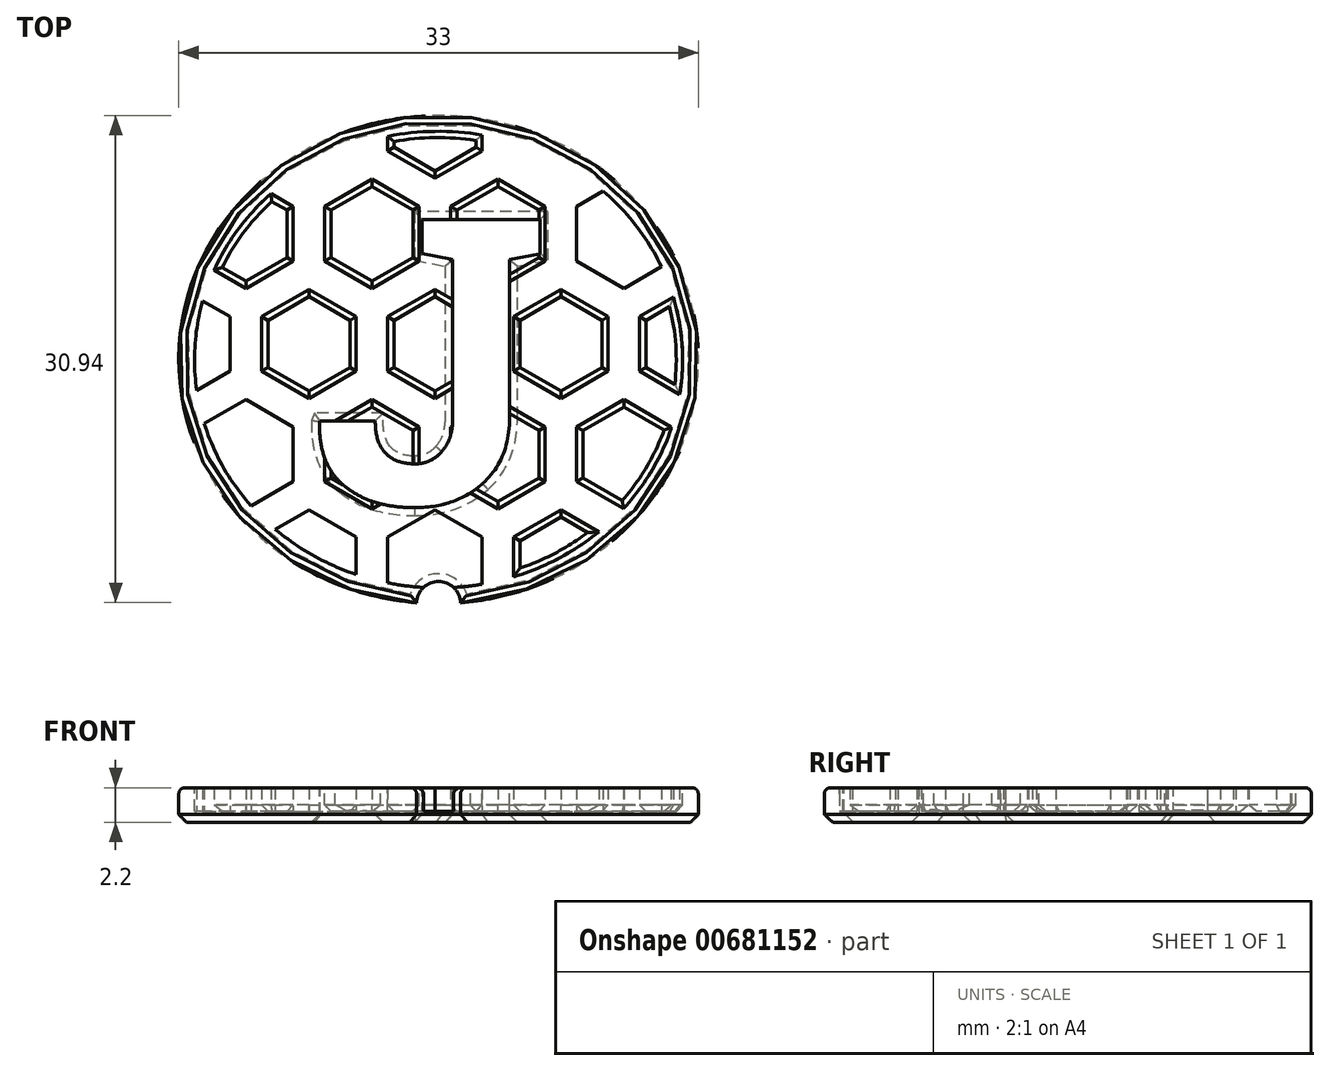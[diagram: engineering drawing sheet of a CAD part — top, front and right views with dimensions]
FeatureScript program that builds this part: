
annotation { "Feature Type Name" : "Feature", "Feature Type Description" : "" }
export const myFeature = defineFeature(function(context is Context, id is Id, definition is map)
    precondition{}
    {
        {
            var Q0;
            Q0=qCreatedBy(makeId("Top.planeOp"),FACE);
            var sketch = newSketch(context, id + "F0", { "sketchPlane" : qUnion([Q0])});
            skEllipse(sketch, "E0", {"center": v(0, 0) * mm, "majorRadius": 16.5 * mm, "minorRadius": 15.5 * mm, "majorAxis": v(1, 0)});
            skArc(sketch, "E1", {"start": v(1.4, -15.44) * mm, "mid": v(0, -14.1) * mm, "end": v(-1.4, -15.44) * mm});
            skSolve(sketch);
        }
        {
            var Q0;
            {var subQ0=sQuery(id+"F0.wireOp",EDGE,"E1");Q0=makeQuery(id+"F0.imprint","IMPRINT",FACE,{"disambiguationData":[TD([[makeQuery(id+"F0.imprint","IMPRINT",EDGE,{"derivedFrom":subQ0}),-1.0]])]});}
            extrude(context, id + "F1", {"entities" : qUnion([Q0]), "depth" : 0.7 * mm, "offsetDistance" : 25 * mm});
        }
        {
            var Q0;
            Q0=makeQuery(id+"F1.opExtrude","CAP_FACE",FACE,{"disambiguationData":[OSD([sQuery(id+"F0.wireOp",EDGE,"E0"),sQuery(id+"F0.wireOp",EDGE,"E1")])],"isStart":false});
            var sketch = newSketch(context, id + "F2", { "sketchPlane" : qUnion([Q0])});
            skCircle(sketch, "E2.cCircle", {"center": v(-20.23, -20) * mm, "radius": 3 * mm, "construction": true});
            skLineSegment(sketch, "E2.0", {"start": v(-17.23, -18.28) * mm, "end": v(-17.23, -21.74) * mm});
            skLineSegment(sketch, "E2.1", {"start": v(-17.23, -21.74) * mm, "end": v(-20.23, -23.47) * mm});
            skLineSegment(sketch, "E2.2", {"start": v(-20.23, -23.47) * mm, "end": v(-23.23, -21.74) * mm});
            skLineSegment(sketch, "E2.3", {"start": v(-23.23, -21.74) * mm, "end": v(-23.23, -18.28) * mm});
            skLineSegment(sketch, "E2.4", {"start": v(-23.23, -18.28) * mm, "end": v(-20.23, -16.54) * mm});
            skLineSegment(sketch, "E2.5", {"start": v(-20.23, -16.54) * mm, "end": v(-17.23, -18.28) * mm});
            skPoint(sketch, "E2.0.midPoint", {"position": v(-17.23, -20) * mm});
            skLineSegment(sketch, "E3.0.1.0", {"start": v(-20.23, -2.54) * mm, "end": v(-17.23, -4.28) * mm});
            skLineSegment(sketch, "E3.0.1.1", {"start": v(-17.23, -4.28) * mm, "end": v(-17.23, -7.74) * mm});
            skLineSegment(sketch, "E3.0.1.2", {"start": v(-17.23, -7.74) * mm, "end": v(-20.23, -9.47) * mm});
            skLineSegment(sketch, "E3.0.1.3", {"start": v(-20.23, -9.47) * mm, "end": v(-23.23, -7.74) * mm});
            skLineSegment(sketch, "E3.0.1.4", {"start": v(-23.23, -7.74) * mm, "end": v(-23.23, -4.28) * mm});
            skLineSegment(sketch, "E3.0.1.5", {"start": v(-23.23, -4.28) * mm, "end": v(-20.23, -2.54) * mm});
            skLineSegment(sketch, "E3.0.2.0", {"start": v(-20.23, 11.46) * mm, "end": v(-17.23, 9.72) * mm});
            skLineSegment(sketch, "E3.0.2.1", {"start": v(-17.23, 9.72) * mm, "end": v(-17.23, 6.26) * mm});
            skLineSegment(sketch, "E3.0.2.2", {"start": v(-17.23, 6.26) * mm, "end": v(-20.23, 4.53) * mm});
            skLineSegment(sketch, "E3.0.2.3", {"start": v(-20.23, 4.53) * mm, "end": v(-23.23, 6.26) * mm});
            skLineSegment(sketch, "E3.0.2.4", {"start": v(-23.23, 6.26) * mm, "end": v(-23.23, 9.72) * mm});
            skLineSegment(sketch, "E3.0.2.5", {"start": v(-23.23, 9.72) * mm, "end": v(-20.23, 11.46) * mm});
            skLineSegment(sketch, "E3.0.3.0", {"start": v(-20.23, 25.46) * mm, "end": v(-17.23, 23.72) * mm});
            skLineSegment(sketch, "E3.0.3.1", {"start": v(-17.23, 23.72) * mm, "end": v(-17.23, 20.26) * mm});
            skLineSegment(sketch, "E3.0.3.2", {"start": v(-17.23, 20.26) * mm, "end": v(-20.23, 18.53) * mm});
            skLineSegment(sketch, "E3.0.3.3", {"start": v(-20.23, 18.53) * mm, "end": v(-23.23, 20.26) * mm});
            skLineSegment(sketch, "E3.0.3.4", {"start": v(-23.23, 20.26) * mm, "end": v(-23.23, 23.72) * mm});
            skLineSegment(sketch, "E3.0.3.5", {"start": v(-23.23, 23.72) * mm, "end": v(-20.23, 25.46) * mm});
            skLineSegment(sketch, "E3.0.4.0", {"start": v(-20.23, 39.46) * mm, "end": v(-17.23, 37.72) * mm});
            skLineSegment(sketch, "E3.0.4.1", {"start": v(-17.23, 37.72) * mm, "end": v(-17.23, 34.26) * mm});
            skLineSegment(sketch, "E3.0.4.2", {"start": v(-17.23, 34.26) * mm, "end": v(-20.23, 32.53) * mm});
            skLineSegment(sketch, "E3.0.4.3", {"start": v(-20.23, 32.53) * mm, "end": v(-23.23, 34.26) * mm});
            skLineSegment(sketch, "E3.0.4.4", {"start": v(-23.23, 34.26) * mm, "end": v(-23.23, 37.72) * mm});
            skLineSegment(sketch, "E3.0.4.5", {"start": v(-23.23, 37.72) * mm, "end": v(-20.23, 39.46) * mm});
            skLineSegment(sketch, "E3.1.0.0", {"start": v(-12.23, -16.54) * mm, "end": v(-9.23, -18.28) * mm});
            skLineSegment(sketch, "E3.1.0.1", {"start": v(-9.23, -18.28) * mm, "end": v(-9.23, -21.74) * mm});
            skLineSegment(sketch, "E3.1.0.2", {"start": v(-9.23, -21.74) * mm, "end": v(-12.23, -23.47) * mm});
            skLineSegment(sketch, "E3.1.0.3", {"start": v(-12.23, -23.47) * mm, "end": v(-15.23, -21.74) * mm});
            skLineSegment(sketch, "E3.1.0.4", {"start": v(-15.23, -21.74) * mm, "end": v(-15.23, -18.28) * mm});
            skLineSegment(sketch, "E3.1.0.5", {"start": v(-15.23, -18.28) * mm, "end": v(-12.23, -16.54) * mm});
            skLineSegment(sketch, "E3.1.1.0", {"start": v(-12.23, -2.54) * mm, "end": v(-9.23, -4.28) * mm});
            skLineSegment(sketch, "E3.1.1.1", {"start": v(-9.23, -4.28) * mm, "end": v(-9.23, -7.74) * mm});
            skLineSegment(sketch, "E3.1.1.2", {"start": v(-9.23, -7.74) * mm, "end": v(-12.23, -9.47) * mm});
            skLineSegment(sketch, "E3.1.1.3", {"start": v(-12.23, -9.47) * mm, "end": v(-15.23, -7.74) * mm});
            skLineSegment(sketch, "E3.1.1.4", {"start": v(-15.23, -7.74) * mm, "end": v(-15.23, -4.28) * mm});
            skLineSegment(sketch, "E3.1.1.5", {"start": v(-15.23, -4.28) * mm, "end": v(-12.23, -2.54) * mm});
            skLineSegment(sketch, "E3.1.2.0", {"start": v(-12.23, 11.46) * mm, "end": v(-9.23, 9.72) * mm});
            skLineSegment(sketch, "E3.1.2.1", {"start": v(-9.23, 9.72) * mm, "end": v(-9.23, 6.26) * mm});
            skLineSegment(sketch, "E3.1.2.2", {"start": v(-9.23, 6.26) * mm, "end": v(-12.23, 4.53) * mm});
            skLineSegment(sketch, "E3.1.2.3", {"start": v(-12.23, 4.53) * mm, "end": v(-15.23, 6.26) * mm});
            skLineSegment(sketch, "E3.1.2.4", {"start": v(-15.23, 6.26) * mm, "end": v(-15.23, 9.72) * mm});
            skLineSegment(sketch, "E3.1.2.5", {"start": v(-15.23, 9.72) * mm, "end": v(-12.23, 11.46) * mm});
            skLineSegment(sketch, "E3.1.3.0", {"start": v(-12.23, 25.46) * mm, "end": v(-9.23, 23.72) * mm});
            skLineSegment(sketch, "E3.1.3.1", {"start": v(-9.23, 23.72) * mm, "end": v(-9.23, 20.26) * mm});
            skLineSegment(sketch, "E3.1.3.2", {"start": v(-9.23, 20.26) * mm, "end": v(-12.23, 18.53) * mm});
            skLineSegment(sketch, "E3.1.3.3", {"start": v(-12.23, 18.53) * mm, "end": v(-15.23, 20.26) * mm});
            skLineSegment(sketch, "E3.1.3.4", {"start": v(-15.23, 20.26) * mm, "end": v(-15.23, 23.72) * mm});
            skLineSegment(sketch, "E3.1.3.5", {"start": v(-15.23, 23.72) * mm, "end": v(-12.23, 25.46) * mm});
            skLineSegment(sketch, "E3.1.4.0", {"start": v(-12.23, 39.46) * mm, "end": v(-9.23, 37.72) * mm});
            skLineSegment(sketch, "E3.1.4.1", {"start": v(-9.23, 37.72) * mm, "end": v(-9.23, 34.26) * mm});
            skLineSegment(sketch, "E3.1.4.2", {"start": v(-9.23, 34.26) * mm, "end": v(-12.23, 32.53) * mm});
            skLineSegment(sketch, "E3.1.4.3", {"start": v(-12.23, 32.53) * mm, "end": v(-15.23, 34.26) * mm});
            skLineSegment(sketch, "E3.1.4.4", {"start": v(-15.23, 34.26) * mm, "end": v(-15.23, 37.72) * mm});
            skLineSegment(sketch, "E3.1.4.5", {"start": v(-15.23, 37.72) * mm, "end": v(-12.23, 39.46) * mm});
            skLineSegment(sketch, "E3.2.0.0", {"start": v(-4.23, -16.54) * mm, "end": v(-1.23, -18.28) * mm});
            skLineSegment(sketch, "E3.2.0.1", {"start": v(-1.23, -18.28) * mm, "end": v(-1.23, -21.74) * mm});
            skLineSegment(sketch, "E3.2.0.2", {"start": v(-1.23, -21.74) * mm, "end": v(-4.23, -23.47) * mm});
            skLineSegment(sketch, "E3.2.0.3", {"start": v(-4.23, -23.47) * mm, "end": v(-7.23, -21.74) * mm});
            skLineSegment(sketch, "E3.2.0.4", {"start": v(-7.23, -21.74) * mm, "end": v(-7.23, -18.28) * mm});
            skLineSegment(sketch, "E3.2.0.5", {"start": v(-7.23, -18.28) * mm, "end": v(-4.23, -16.54) * mm});
            skLineSegment(sketch, "E3.2.1.0", {"start": v(-4.23, -2.54) * mm, "end": v(-1.23, -4.28) * mm});
            skLineSegment(sketch, "E3.2.1.1", {"start": v(-1.23, -4.28) * mm, "end": v(-1.23, -7.74) * mm});
            skLineSegment(sketch, "E3.2.1.2", {"start": v(-1.23, -7.74) * mm, "end": v(-4.23, -9.47) * mm});
            skLineSegment(sketch, "E3.2.1.3", {"start": v(-4.23, -9.47) * mm, "end": v(-7.23, -7.74) * mm});
            skLineSegment(sketch, "E3.2.1.4", {"start": v(-7.23, -7.74) * mm, "end": v(-7.23, -4.28) * mm});
            skLineSegment(sketch, "E3.2.1.5", {"start": v(-7.23, -4.28) * mm, "end": v(-4.23, -2.54) * mm});
            skLineSegment(sketch, "E3.2.2.0", {"start": v(-4.23, 11.46) * mm, "end": v(-1.23, 9.72) * mm});
            skLineSegment(sketch, "E3.2.2.1", {"start": v(-1.23, 9.72) * mm, "end": v(-1.23, 6.26) * mm});
            skLineSegment(sketch, "E3.2.2.2", {"start": v(-1.23, 6.26) * mm, "end": v(-4.23, 4.53) * mm});
            skLineSegment(sketch, "E3.2.2.3", {"start": v(-4.23, 4.53) * mm, "end": v(-7.23, 6.26) * mm});
            skLineSegment(sketch, "E3.2.2.4", {"start": v(-7.23, 6.26) * mm, "end": v(-7.23, 9.72) * mm});
            skLineSegment(sketch, "E3.2.2.5", {"start": v(-7.23, 9.72) * mm, "end": v(-4.23, 11.46) * mm});
            skLineSegment(sketch, "E3.2.3.0", {"start": v(-4.23, 25.46) * mm, "end": v(-1.23, 23.72) * mm});
            skLineSegment(sketch, "E3.2.3.1", {"start": v(-1.23, 23.72) * mm, "end": v(-1.23, 20.26) * mm});
            skLineSegment(sketch, "E3.2.3.2", {"start": v(-1.23, 20.26) * mm, "end": v(-4.23, 18.53) * mm});
            skLineSegment(sketch, "E3.2.3.3", {"start": v(-4.23, 18.53) * mm, "end": v(-7.23, 20.26) * mm});
            skLineSegment(sketch, "E3.2.3.4", {"start": v(-7.23, 20.26) * mm, "end": v(-7.23, 23.72) * mm});
            skLineSegment(sketch, "E3.2.3.5", {"start": v(-7.23, 23.72) * mm, "end": v(-4.23, 25.46) * mm});
            skLineSegment(sketch, "E3.2.4.0", {"start": v(-4.23, 39.46) * mm, "end": v(-1.23, 37.72) * mm});
            skLineSegment(sketch, "E3.2.4.1", {"start": v(-1.23, 37.72) * mm, "end": v(-1.23, 34.26) * mm});
            skLineSegment(sketch, "E3.2.4.2", {"start": v(-1.23, 34.26) * mm, "end": v(-4.23, 32.53) * mm});
            skLineSegment(sketch, "E3.2.4.3", {"start": v(-4.23, 32.53) * mm, "end": v(-7.23, 34.26) * mm});
            skLineSegment(sketch, "E3.2.4.4", {"start": v(-7.23, 34.26) * mm, "end": v(-7.23, 37.72) * mm});
            skLineSegment(sketch, "E3.2.4.5", {"start": v(-7.23, 37.72) * mm, "end": v(-4.23, 39.46) * mm});
            skLineSegment(sketch, "E3.3.0.0", {"start": v(3.77, -16.54) * mm, "end": v(6.77, -18.28) * mm});
            skLineSegment(sketch, "E3.3.0.1", {"start": v(6.77, -18.28) * mm, "end": v(6.77, -21.74) * mm});
            skLineSegment(sketch, "E3.3.0.2", {"start": v(6.77, -21.74) * mm, "end": v(3.77, -23.47) * mm});
            skLineSegment(sketch, "E3.3.0.3", {"start": v(3.77, -23.47) * mm, "end": v(0.77, -21.74) * mm});
            skLineSegment(sketch, "E3.3.0.4", {"start": v(0.77, -21.74) * mm, "end": v(0.77, -18.28) * mm});
            skLineSegment(sketch, "E3.3.0.5", {"start": v(0.77, -18.28) * mm, "end": v(3.77, -16.54) * mm});
            skLineSegment(sketch, "E3.3.1.0", {"start": v(3.77, -2.54) * mm, "end": v(6.77, -4.28) * mm});
            skLineSegment(sketch, "E3.3.1.1", {"start": v(6.77, -4.28) * mm, "end": v(6.77, -7.74) * mm});
            skLineSegment(sketch, "E3.3.1.2", {"start": v(6.77, -7.74) * mm, "end": v(3.77, -9.47) * mm});
            skLineSegment(sketch, "E3.3.1.3", {"start": v(3.77, -9.47) * mm, "end": v(0.77, -7.74) * mm});
            skLineSegment(sketch, "E3.3.1.4", {"start": v(0.77, -7.74) * mm, "end": v(0.77, -4.28) * mm});
            skLineSegment(sketch, "E3.3.1.5", {"start": v(0.77, -4.28) * mm, "end": v(3.77, -2.54) * mm});
            skLineSegment(sketch, "E3.3.2.0", {"start": v(3.77, 11.46) * mm, "end": v(6.77, 9.72) * mm});
            skLineSegment(sketch, "E3.3.2.1", {"start": v(6.77, 9.72) * mm, "end": v(6.77, 6.26) * mm});
            skLineSegment(sketch, "E3.3.2.2", {"start": v(6.77, 6.26) * mm, "end": v(3.77, 4.53) * mm});
            skLineSegment(sketch, "E3.3.2.3", {"start": v(3.77, 4.53) * mm, "end": v(0.77, 6.26) * mm});
            skLineSegment(sketch, "E3.3.2.4", {"start": v(0.77, 6.26) * mm, "end": v(0.77, 9.72) * mm});
            skLineSegment(sketch, "E3.3.2.5", {"start": v(0.77, 9.72) * mm, "end": v(3.77, 11.46) * mm});
            skLineSegment(sketch, "E3.3.3.0", {"start": v(3.77, 25.46) * mm, "end": v(6.77, 23.72) * mm});
            skLineSegment(sketch, "E3.3.3.1", {"start": v(6.77, 23.72) * mm, "end": v(6.77, 20.26) * mm});
            skLineSegment(sketch, "E3.3.3.2", {"start": v(6.77, 20.26) * mm, "end": v(3.77, 18.53) * mm});
            skLineSegment(sketch, "E3.3.3.3", {"start": v(3.77, 18.53) * mm, "end": v(0.77, 20.26) * mm});
            skLineSegment(sketch, "E3.3.3.4", {"start": v(0.77, 20.26) * mm, "end": v(0.77, 23.72) * mm});
            skLineSegment(sketch, "E3.3.3.5", {"start": v(0.77, 23.72) * mm, "end": v(3.77, 25.46) * mm});
            skLineSegment(sketch, "E3.3.4.0", {"start": v(3.77, 39.46) * mm, "end": v(6.77, 37.72) * mm});
            skLineSegment(sketch, "E3.3.4.1", {"start": v(6.77, 37.72) * mm, "end": v(6.77, 34.26) * mm});
            skLineSegment(sketch, "E3.3.4.2", {"start": v(6.77, 34.26) * mm, "end": v(3.77, 32.53) * mm});
            skLineSegment(sketch, "E3.3.4.3", {"start": v(3.77, 32.53) * mm, "end": v(0.77, 34.26) * mm});
            skLineSegment(sketch, "E3.3.4.4", {"start": v(0.77, 34.26) * mm, "end": v(0.77, 37.72) * mm});
            skLineSegment(sketch, "E3.3.4.5", {"start": v(0.77, 37.72) * mm, "end": v(3.77, 39.46) * mm});
            skLineSegment(sketch, "E3.4.0.0", {"start": v(11.77, -16.54) * mm, "end": v(14.77, -18.28) * mm});
            skLineSegment(sketch, "E3.4.0.1", {"start": v(14.77, -18.28) * mm, "end": v(14.77, -21.74) * mm});
            skLineSegment(sketch, "E3.4.0.2", {"start": v(14.77, -21.74) * mm, "end": v(11.77, -23.47) * mm});
            skLineSegment(sketch, "E3.4.0.3", {"start": v(11.77, -23.47) * mm, "end": v(8.77, -21.74) * mm});
            skLineSegment(sketch, "E3.4.0.4", {"start": v(8.77, -21.74) * mm, "end": v(8.77, -18.28) * mm});
            skLineSegment(sketch, "E3.4.0.5", {"start": v(8.77, -18.28) * mm, "end": v(11.77, -16.54) * mm});
            skLineSegment(sketch, "E3.4.1.0", {"start": v(11.77, -2.54) * mm, "end": v(14.77, -4.28) * mm});
            skLineSegment(sketch, "E3.4.1.1", {"start": v(14.77, -4.28) * mm, "end": v(14.77, -7.74) * mm});
            skLineSegment(sketch, "E3.4.1.2", {"start": v(14.77, -7.74) * mm, "end": v(11.77, -9.47) * mm});
            skLineSegment(sketch, "E3.4.1.3", {"start": v(11.77, -9.47) * mm, "end": v(8.77, -7.74) * mm});
            skLineSegment(sketch, "E3.4.1.4", {"start": v(8.77, -7.74) * mm, "end": v(8.77, -4.28) * mm});
            skLineSegment(sketch, "E3.4.1.5", {"start": v(8.77, -4.28) * mm, "end": v(11.77, -2.54) * mm});
            skLineSegment(sketch, "E3.4.2.0", {"start": v(11.77, 11.46) * mm, "end": v(14.77, 9.72) * mm});
            skLineSegment(sketch, "E3.4.2.1", {"start": v(14.77, 9.72) * mm, "end": v(14.77, 6.26) * mm});
            skLineSegment(sketch, "E3.4.2.2", {"start": v(14.77, 6.26) * mm, "end": v(11.77, 4.53) * mm});
            skLineSegment(sketch, "E3.4.2.3", {"start": v(11.77, 4.53) * mm, "end": v(8.77, 6.26) * mm});
            skLineSegment(sketch, "E3.4.2.4", {"start": v(8.77, 6.26) * mm, "end": v(8.77, 9.72) * mm});
            skLineSegment(sketch, "E3.4.2.5", {"start": v(8.77, 9.72) * mm, "end": v(11.77, 11.46) * mm});
            skLineSegment(sketch, "E3.4.3.0", {"start": v(11.77, 25.46) * mm, "end": v(14.77, 23.72) * mm});
            skLineSegment(sketch, "E3.4.3.1", {"start": v(14.77, 23.72) * mm, "end": v(14.77, 20.26) * mm});
            skLineSegment(sketch, "E3.4.3.2", {"start": v(14.77, 20.26) * mm, "end": v(11.77, 18.53) * mm});
            skLineSegment(sketch, "E3.4.3.3", {"start": v(11.77, 18.53) * mm, "end": v(8.77, 20.26) * mm});
            skLineSegment(sketch, "E3.4.3.4", {"start": v(8.77, 20.26) * mm, "end": v(8.77, 23.72) * mm});
            skLineSegment(sketch, "E3.4.3.5", {"start": v(8.77, 23.72) * mm, "end": v(11.77, 25.46) * mm});
            skLineSegment(sketch, "E3.4.4.0", {"start": v(11.77, 39.46) * mm, "end": v(14.77, 37.72) * mm});
            skLineSegment(sketch, "E3.4.4.1", {"start": v(14.77, 37.72) * mm, "end": v(14.77, 34.26) * mm});
            skLineSegment(sketch, "E3.4.4.2", {"start": v(14.77, 34.26) * mm, "end": v(11.77, 32.53) * mm});
            skLineSegment(sketch, "E3.4.4.3", {"start": v(11.77, 32.53) * mm, "end": v(8.77, 34.26) * mm});
            skLineSegment(sketch, "E3.4.4.4", {"start": v(8.77, 34.26) * mm, "end": v(8.77, 37.72) * mm});
            skLineSegment(sketch, "E3.4.4.5", {"start": v(8.77, 37.72) * mm, "end": v(11.77, 39.46) * mm});
            skLineSegment(sketch, "E3.5.0.0", {"start": v(19.77, -16.54) * mm, "end": v(22.77, -18.28) * mm});
            skLineSegment(sketch, "E3.5.0.1", {"start": v(22.77, -18.28) * mm, "end": v(22.77, -21.74) * mm});
            skLineSegment(sketch, "E3.5.0.2", {"start": v(22.77, -21.74) * mm, "end": v(19.77, -23.47) * mm});
            skLineSegment(sketch, "E3.5.0.3", {"start": v(19.77, -23.47) * mm, "end": v(16.77, -21.74) * mm});
            skLineSegment(sketch, "E3.5.0.4", {"start": v(16.77, -21.74) * mm, "end": v(16.77, -18.28) * mm});
            skLineSegment(sketch, "E3.5.0.5", {"start": v(16.77, -18.28) * mm, "end": v(19.77, -16.54) * mm});
            skLineSegment(sketch, "E3.5.1.0", {"start": v(19.77, -2.54) * mm, "end": v(22.77, -4.28) * mm});
            skLineSegment(sketch, "E3.5.1.1", {"start": v(22.77, -4.28) * mm, "end": v(22.77, -7.74) * mm});
            skLineSegment(sketch, "E3.5.1.2", {"start": v(22.77, -7.74) * mm, "end": v(19.77, -9.47) * mm});
            skLineSegment(sketch, "E3.5.1.3", {"start": v(19.77, -9.47) * mm, "end": v(16.77, -7.74) * mm});
            skLineSegment(sketch, "E3.5.1.4", {"start": v(16.77, -7.74) * mm, "end": v(16.77, -4.28) * mm});
            skLineSegment(sketch, "E3.5.1.5", {"start": v(16.77, -4.28) * mm, "end": v(19.77, -2.54) * mm});
            skLineSegment(sketch, "E3.5.2.0", {"start": v(19.77, 11.46) * mm, "end": v(22.77, 9.72) * mm});
            skLineSegment(sketch, "E3.5.2.1", {"start": v(22.77, 9.72) * mm, "end": v(22.77, 6.26) * mm});
            skLineSegment(sketch, "E3.5.2.2", {"start": v(22.77, 6.26) * mm, "end": v(19.77, 4.53) * mm});
            skLineSegment(sketch, "E3.5.2.3", {"start": v(19.77, 4.53) * mm, "end": v(16.77, 6.26) * mm});
            skLineSegment(sketch, "E3.5.2.4", {"start": v(16.77, 6.26) * mm, "end": v(16.77, 9.72) * mm});
            skLineSegment(sketch, "E3.5.2.5", {"start": v(16.77, 9.72) * mm, "end": v(19.77, 11.46) * mm});
            skLineSegment(sketch, "E3.5.3.0", {"start": v(19.77, 25.46) * mm, "end": v(22.77, 23.72) * mm});
            skLineSegment(sketch, "E3.5.3.1", {"start": v(22.77, 23.72) * mm, "end": v(22.77, 20.26) * mm});
            skLineSegment(sketch, "E3.5.3.2", {"start": v(22.77, 20.26) * mm, "end": v(19.77, 18.53) * mm});
            skLineSegment(sketch, "E3.5.3.3", {"start": v(19.77, 18.53) * mm, "end": v(16.77, 20.26) * mm});
            skLineSegment(sketch, "E3.5.3.4", {"start": v(16.77, 20.26) * mm, "end": v(16.77, 23.72) * mm});
            skLineSegment(sketch, "E3.5.3.5", {"start": v(16.77, 23.72) * mm, "end": v(19.77, 25.46) * mm});
            skLineSegment(sketch, "E3.5.4.0", {"start": v(19.77, 39.46) * mm, "end": v(22.77, 37.72) * mm});
            skLineSegment(sketch, "E3.5.4.1", {"start": v(22.77, 37.72) * mm, "end": v(22.77, 34.26) * mm});
            skLineSegment(sketch, "E3.5.4.2", {"start": v(22.77, 34.26) * mm, "end": v(19.77, 32.53) * mm});
            skLineSegment(sketch, "E3.5.4.3", {"start": v(19.77, 32.53) * mm, "end": v(16.77, 34.26) * mm});
            skLineSegment(sketch, "E3.5.4.4", {"start": v(16.77, 34.26) * mm, "end": v(16.77, 37.72) * mm});
            skLineSegment(sketch, "E3.5.4.5", {"start": v(16.77, 37.72) * mm, "end": v(19.77, 39.46) * mm});
            skLineSegment(sketch, "E3.6.0.0", {"start": v(27.77, -16.54) * mm, "end": v(30.77, -18.28) * mm});
            skLineSegment(sketch, "E3.6.0.1", {"start": v(30.77, -18.28) * mm, "end": v(30.77, -21.74) * mm});
            skLineSegment(sketch, "E3.6.0.2", {"start": v(30.77, -21.74) * mm, "end": v(27.77, -23.47) * mm});
            skLineSegment(sketch, "E3.6.0.3", {"start": v(27.77, -23.47) * mm, "end": v(24.77, -21.74) * mm});
            skLineSegment(sketch, "E3.6.0.4", {"start": v(24.77, -21.74) * mm, "end": v(24.77, -18.28) * mm});
            skLineSegment(sketch, "E3.6.0.5", {"start": v(24.77, -18.28) * mm, "end": v(27.77, -16.54) * mm});
            skLineSegment(sketch, "E3.6.1.0", {"start": v(27.77, -2.54) * mm, "end": v(30.77, -4.28) * mm});
            skLineSegment(sketch, "E3.6.1.1", {"start": v(30.77, -4.28) * mm, "end": v(30.77, -7.74) * mm});
            skLineSegment(sketch, "E3.6.1.2", {"start": v(30.77, -7.74) * mm, "end": v(27.77, -9.47) * mm});
            skLineSegment(sketch, "E3.6.1.3", {"start": v(27.77, -9.47) * mm, "end": v(24.77, -7.74) * mm});
            skLineSegment(sketch, "E3.6.1.4", {"start": v(24.77, -7.74) * mm, "end": v(24.77, -4.28) * mm});
            skLineSegment(sketch, "E3.6.1.5", {"start": v(24.77, -4.28) * mm, "end": v(27.77, -2.54) * mm});
            skLineSegment(sketch, "E3.6.2.0", {"start": v(27.77, 11.46) * mm, "end": v(30.77, 9.72) * mm});
            skLineSegment(sketch, "E3.6.2.1", {"start": v(30.77, 9.72) * mm, "end": v(30.77, 6.26) * mm});
            skLineSegment(sketch, "E3.6.2.2", {"start": v(30.77, 6.26) * mm, "end": v(27.77, 4.53) * mm});
            skLineSegment(sketch, "E3.6.2.3", {"start": v(27.77, 4.53) * mm, "end": v(24.77, 6.26) * mm});
            skLineSegment(sketch, "E3.6.2.4", {"start": v(24.77, 6.26) * mm, "end": v(24.77, 9.72) * mm});
            skLineSegment(sketch, "E3.6.2.5", {"start": v(24.77, 9.72) * mm, "end": v(27.77, 11.46) * mm});
            skLineSegment(sketch, "E3.6.3.0", {"start": v(27.77, 25.46) * mm, "end": v(30.77, 23.72) * mm});
            skLineSegment(sketch, "E3.6.3.1", {"start": v(30.77, 23.72) * mm, "end": v(30.77, 20.26) * mm});
            skLineSegment(sketch, "E3.6.3.2", {"start": v(30.77, 20.26) * mm, "end": v(27.77, 18.53) * mm});
            skLineSegment(sketch, "E3.6.3.3", {"start": v(27.77, 18.53) * mm, "end": v(24.77, 20.26) * mm});
            skLineSegment(sketch, "E3.6.3.4", {"start": v(24.77, 20.26) * mm, "end": v(24.77, 23.72) * mm});
            skLineSegment(sketch, "E3.6.3.5", {"start": v(24.77, 23.72) * mm, "end": v(27.77, 25.46) * mm});
            skLineSegment(sketch, "E3.6.4.0", {"start": v(27.77, 39.46) * mm, "end": v(30.77, 37.72) * mm});
            skLineSegment(sketch, "E3.6.4.1", {"start": v(30.77, 37.72) * mm, "end": v(30.77, 34.26) * mm});
            skLineSegment(sketch, "E3.6.4.2", {"start": v(30.77, 34.26) * mm, "end": v(27.77, 32.53) * mm});
            skLineSegment(sketch, "E3.6.4.3", {"start": v(27.77, 32.53) * mm, "end": v(24.77, 34.26) * mm});
            skLineSegment(sketch, "E3.6.4.4", {"start": v(24.77, 34.26) * mm, "end": v(24.77, 37.72) * mm});
            skLineSegment(sketch, "E3.6.4.5", {"start": v(24.77, 37.72) * mm, "end": v(27.77, 39.46) * mm});
            skLineSegment(sketch, "E3.7.0.0", {"start": v(35.77, -16.54) * mm, "end": v(38.77, -18.28) * mm});
            skLineSegment(sketch, "E3.7.0.1", {"start": v(38.77, -18.28) * mm, "end": v(38.77, -21.74) * mm});
            skLineSegment(sketch, "E3.7.0.2", {"start": v(38.77, -21.74) * mm, "end": v(35.77, -23.47) * mm});
            skLineSegment(sketch, "E3.7.0.3", {"start": v(35.77, -23.47) * mm, "end": v(32.77, -21.74) * mm});
            skLineSegment(sketch, "E3.7.0.4", {"start": v(32.77, -21.74) * mm, "end": v(32.77, -18.28) * mm});
            skLineSegment(sketch, "E3.7.0.5", {"start": v(32.77, -18.28) * mm, "end": v(35.77, -16.54) * mm});
            skLineSegment(sketch, "E3.7.1.0", {"start": v(35.77, -2.54) * mm, "end": v(38.77, -4.28) * mm});
            skLineSegment(sketch, "E3.7.1.1", {"start": v(38.77, -4.28) * mm, "end": v(38.77, -7.74) * mm});
            skLineSegment(sketch, "E3.7.1.2", {"start": v(38.77, -7.74) * mm, "end": v(35.77, -9.47) * mm});
            skLineSegment(sketch, "E3.7.1.3", {"start": v(35.77, -9.47) * mm, "end": v(32.77, -7.74) * mm});
            skLineSegment(sketch, "E3.7.1.4", {"start": v(32.77, -7.74) * mm, "end": v(32.77, -4.28) * mm});
            skLineSegment(sketch, "E3.7.1.5", {"start": v(32.77, -4.28) * mm, "end": v(35.77, -2.54) * mm});
            skLineSegment(sketch, "E3.7.2.0", {"start": v(35.77, 11.46) * mm, "end": v(38.77, 9.72) * mm});
            skLineSegment(sketch, "E3.7.2.1", {"start": v(38.77, 9.72) * mm, "end": v(38.77, 6.26) * mm});
            skLineSegment(sketch, "E3.7.2.2", {"start": v(38.77, 6.26) * mm, "end": v(35.77, 4.53) * mm});
            skLineSegment(sketch, "E3.7.2.3", {"start": v(35.77, 4.53) * mm, "end": v(32.77, 6.26) * mm});
            skLineSegment(sketch, "E3.7.2.4", {"start": v(32.77, 6.26) * mm, "end": v(32.77, 9.72) * mm});
            skLineSegment(sketch, "E3.7.2.5", {"start": v(32.77, 9.72) * mm, "end": v(35.77, 11.46) * mm});
            skLineSegment(sketch, "E3.7.3.0", {"start": v(35.77, 25.46) * mm, "end": v(38.77, 23.72) * mm});
            skLineSegment(sketch, "E3.7.3.1", {"start": v(38.77, 23.72) * mm, "end": v(38.77, 20.26) * mm});
            skLineSegment(sketch, "E3.7.3.2", {"start": v(38.77, 20.26) * mm, "end": v(35.77, 18.53) * mm});
            skLineSegment(sketch, "E3.7.3.3", {"start": v(35.77, 18.53) * mm, "end": v(32.77, 20.26) * mm});
            skLineSegment(sketch, "E3.7.3.4", {"start": v(32.77, 20.26) * mm, "end": v(32.77, 23.72) * mm});
            skLineSegment(sketch, "E3.7.3.5", {"start": v(32.77, 23.72) * mm, "end": v(35.77, 25.46) * mm});
            skLineSegment(sketch, "E3.7.4.0", {"start": v(35.77, 39.46) * mm, "end": v(38.77, 37.72) * mm});
            skLineSegment(sketch, "E3.7.4.1", {"start": v(38.77, 37.72) * mm, "end": v(38.77, 34.26) * mm});
            skLineSegment(sketch, "E3.7.4.2", {"start": v(38.77, 34.26) * mm, "end": v(35.77, 32.53) * mm});
            skLineSegment(sketch, "E3.7.4.3", {"start": v(35.77, 32.53) * mm, "end": v(32.77, 34.26) * mm});
            skLineSegment(sketch, "E3.7.4.4", {"start": v(32.77, 34.26) * mm, "end": v(32.77, 37.72) * mm});
            skLineSegment(sketch, "E3.7.4.5", {"start": v(32.77, 37.72) * mm, "end": v(35.77, 39.46) * mm});
            skLineSegment(sketch, "E3.8.0.0", {"start": v(43.77, -16.54) * mm, "end": v(46.77, -18.28) * mm});
            skLineSegment(sketch, "E3.8.0.1", {"start": v(46.77, -18.28) * mm, "end": v(46.77, -21.74) * mm});
            skLineSegment(sketch, "E3.8.0.2", {"start": v(46.77, -21.74) * mm, "end": v(43.77, -23.47) * mm});
            skLineSegment(sketch, "E3.8.0.3", {"start": v(43.77, -23.47) * mm, "end": v(40.77, -21.74) * mm});
            skLineSegment(sketch, "E3.8.0.4", {"start": v(40.77, -21.74) * mm, "end": v(40.77, -18.28) * mm});
            skLineSegment(sketch, "E3.8.0.5", {"start": v(40.77, -18.28) * mm, "end": v(43.77, -16.54) * mm});
            skLineSegment(sketch, "E3.8.1.0", {"start": v(43.77, -2.54) * mm, "end": v(46.77, -4.28) * mm});
            skLineSegment(sketch, "E3.8.1.1", {"start": v(46.77, -4.28) * mm, "end": v(46.77, -7.74) * mm});
            skLineSegment(sketch, "E3.8.1.2", {"start": v(46.77, -7.74) * mm, "end": v(43.77, -9.47) * mm});
            skLineSegment(sketch, "E3.8.1.3", {"start": v(43.77, -9.47) * mm, "end": v(40.77, -7.74) * mm});
            skLineSegment(sketch, "E3.8.1.4", {"start": v(40.77, -7.74) * mm, "end": v(40.77, -4.28) * mm});
            skLineSegment(sketch, "E3.8.1.5", {"start": v(40.77, -4.28) * mm, "end": v(43.77, -2.54) * mm});
            skLineSegment(sketch, "E3.8.2.0", {"start": v(43.77, 11.46) * mm, "end": v(46.77, 9.72) * mm});
            skLineSegment(sketch, "E3.8.2.1", {"start": v(46.77, 9.72) * mm, "end": v(46.77, 6.26) * mm});
            skLineSegment(sketch, "E3.8.2.2", {"start": v(46.77, 6.26) * mm, "end": v(43.77, 4.53) * mm});
            skLineSegment(sketch, "E3.8.2.3", {"start": v(43.77, 4.53) * mm, "end": v(40.77, 6.26) * mm});
            skLineSegment(sketch, "E3.8.2.4", {"start": v(40.77, 6.26) * mm, "end": v(40.77, 9.72) * mm});
            skLineSegment(sketch, "E3.8.2.5", {"start": v(40.77, 9.72) * mm, "end": v(43.77, 11.46) * mm});
            skLineSegment(sketch, "E3.8.3.0", {"start": v(43.77, 25.46) * mm, "end": v(46.77, 23.72) * mm});
            skLineSegment(sketch, "E3.8.3.1", {"start": v(46.77, 23.72) * mm, "end": v(46.77, 20.26) * mm});
            skLineSegment(sketch, "E3.8.3.2", {"start": v(46.77, 20.26) * mm, "end": v(43.77, 18.53) * mm});
            skLineSegment(sketch, "E3.8.3.3", {"start": v(43.77, 18.53) * mm, "end": v(40.77, 20.26) * mm});
            skLineSegment(sketch, "E3.8.3.4", {"start": v(40.77, 20.26) * mm, "end": v(40.77, 23.72) * mm});
            skLineSegment(sketch, "E3.8.3.5", {"start": v(40.77, 23.72) * mm, "end": v(43.77, 25.46) * mm});
            skLineSegment(sketch, "E3.8.4.0", {"start": v(43.77, 39.46) * mm, "end": v(46.77, 37.72) * mm});
            skLineSegment(sketch, "E3.8.4.1", {"start": v(46.77, 37.72) * mm, "end": v(46.77, 34.26) * mm});
            skLineSegment(sketch, "E3.8.4.2", {"start": v(46.77, 34.26) * mm, "end": v(43.77, 32.53) * mm});
            skLineSegment(sketch, "E3.8.4.3", {"start": v(43.77, 32.53) * mm, "end": v(40.77, 34.26) * mm});
            skLineSegment(sketch, "E3.8.4.4", {"start": v(40.77, 34.26) * mm, "end": v(40.77, 37.72) * mm});
            skLineSegment(sketch, "E3.8.4.5", {"start": v(40.77, 37.72) * mm, "end": v(43.77, 39.46) * mm});
            skLineSegment(sketch, "E3.9.0.0", {"start": v(51.77, -16.54) * mm, "end": v(54.77, -18.28) * mm});
            skLineSegment(sketch, "E3.9.0.1", {"start": v(54.77, -18.28) * mm, "end": v(54.77, -21.74) * mm});
            skLineSegment(sketch, "E3.9.0.2", {"start": v(54.77, -21.74) * mm, "end": v(51.77, -23.47) * mm});
            skLineSegment(sketch, "E3.9.0.3", {"start": v(51.77, -23.47) * mm, "end": v(48.77, -21.74) * mm});
            skLineSegment(sketch, "E3.9.0.4", {"start": v(48.77, -21.74) * mm, "end": v(48.77, -18.28) * mm});
            skLineSegment(sketch, "E3.9.0.5", {"start": v(48.77, -18.28) * mm, "end": v(51.77, -16.54) * mm});
            skLineSegment(sketch, "E3.9.1.0", {"start": v(51.77, -2.54) * mm, "end": v(54.77, -4.28) * mm});
            skLineSegment(sketch, "E3.9.1.1", {"start": v(54.77, -4.28) * mm, "end": v(54.77, -7.74) * mm});
            skLineSegment(sketch, "E3.9.1.2", {"start": v(54.77, -7.74) * mm, "end": v(51.77, -9.47) * mm});
            skLineSegment(sketch, "E3.9.1.3", {"start": v(51.77, -9.47) * mm, "end": v(48.77, -7.74) * mm});
            skLineSegment(sketch, "E3.9.1.4", {"start": v(48.77, -7.74) * mm, "end": v(48.77, -4.28) * mm});
            skLineSegment(sketch, "E3.9.1.5", {"start": v(48.77, -4.28) * mm, "end": v(51.77, -2.54) * mm});
            skLineSegment(sketch, "E3.9.2.0", {"start": v(51.77, 11.46) * mm, "end": v(54.77, 9.72) * mm});
            skLineSegment(sketch, "E3.9.2.1", {"start": v(54.77, 9.72) * mm, "end": v(54.77, 6.26) * mm});
            skLineSegment(sketch, "E3.9.2.2", {"start": v(54.77, 6.26) * mm, "end": v(51.77, 4.53) * mm});
            skLineSegment(sketch, "E3.9.2.3", {"start": v(51.77, 4.53) * mm, "end": v(48.77, 6.26) * mm});
            skLineSegment(sketch, "E3.9.2.4", {"start": v(48.77, 6.26) * mm, "end": v(48.77, 9.72) * mm});
            skLineSegment(sketch, "E3.9.2.5", {"start": v(48.77, 9.72) * mm, "end": v(51.77, 11.46) * mm});
            skLineSegment(sketch, "E3.9.3.0", {"start": v(51.77, 25.46) * mm, "end": v(54.77, 23.72) * mm});
            skLineSegment(sketch, "E3.9.3.1", {"start": v(54.77, 23.72) * mm, "end": v(54.77, 20.26) * mm});
            skLineSegment(sketch, "E3.9.3.2", {"start": v(54.77, 20.26) * mm, "end": v(51.77, 18.53) * mm});
            skLineSegment(sketch, "E3.9.3.3", {"start": v(51.77, 18.53) * mm, "end": v(48.77, 20.26) * mm});
            skLineSegment(sketch, "E3.9.3.4", {"start": v(48.77, 20.26) * mm, "end": v(48.77, 23.72) * mm});
            skLineSegment(sketch, "E3.9.3.5", {"start": v(48.77, 23.72) * mm, "end": v(51.77, 25.46) * mm});
            skLineSegment(sketch, "E3.9.4.0", {"start": v(51.77, 39.46) * mm, "end": v(54.77, 37.72) * mm});
            skLineSegment(sketch, "E3.9.4.1", {"start": v(54.77, 37.72) * mm, "end": v(54.77, 34.26) * mm});
            skLineSegment(sketch, "E3.9.4.2", {"start": v(54.77, 34.26) * mm, "end": v(51.77, 32.53) * mm});
            skLineSegment(sketch, "E3.9.4.3", {"start": v(51.77, 32.53) * mm, "end": v(48.77, 34.26) * mm});
            skLineSegment(sketch, "E3.9.4.4", {"start": v(48.77, 34.26) * mm, "end": v(48.77, 37.72) * mm});
            skLineSegment(sketch, "E3.9.4.5", {"start": v(48.77, 37.72) * mm, "end": v(51.77, 39.46) * mm});
            skLineSegment(sketch, "E3.direction1", {"start": v(-20.23, -16.54) * mm, "end": v(-12.23, -16.54) * mm, "construction": true});
            skLineSegment(sketch, "E3.direction2", {"start": v(-20.23, -16.54) * mm, "end": v(-20.23, -2.54) * mm, "construction": true});
            skLineSegment(sketch, "E4.0.0.5", {"start": v(-20.23, 53.46) * mm, "end": v(-17.23, 51.72) * mm});
            skLineSegment(sketch, "E4.3.0.5", {"start": v(-17.23, 51.72) * mm, "end": v(-17.23, 48.26) * mm});
            skLineSegment(sketch, "E4.6.0.5", {"start": v(-17.23, 48.26) * mm, "end": v(-20.23, 46.53) * mm});
            skLineSegment(sketch, "E4.9.0.5", {"start": v(-20.23, 46.53) * mm, "end": v(-23.23, 48.26) * mm});
            skLineSegment(sketch, "E4.12.0.5", {"start": v(-23.23, 48.26) * mm, "end": v(-23.23, 51.72) * mm});
            skLineSegment(sketch, "E4.15.0.5", {"start": v(-23.23, 51.72) * mm, "end": v(-20.23, 53.46) * mm});
            skLineSegment(sketch, "E4.0.1.5", {"start": v(-12.23, 53.46) * mm, "end": v(-9.23, 51.72) * mm});
            skLineSegment(sketch, "E4.3.1.5", {"start": v(-9.23, 51.72) * mm, "end": v(-9.23, 48.26) * mm});
            skLineSegment(sketch, "E4.6.1.5", {"start": v(-9.23, 48.26) * mm, "end": v(-12.23, 46.53) * mm});
            skLineSegment(sketch, "E4.9.1.5", {"start": v(-12.23, 46.53) * mm, "end": v(-15.23, 48.26) * mm});
            skLineSegment(sketch, "E4.12.1.5", {"start": v(-15.23, 48.26) * mm, "end": v(-15.23, 51.72) * mm});
            skLineSegment(sketch, "E4.15.1.5", {"start": v(-15.23, 51.72) * mm, "end": v(-12.23, 53.46) * mm});
            skLineSegment(sketch, "E4.0.2.5", {"start": v(-4.23, 53.46) * mm, "end": v(-1.23, 51.72) * mm});
            skLineSegment(sketch, "E4.3.2.5", {"start": v(-1.23, 51.72) * mm, "end": v(-1.23, 48.26) * mm});
            skLineSegment(sketch, "E4.6.2.5", {"start": v(-1.23, 48.26) * mm, "end": v(-4.23, 46.53) * mm});
            skLineSegment(sketch, "E4.9.2.5", {"start": v(-4.23, 46.53) * mm, "end": v(-7.23, 48.26) * mm});
            skLineSegment(sketch, "E4.12.2.5", {"start": v(-7.23, 48.26) * mm, "end": v(-7.23, 51.72) * mm});
            skLineSegment(sketch, "E4.15.2.5", {"start": v(-7.23, 51.72) * mm, "end": v(-4.23, 53.46) * mm});
            skLineSegment(sketch, "E4.0.3.5", {"start": v(3.77, 53.46) * mm, "end": v(6.77, 51.72) * mm});
            skLineSegment(sketch, "E4.3.3.5", {"start": v(6.77, 51.72) * mm, "end": v(6.77, 48.26) * mm});
            skLineSegment(sketch, "E4.6.3.5", {"start": v(6.77, 48.26) * mm, "end": v(3.77, 46.53) * mm});
            skLineSegment(sketch, "E4.9.3.5", {"start": v(3.77, 46.53) * mm, "end": v(0.77, 48.26) * mm});
            skLineSegment(sketch, "E4.12.3.5", {"start": v(0.77, 48.26) * mm, "end": v(0.77, 51.72) * mm});
            skLineSegment(sketch, "E4.15.3.5", {"start": v(0.77, 51.72) * mm, "end": v(3.77, 53.46) * mm});
            skLineSegment(sketch, "E4.0.4.5", {"start": v(11.77, 53.46) * mm, "end": v(14.77, 51.72) * mm});
            skLineSegment(sketch, "E4.3.4.5", {"start": v(14.77, 51.72) * mm, "end": v(14.77, 48.26) * mm});
            skLineSegment(sketch, "E4.6.4.5", {"start": v(14.77, 48.26) * mm, "end": v(11.77, 46.53) * mm});
            skLineSegment(sketch, "E4.9.4.5", {"start": v(11.77, 46.53) * mm, "end": v(8.77, 48.26) * mm});
            skLineSegment(sketch, "E4.12.4.5", {"start": v(8.77, 48.26) * mm, "end": v(8.77, 51.72) * mm});
            skLineSegment(sketch, "E4.15.4.5", {"start": v(8.77, 51.72) * mm, "end": v(11.77, 53.46) * mm});
            skLineSegment(sketch, "E4.0.5.5", {"start": v(19.77, 53.46) * mm, "end": v(22.77, 51.72) * mm});
            skLineSegment(sketch, "E4.3.5.5", {"start": v(22.77, 51.72) * mm, "end": v(22.77, 48.26) * mm});
            skLineSegment(sketch, "E4.6.5.5", {"start": v(22.77, 48.26) * mm, "end": v(19.77, 46.53) * mm});
            skLineSegment(sketch, "E4.9.5.5", {"start": v(19.77, 46.53) * mm, "end": v(16.77, 48.26) * mm});
            skLineSegment(sketch, "E4.12.5.5", {"start": v(16.77, 48.26) * mm, "end": v(16.77, 51.72) * mm});
            skLineSegment(sketch, "E4.15.5.5", {"start": v(16.77, 51.72) * mm, "end": v(19.77, 53.46) * mm});
            skLineSegment(sketch, "E4.0.6.5", {"start": v(27.77, 53.46) * mm, "end": v(30.77, 51.72) * mm});
            skLineSegment(sketch, "E4.3.6.5", {"start": v(30.77, 51.72) * mm, "end": v(30.77, 48.26) * mm});
            skLineSegment(sketch, "E4.6.6.5", {"start": v(30.77, 48.26) * mm, "end": v(27.77, 46.53) * mm});
            skLineSegment(sketch, "E4.9.6.5", {"start": v(27.77, 46.53) * mm, "end": v(24.77, 48.26) * mm});
            skLineSegment(sketch, "E4.12.6.5", {"start": v(24.77, 48.26) * mm, "end": v(24.77, 51.72) * mm});
            skLineSegment(sketch, "E4.15.6.5", {"start": v(24.77, 51.72) * mm, "end": v(27.77, 53.46) * mm});
            skLineSegment(sketch, "E4.0.7.5", {"start": v(35.77, 53.46) * mm, "end": v(38.77, 51.72) * mm});
            skLineSegment(sketch, "E4.3.7.5", {"start": v(38.77, 51.72) * mm, "end": v(38.77, 48.26) * mm});
            skLineSegment(sketch, "E4.6.7.5", {"start": v(38.77, 48.26) * mm, "end": v(35.77, 46.53) * mm});
            skLineSegment(sketch, "E4.9.7.5", {"start": v(35.77, 46.53) * mm, "end": v(32.77, 48.26) * mm});
            skLineSegment(sketch, "E4.12.7.5", {"start": v(32.77, 48.26) * mm, "end": v(32.77, 51.72) * mm});
            skLineSegment(sketch, "E4.15.7.5", {"start": v(32.77, 51.72) * mm, "end": v(35.77, 53.46) * mm});
            skLineSegment(sketch, "E4.0.8.5", {"start": v(43.77, 53.46) * mm, "end": v(46.77, 51.72) * mm});
            skLineSegment(sketch, "E4.3.8.5", {"start": v(46.77, 51.72) * mm, "end": v(46.77, 48.26) * mm});
            skLineSegment(sketch, "E4.6.8.5", {"start": v(46.77, 48.26) * mm, "end": v(43.77, 46.53) * mm});
            skLineSegment(sketch, "E4.9.8.5", {"start": v(43.77, 46.53) * mm, "end": v(40.77, 48.26) * mm});
            skLineSegment(sketch, "E4.12.8.5", {"start": v(40.77, 48.26) * mm, "end": v(40.77, 51.72) * mm});
            skLineSegment(sketch, "E4.15.8.5", {"start": v(40.77, 51.72) * mm, "end": v(43.77, 53.46) * mm});
            skLineSegment(sketch, "E4.0.9.5", {"start": v(51.77, 53.46) * mm, "end": v(54.77, 51.72) * mm});
            skLineSegment(sketch, "E4.3.9.5", {"start": v(54.77, 51.72) * mm, "end": v(54.77, 48.26) * mm});
            skLineSegment(sketch, "E4.6.9.5", {"start": v(54.77, 48.26) * mm, "end": v(51.77, 46.53) * mm});
            skLineSegment(sketch, "E4.9.9.5", {"start": v(51.77, 46.53) * mm, "end": v(48.77, 48.26) * mm});
            skLineSegment(sketch, "E4.12.9.5", {"start": v(48.77, 48.26) * mm, "end": v(48.77, 51.72) * mm});
            skLineSegment(sketch, "E4.15.9.5", {"start": v(48.77, 51.72) * mm, "end": v(51.77, 53.46) * mm});
            skCircle(sketch, "E5.cCircle", {"center": v(-16.23, -13) * mm, "radius": 3 * mm, "construction": true});
            skLineSegment(sketch, "E5.0", {"start": v(-13.23, -11.28) * mm, "end": v(-13.23, -14.74) * mm});
            skLineSegment(sketch, "E5.1", {"start": v(-13.23, -14.74) * mm, "end": v(-16.23, -16.47) * mm});
            skLineSegment(sketch, "E5.2", {"start": v(-16.23, -16.47) * mm, "end": v(-19.23, -14.74) * mm});
            skLineSegment(sketch, "E5.3", {"start": v(-19.23, -14.74) * mm, "end": v(-19.23, -11.28) * mm});
            skLineSegment(sketch, "E5.4", {"start": v(-19.23, -11.28) * mm, "end": v(-16.23, -9.54) * mm});
            skLineSegment(sketch, "E5.5", {"start": v(-16.23, -9.54) * mm, "end": v(-13.23, -11.28) * mm});
            skPoint(sketch, "E5.0.midPoint", {"position": v(-13.23, -13) * mm});
            skLineSegment(sketch, "E6", {"start": v(-18.73, -17.4) * mm, "end": v(-13.73, -8.6) * mm, "construction": true});
            skLineSegment(sketch, "E7", {"start": v(-18.73, -8.6) * mm, "end": v(-13.73, -17.4) * mm, "construction": true});
            skLineSegment(sketch, "E8.0.1.0", {"start": v(-19.23, -0.74) * mm, "end": v(-19.23, 2.72) * mm});
            skLineSegment(sketch, "E8.0.1.1", {"start": v(-19.23, 2.72) * mm, "end": v(-16.23, 4.46) * mm});
            skLineSegment(sketch, "E8.0.1.2", {"start": v(-16.23, 4.46) * mm, "end": v(-13.23, 2.72) * mm});
            skLineSegment(sketch, "E8.0.1.3", {"start": v(-13.23, 2.72) * mm, "end": v(-13.23, -0.74) * mm});
            skLineSegment(sketch, "E8.0.1.4", {"start": v(-13.23, -0.74) * mm, "end": v(-16.23, -2.47) * mm});
            skLineSegment(sketch, "E8.0.1.5", {"start": v(-16.23, -2.47) * mm, "end": v(-19.23, -0.74) * mm});
            skLineSegment(sketch, "E8.0.2.0", {"start": v(-19.23, 13.26) * mm, "end": v(-19.23, 16.72) * mm});
            skLineSegment(sketch, "E8.0.2.1", {"start": v(-19.23, 16.72) * mm, "end": v(-16.23, 18.46) * mm});
            skLineSegment(sketch, "E8.0.2.2", {"start": v(-16.23, 18.46) * mm, "end": v(-13.23, 16.72) * mm});
            skLineSegment(sketch, "E8.0.2.3", {"start": v(-13.23, 16.72) * mm, "end": v(-13.23, 13.26) * mm});
            skLineSegment(sketch, "E8.0.2.4", {"start": v(-13.23, 13.26) * mm, "end": v(-16.23, 11.53) * mm});
            skLineSegment(sketch, "E8.0.2.5", {"start": v(-16.23, 11.53) * mm, "end": v(-19.23, 13.26) * mm});
            skLineSegment(sketch, "E8.0.3.0", {"start": v(-19.23, 27.26) * mm, "end": v(-19.23, 30.72) * mm});
            skLineSegment(sketch, "E8.0.3.1", {"start": v(-19.23, 30.72) * mm, "end": v(-16.23, 32.46) * mm});
            skLineSegment(sketch, "E8.0.3.2", {"start": v(-16.23, 32.46) * mm, "end": v(-13.23, 30.72) * mm});
            skLineSegment(sketch, "E8.0.3.3", {"start": v(-13.23, 30.72) * mm, "end": v(-13.23, 27.26) * mm});
            skLineSegment(sketch, "E8.0.3.4", {"start": v(-13.23, 27.26) * mm, "end": v(-16.23, 25.53) * mm});
            skLineSegment(sketch, "E8.0.3.5", {"start": v(-16.23, 25.53) * mm, "end": v(-19.23, 27.26) * mm});
            skLineSegment(sketch, "E8.0.4.0", {"start": v(-19.23, 41.26) * mm, "end": v(-19.23, 44.72) * mm});
            skLineSegment(sketch, "E8.0.4.1", {"start": v(-19.23, 44.72) * mm, "end": v(-16.23, 46.46) * mm});
            skLineSegment(sketch, "E8.0.4.2", {"start": v(-16.23, 46.46) * mm, "end": v(-13.23, 44.72) * mm});
            skLineSegment(sketch, "E8.0.4.3", {"start": v(-13.23, 44.72) * mm, "end": v(-13.23, 41.26) * mm});
            skLineSegment(sketch, "E8.0.4.4", {"start": v(-13.23, 41.26) * mm, "end": v(-16.23, 39.53) * mm});
            skLineSegment(sketch, "E8.0.4.5", {"start": v(-16.23, 39.53) * mm, "end": v(-19.23, 41.26) * mm});
            skLineSegment(sketch, "E8.0.5.0", {"start": v(-19.23, 55.26) * mm, "end": v(-19.23, 58.72) * mm});
            skLineSegment(sketch, "E8.0.5.1", {"start": v(-19.23, 58.72) * mm, "end": v(-16.23, 60.46) * mm});
            skLineSegment(sketch, "E8.0.5.2", {"start": v(-16.23, 60.46) * mm, "end": v(-13.23, 58.72) * mm});
            skLineSegment(sketch, "E8.0.5.3", {"start": v(-13.23, 58.72) * mm, "end": v(-13.23, 55.26) * mm});
            skLineSegment(sketch, "E8.0.5.4", {"start": v(-13.23, 55.26) * mm, "end": v(-16.23, 53.53) * mm});
            skLineSegment(sketch, "E8.0.5.5", {"start": v(-16.23, 53.53) * mm, "end": v(-19.23, 55.26) * mm});
            skLineSegment(sketch, "E8.1.0.0", {"start": v(-11.23, -14.74) * mm, "end": v(-11.23, -11.28) * mm});
            skLineSegment(sketch, "E8.1.0.1", {"start": v(-11.23, -11.28) * mm, "end": v(-8.23, -9.54) * mm});
            skLineSegment(sketch, "E8.1.0.2", {"start": v(-8.23, -9.54) * mm, "end": v(-5.23, -11.28) * mm});
            skLineSegment(sketch, "E8.1.0.3", {"start": v(-5.23, -11.28) * mm, "end": v(-5.23, -14.74) * mm});
            skLineSegment(sketch, "E8.1.0.4", {"start": v(-5.23, -14.74) * mm, "end": v(-8.23, -16.47) * mm});
            skLineSegment(sketch, "E8.1.0.5", {"start": v(-8.23, -16.47) * mm, "end": v(-11.23, -14.74) * mm});
            skLineSegment(sketch, "E8.1.1.0", {"start": v(-11.23, -0.74) * mm, "end": v(-11.23, 2.72) * mm});
            skLineSegment(sketch, "E8.1.1.1", {"start": v(-11.23, 2.72) * mm, "end": v(-8.23, 4.46) * mm});
            skLineSegment(sketch, "E8.1.1.2", {"start": v(-8.23, 4.46) * mm, "end": v(-5.23, 2.72) * mm});
            skLineSegment(sketch, "E8.1.1.3", {"start": v(-5.23, 2.72) * mm, "end": v(-5.23, -0.74) * mm});
            skLineSegment(sketch, "E8.1.1.4", {"start": v(-5.23, -0.74) * mm, "end": v(-8.23, -2.47) * mm});
            skLineSegment(sketch, "E8.1.1.5", {"start": v(-8.23, -2.47) * mm, "end": v(-11.23, -0.74) * mm});
            skLineSegment(sketch, "E8.1.2.0", {"start": v(-11.23, 13.26) * mm, "end": v(-11.23, 16.72) * mm});
            skLineSegment(sketch, "E8.1.2.1", {"start": v(-11.23, 16.72) * mm, "end": v(-8.23, 18.46) * mm});
            skLineSegment(sketch, "E8.1.2.2", {"start": v(-8.23, 18.46) * mm, "end": v(-5.23, 16.72) * mm});
            skLineSegment(sketch, "E8.1.2.3", {"start": v(-5.23, 16.72) * mm, "end": v(-5.23, 13.26) * mm});
            skLineSegment(sketch, "E8.1.2.4", {"start": v(-5.23, 13.26) * mm, "end": v(-8.23, 11.53) * mm});
            skLineSegment(sketch, "E8.1.2.5", {"start": v(-8.23, 11.53) * mm, "end": v(-11.23, 13.26) * mm});
            skLineSegment(sketch, "E8.1.3.0", {"start": v(-11.23, 27.26) * mm, "end": v(-11.23, 30.72) * mm});
            skLineSegment(sketch, "E8.1.3.1", {"start": v(-11.23, 30.72) * mm, "end": v(-8.23, 32.46) * mm});
            skLineSegment(sketch, "E8.1.3.2", {"start": v(-8.23, 32.46) * mm, "end": v(-5.23, 30.72) * mm});
            skLineSegment(sketch, "E8.1.3.3", {"start": v(-5.23, 30.72) * mm, "end": v(-5.23, 27.26) * mm});
            skLineSegment(sketch, "E8.1.3.4", {"start": v(-5.23, 27.26) * mm, "end": v(-8.23, 25.53) * mm});
            skLineSegment(sketch, "E8.1.3.5", {"start": v(-8.23, 25.53) * mm, "end": v(-11.23, 27.26) * mm});
            skLineSegment(sketch, "E8.1.4.0", {"start": v(-11.23, 41.26) * mm, "end": v(-11.23, 44.72) * mm});
            skLineSegment(sketch, "E8.1.4.1", {"start": v(-11.23, 44.72) * mm, "end": v(-8.23, 46.46) * mm});
            skLineSegment(sketch, "E8.1.4.2", {"start": v(-8.23, 46.46) * mm, "end": v(-5.23, 44.72) * mm});
            skLineSegment(sketch, "E8.1.4.3", {"start": v(-5.23, 44.72) * mm, "end": v(-5.23, 41.26) * mm});
            skLineSegment(sketch, "E8.1.4.4", {"start": v(-5.23, 41.26) * mm, "end": v(-8.23, 39.53) * mm});
            skLineSegment(sketch, "E8.1.4.5", {"start": v(-8.23, 39.53) * mm, "end": v(-11.23, 41.26) * mm});
            skLineSegment(sketch, "E8.1.5.0", {"start": v(-11.23, 55.26) * mm, "end": v(-11.23, 58.72) * mm});
            skLineSegment(sketch, "E8.1.5.1", {"start": v(-11.23, 58.72) * mm, "end": v(-8.23, 60.46) * mm});
            skLineSegment(sketch, "E8.1.5.2", {"start": v(-8.23, 60.46) * mm, "end": v(-5.23, 58.72) * mm});
            skLineSegment(sketch, "E8.1.5.3", {"start": v(-5.23, 58.72) * mm, "end": v(-5.23, 55.26) * mm});
            skLineSegment(sketch, "E8.1.5.4", {"start": v(-5.23, 55.26) * mm, "end": v(-8.23, 53.53) * mm});
            skLineSegment(sketch, "E8.1.5.5", {"start": v(-8.23, 53.53) * mm, "end": v(-11.23, 55.26) * mm});
            skLineSegment(sketch, "E8.2.0.0", {"start": v(-3.23, -14.74) * mm, "end": v(-3.23, -11.28) * mm});
            skLineSegment(sketch, "E8.2.0.1", {"start": v(-3.23, -11.28) * mm, "end": v(-0.23, -9.54) * mm});
            skLineSegment(sketch, "E8.2.0.2", {"start": v(-0.23, -9.54) * mm, "end": v(2.77, -11.28) * mm});
            skLineSegment(sketch, "E8.2.0.3", {"start": v(2.77, -11.28) * mm, "end": v(2.77, -14.74) * mm});
            skLineSegment(sketch, "E8.2.0.4", {"start": v(2.77, -14.74) * mm, "end": v(-0.23, -16.47) * mm});
            skLineSegment(sketch, "E8.2.0.5", {"start": v(-0.23, -16.47) * mm, "end": v(-3.23, -14.74) * mm});
            skLineSegment(sketch, "E8.2.1.0", {"start": v(-3.23, -0.74) * mm, "end": v(-3.23, 2.72) * mm});
            skLineSegment(sketch, "E8.2.1.1", {"start": v(-3.23, 2.72) * mm, "end": v(-0.23, 4.46) * mm});
            skLineSegment(sketch, "E8.2.1.2", {"start": v(-0.23, 4.46) * mm, "end": v(2.77, 2.72) * mm});
            skLineSegment(sketch, "E8.2.1.3", {"start": v(2.77, 2.72) * mm, "end": v(2.77, -0.74) * mm});
            skLineSegment(sketch, "E8.2.1.4", {"start": v(2.77, -0.74) * mm, "end": v(-0.23, -2.47) * mm});
            skLineSegment(sketch, "E8.2.1.5", {"start": v(-0.23, -2.47) * mm, "end": v(-3.23, -0.74) * mm});
            skLineSegment(sketch, "E8.2.2.0", {"start": v(-3.23, 13.26) * mm, "end": v(-3.23, 16.72) * mm});
            skLineSegment(sketch, "E8.2.2.1", {"start": v(-3.23, 16.72) * mm, "end": v(-0.23, 18.46) * mm});
            skLineSegment(sketch, "E8.2.2.2", {"start": v(-0.23, 18.46) * mm, "end": v(2.77, 16.72) * mm});
            skLineSegment(sketch, "E8.2.2.3", {"start": v(2.77, 16.72) * mm, "end": v(2.77, 13.26) * mm});
            skLineSegment(sketch, "E8.2.2.4", {"start": v(2.77, 13.26) * mm, "end": v(-0.23, 11.53) * mm});
            skLineSegment(sketch, "E8.2.2.5", {"start": v(-0.23, 11.53) * mm, "end": v(-3.23, 13.26) * mm});
            skLineSegment(sketch, "E8.2.3.0", {"start": v(-3.23, 27.26) * mm, "end": v(-3.23, 30.72) * mm});
            skLineSegment(sketch, "E8.2.3.1", {"start": v(-3.23, 30.72) * mm, "end": v(-0.23, 32.46) * mm});
            skLineSegment(sketch, "E8.2.3.2", {"start": v(-0.23, 32.46) * mm, "end": v(2.77, 30.72) * mm});
            skLineSegment(sketch, "E8.2.3.3", {"start": v(2.77, 30.72) * mm, "end": v(2.77, 27.26) * mm});
            skLineSegment(sketch, "E8.2.3.4", {"start": v(2.77, 27.26) * mm, "end": v(-0.23, 25.53) * mm});
            skLineSegment(sketch, "E8.2.3.5", {"start": v(-0.23, 25.53) * mm, "end": v(-3.23, 27.26) * mm});
            skLineSegment(sketch, "E8.2.4.0", {"start": v(-3.23, 41.26) * mm, "end": v(-3.23, 44.72) * mm});
            skLineSegment(sketch, "E8.2.4.1", {"start": v(-3.23, 44.72) * mm, "end": v(-0.23, 46.46) * mm});
            skLineSegment(sketch, "E8.2.4.2", {"start": v(-0.23, 46.46) * mm, "end": v(2.77, 44.72) * mm});
            skLineSegment(sketch, "E8.2.4.3", {"start": v(2.77, 44.72) * mm, "end": v(2.77, 41.26) * mm});
            skLineSegment(sketch, "E8.2.4.4", {"start": v(2.77, 41.26) * mm, "end": v(-0.23, 39.53) * mm});
            skLineSegment(sketch, "E8.2.4.5", {"start": v(-0.23, 39.53) * mm, "end": v(-3.23, 41.26) * mm});
            skLineSegment(sketch, "E8.2.5.0", {"start": v(-3.23, 55.26) * mm, "end": v(-3.23, 58.72) * mm});
            skLineSegment(sketch, "E8.2.5.1", {"start": v(-3.23, 58.72) * mm, "end": v(-0.23, 60.46) * mm});
            skLineSegment(sketch, "E8.2.5.2", {"start": v(-0.23, 60.46) * mm, "end": v(2.77, 58.72) * mm});
            skLineSegment(sketch, "E8.2.5.3", {"start": v(2.77, 58.72) * mm, "end": v(2.77, 55.26) * mm});
            skLineSegment(sketch, "E8.2.5.4", {"start": v(2.77, 55.26) * mm, "end": v(-0.23, 53.53) * mm});
            skLineSegment(sketch, "E8.2.5.5", {"start": v(-0.23, 53.53) * mm, "end": v(-3.23, 55.26) * mm});
            skLineSegment(sketch, "E8.3.0.0", {"start": v(4.77, -14.74) * mm, "end": v(4.77, -11.28) * mm});
            skLineSegment(sketch, "E8.3.0.1", {"start": v(4.77, -11.28) * mm, "end": v(7.77, -9.54) * mm});
            skLineSegment(sketch, "E8.3.0.2", {"start": v(7.77, -9.54) * mm, "end": v(10.77, -11.28) * mm});
            skLineSegment(sketch, "E8.3.0.3", {"start": v(10.77, -11.28) * mm, "end": v(10.77, -14.74) * mm});
            skLineSegment(sketch, "E8.3.0.4", {"start": v(10.77, -14.74) * mm, "end": v(7.77, -16.47) * mm});
            skLineSegment(sketch, "E8.3.0.5", {"start": v(7.77, -16.47) * mm, "end": v(4.77, -14.74) * mm});
            skLineSegment(sketch, "E8.3.1.0", {"start": v(4.77, -0.74) * mm, "end": v(4.77, 2.72) * mm});
            skLineSegment(sketch, "E8.3.1.1", {"start": v(4.77, 2.72) * mm, "end": v(7.77, 4.46) * mm});
            skLineSegment(sketch, "E8.3.1.2", {"start": v(7.77, 4.46) * mm, "end": v(10.77, 2.72) * mm});
            skLineSegment(sketch, "E8.3.1.3", {"start": v(10.77, 2.72) * mm, "end": v(10.77, -0.74) * mm});
            skLineSegment(sketch, "E8.3.1.4", {"start": v(10.77, -0.74) * mm, "end": v(7.77, -2.47) * mm});
            skLineSegment(sketch, "E8.3.1.5", {"start": v(7.77, -2.47) * mm, "end": v(4.77, -0.74) * mm});
            skLineSegment(sketch, "E8.3.2.0", {"start": v(4.77, 13.26) * mm, "end": v(4.77, 16.72) * mm});
            skLineSegment(sketch, "E8.3.2.1", {"start": v(4.77, 16.72) * mm, "end": v(7.77, 18.46) * mm});
            skLineSegment(sketch, "E8.3.2.2", {"start": v(7.77, 18.46) * mm, "end": v(10.77, 16.72) * mm});
            skLineSegment(sketch, "E8.3.2.3", {"start": v(10.77, 16.72) * mm, "end": v(10.77, 13.26) * mm});
            skLineSegment(sketch, "E8.3.2.4", {"start": v(10.77, 13.26) * mm, "end": v(7.77, 11.53) * mm});
            skLineSegment(sketch, "E8.3.2.5", {"start": v(7.77, 11.53) * mm, "end": v(4.77, 13.26) * mm});
            skLineSegment(sketch, "E8.3.3.0", {"start": v(4.77, 27.26) * mm, "end": v(4.77, 30.72) * mm});
            skLineSegment(sketch, "E8.3.3.1", {"start": v(4.77, 30.72) * mm, "end": v(7.77, 32.46) * mm});
            skLineSegment(sketch, "E8.3.3.2", {"start": v(7.77, 32.46) * mm, "end": v(10.77, 30.72) * mm});
            skLineSegment(sketch, "E8.3.3.3", {"start": v(10.77, 30.72) * mm, "end": v(10.77, 27.26) * mm});
            skLineSegment(sketch, "E8.3.3.4", {"start": v(10.77, 27.26) * mm, "end": v(7.77, 25.53) * mm});
            skLineSegment(sketch, "E8.3.3.5", {"start": v(7.77, 25.53) * mm, "end": v(4.77, 27.26) * mm});
            skLineSegment(sketch, "E8.3.4.0", {"start": v(4.77, 41.26) * mm, "end": v(4.77, 44.72) * mm});
            skLineSegment(sketch, "E8.3.4.1", {"start": v(4.77, 44.72) * mm, "end": v(7.77, 46.46) * mm});
            skLineSegment(sketch, "E8.3.4.2", {"start": v(7.77, 46.46) * mm, "end": v(10.77, 44.72) * mm});
            skLineSegment(sketch, "E8.3.4.3", {"start": v(10.77, 44.72) * mm, "end": v(10.77, 41.26) * mm});
            skLineSegment(sketch, "E8.3.4.4", {"start": v(10.77, 41.26) * mm, "end": v(7.77, 39.53) * mm});
            skLineSegment(sketch, "E8.3.4.5", {"start": v(7.77, 39.53) * mm, "end": v(4.77, 41.26) * mm});
            skLineSegment(sketch, "E8.3.5.0", {"start": v(4.77, 55.26) * mm, "end": v(4.77, 58.72) * mm});
            skLineSegment(sketch, "E8.3.5.1", {"start": v(4.77, 58.72) * mm, "end": v(7.77, 60.46) * mm});
            skLineSegment(sketch, "E8.3.5.2", {"start": v(7.77, 60.46) * mm, "end": v(10.77, 58.72) * mm});
            skLineSegment(sketch, "E8.3.5.3", {"start": v(10.77, 58.72) * mm, "end": v(10.77, 55.26) * mm});
            skLineSegment(sketch, "E8.3.5.4", {"start": v(10.77, 55.26) * mm, "end": v(7.77, 53.53) * mm});
            skLineSegment(sketch, "E8.3.5.5", {"start": v(7.77, 53.53) * mm, "end": v(4.77, 55.26) * mm});
            skLineSegment(sketch, "E8.4.0.0", {"start": v(12.77, -14.74) * mm, "end": v(12.77, -11.28) * mm});
            skLineSegment(sketch, "E8.4.0.1", {"start": v(12.77, -11.28) * mm, "end": v(15.77, -9.54) * mm});
            skLineSegment(sketch, "E8.4.0.2", {"start": v(15.77, -9.54) * mm, "end": v(18.77, -11.28) * mm});
            skLineSegment(sketch, "E8.4.0.3", {"start": v(18.77, -11.28) * mm, "end": v(18.77, -14.74) * mm});
            skLineSegment(sketch, "E8.4.0.4", {"start": v(18.77, -14.74) * mm, "end": v(15.77, -16.47) * mm});
            skLineSegment(sketch, "E8.4.0.5", {"start": v(15.77, -16.47) * mm, "end": v(12.77, -14.74) * mm});
            skLineSegment(sketch, "E8.4.1.0", {"start": v(12.77, -0.74) * mm, "end": v(12.77, 2.72) * mm});
            skLineSegment(sketch, "E8.4.1.1", {"start": v(12.77, 2.72) * mm, "end": v(15.77, 4.46) * mm});
            skLineSegment(sketch, "E8.4.1.2", {"start": v(15.77, 4.46) * mm, "end": v(18.77, 2.72) * mm});
            skLineSegment(sketch, "E8.4.1.3", {"start": v(18.77, 2.72) * mm, "end": v(18.77, -0.74) * mm});
            skLineSegment(sketch, "E8.4.1.4", {"start": v(18.77, -0.74) * mm, "end": v(15.77, -2.47) * mm});
            skLineSegment(sketch, "E8.4.1.5", {"start": v(15.77, -2.47) * mm, "end": v(12.77, -0.74) * mm});
            skLineSegment(sketch, "E8.4.2.0", {"start": v(12.77, 13.26) * mm, "end": v(12.77, 16.72) * mm});
            skLineSegment(sketch, "E8.4.2.1", {"start": v(12.77, 16.72) * mm, "end": v(15.77, 18.46) * mm});
            skLineSegment(sketch, "E8.4.2.2", {"start": v(15.77, 18.46) * mm, "end": v(18.77, 16.72) * mm});
            skLineSegment(sketch, "E8.4.2.3", {"start": v(18.77, 16.72) * mm, "end": v(18.77, 13.26) * mm});
            skLineSegment(sketch, "E8.4.2.4", {"start": v(18.77, 13.26) * mm, "end": v(15.77, 11.53) * mm});
            skLineSegment(sketch, "E8.4.2.5", {"start": v(15.77, 11.53) * mm, "end": v(12.77, 13.26) * mm});
            skLineSegment(sketch, "E8.4.3.0", {"start": v(12.77, 27.26) * mm, "end": v(12.77, 30.72) * mm});
            skLineSegment(sketch, "E8.4.3.1", {"start": v(12.77, 30.72) * mm, "end": v(15.77, 32.46) * mm});
            skLineSegment(sketch, "E8.4.3.2", {"start": v(15.77, 32.46) * mm, "end": v(18.77, 30.72) * mm});
            skLineSegment(sketch, "E8.4.3.3", {"start": v(18.77, 30.72) * mm, "end": v(18.77, 27.26) * mm});
            skLineSegment(sketch, "E8.4.3.4", {"start": v(18.77, 27.26) * mm, "end": v(15.77, 25.53) * mm});
            skLineSegment(sketch, "E8.4.3.5", {"start": v(15.77, 25.53) * mm, "end": v(12.77, 27.26) * mm});
            skLineSegment(sketch, "E8.4.4.0", {"start": v(12.77, 41.26) * mm, "end": v(12.77, 44.72) * mm});
            skLineSegment(sketch, "E8.4.4.1", {"start": v(12.77, 44.72) * mm, "end": v(15.77, 46.46) * mm});
            skLineSegment(sketch, "E8.4.4.2", {"start": v(15.77, 46.46) * mm, "end": v(18.77, 44.72) * mm});
            skLineSegment(sketch, "E8.4.4.3", {"start": v(18.77, 44.72) * mm, "end": v(18.77, 41.26) * mm});
            skLineSegment(sketch, "E8.4.4.4", {"start": v(18.77, 41.26) * mm, "end": v(15.77, 39.53) * mm});
            skLineSegment(sketch, "E8.4.4.5", {"start": v(15.77, 39.53) * mm, "end": v(12.77, 41.26) * mm});
            skLineSegment(sketch, "E8.4.5.0", {"start": v(12.77, 55.26) * mm, "end": v(12.77, 58.72) * mm});
            skLineSegment(sketch, "E8.4.5.1", {"start": v(12.77, 58.72) * mm, "end": v(15.77, 60.46) * mm});
            skLineSegment(sketch, "E8.4.5.2", {"start": v(15.77, 60.46) * mm, "end": v(18.77, 58.72) * mm});
            skLineSegment(sketch, "E8.4.5.3", {"start": v(18.77, 58.72) * mm, "end": v(18.77, 55.26) * mm});
            skLineSegment(sketch, "E8.4.5.4", {"start": v(18.77, 55.26) * mm, "end": v(15.77, 53.53) * mm});
            skLineSegment(sketch, "E8.4.5.5", {"start": v(15.77, 53.53) * mm, "end": v(12.77, 55.26) * mm});
            skLineSegment(sketch, "E8.5.0.0", {"start": v(20.77, -14.74) * mm, "end": v(20.77, -11.28) * mm});
            skLineSegment(sketch, "E8.5.0.1", {"start": v(20.77, -11.28) * mm, "end": v(23.77, -9.54) * mm});
            skLineSegment(sketch, "E8.5.0.2", {"start": v(23.77, -9.54) * mm, "end": v(26.77, -11.28) * mm});
            skLineSegment(sketch, "E8.5.0.3", {"start": v(26.77, -11.28) * mm, "end": v(26.77, -14.74) * mm});
            skLineSegment(sketch, "E8.5.0.4", {"start": v(26.77, -14.74) * mm, "end": v(23.77, -16.47) * mm});
            skLineSegment(sketch, "E8.5.0.5", {"start": v(23.77, -16.47) * mm, "end": v(20.77, -14.74) * mm});
            skLineSegment(sketch, "E8.5.1.0", {"start": v(20.77, -0.74) * mm, "end": v(20.77, 2.72) * mm});
            skLineSegment(sketch, "E8.5.1.1", {"start": v(20.77, 2.72) * mm, "end": v(23.77, 4.46) * mm});
            skLineSegment(sketch, "E8.5.1.2", {"start": v(23.77, 4.46) * mm, "end": v(26.77, 2.72) * mm});
            skLineSegment(sketch, "E8.5.1.3", {"start": v(26.77, 2.72) * mm, "end": v(26.77, -0.74) * mm});
            skLineSegment(sketch, "E8.5.1.4", {"start": v(26.77, -0.74) * mm, "end": v(23.77, -2.47) * mm});
            skLineSegment(sketch, "E8.5.1.5", {"start": v(23.77, -2.47) * mm, "end": v(20.77, -0.74) * mm});
            skLineSegment(sketch, "E8.5.2.0", {"start": v(20.77, 13.26) * mm, "end": v(20.77, 16.72) * mm});
            skLineSegment(sketch, "E8.5.2.1", {"start": v(20.77, 16.72) * mm, "end": v(23.77, 18.46) * mm});
            skLineSegment(sketch, "E8.5.2.2", {"start": v(23.77, 18.46) * mm, "end": v(26.77, 16.72) * mm});
            skLineSegment(sketch, "E8.5.2.3", {"start": v(26.77, 16.72) * mm, "end": v(26.77, 13.26) * mm});
            skLineSegment(sketch, "E8.5.2.4", {"start": v(26.77, 13.26) * mm, "end": v(23.77, 11.53) * mm});
            skLineSegment(sketch, "E8.5.2.5", {"start": v(23.77, 11.53) * mm, "end": v(20.77, 13.26) * mm});
            skLineSegment(sketch, "E8.5.3.0", {"start": v(20.77, 27.26) * mm, "end": v(20.77, 30.72) * mm});
            skLineSegment(sketch, "E8.5.3.1", {"start": v(20.77, 30.72) * mm, "end": v(23.77, 32.46) * mm});
            skLineSegment(sketch, "E8.5.3.2", {"start": v(23.77, 32.46) * mm, "end": v(26.77, 30.72) * mm});
            skLineSegment(sketch, "E8.5.3.3", {"start": v(26.77, 30.72) * mm, "end": v(26.77, 27.26) * mm});
            skLineSegment(sketch, "E8.5.3.4", {"start": v(26.77, 27.26) * mm, "end": v(23.77, 25.53) * mm});
            skLineSegment(sketch, "E8.5.3.5", {"start": v(23.77, 25.53) * mm, "end": v(20.77, 27.26) * mm});
            skLineSegment(sketch, "E8.5.4.0", {"start": v(20.77, 41.26) * mm, "end": v(20.77, 44.72) * mm});
            skLineSegment(sketch, "E8.5.4.1", {"start": v(20.77, 44.72) * mm, "end": v(23.77, 46.46) * mm});
            skLineSegment(sketch, "E8.5.4.2", {"start": v(23.77, 46.46) * mm, "end": v(26.77, 44.72) * mm});
            skLineSegment(sketch, "E8.5.4.3", {"start": v(26.77, 44.72) * mm, "end": v(26.77, 41.26) * mm});
            skLineSegment(sketch, "E8.5.4.4", {"start": v(26.77, 41.26) * mm, "end": v(23.77, 39.53) * mm});
            skLineSegment(sketch, "E8.5.4.5", {"start": v(23.77, 39.53) * mm, "end": v(20.77, 41.26) * mm});
            skLineSegment(sketch, "E8.5.5.0", {"start": v(20.77, 55.26) * mm, "end": v(20.77, 58.72) * mm});
            skLineSegment(sketch, "E8.5.5.1", {"start": v(20.77, 58.72) * mm, "end": v(23.77, 60.46) * mm});
            skLineSegment(sketch, "E8.5.5.2", {"start": v(23.77, 60.46) * mm, "end": v(26.77, 58.72) * mm});
            skLineSegment(sketch, "E8.5.5.3", {"start": v(26.77, 58.72) * mm, "end": v(26.77, 55.26) * mm});
            skLineSegment(sketch, "E8.5.5.4", {"start": v(26.77, 55.26) * mm, "end": v(23.77, 53.53) * mm});
            skLineSegment(sketch, "E8.5.5.5", {"start": v(23.77, 53.53) * mm, "end": v(20.77, 55.26) * mm});
            skLineSegment(sketch, "E8.6.0.0", {"start": v(28.77, -14.74) * mm, "end": v(28.77, -11.28) * mm});
            skLineSegment(sketch, "E8.6.0.1", {"start": v(28.77, -11.28) * mm, "end": v(31.77, -9.54) * mm});
            skLineSegment(sketch, "E8.6.0.2", {"start": v(31.77, -9.54) * mm, "end": v(34.77, -11.28) * mm});
            skLineSegment(sketch, "E8.6.0.3", {"start": v(34.77, -11.28) * mm, "end": v(34.77, -14.74) * mm});
            skLineSegment(sketch, "E8.6.0.4", {"start": v(34.77, -14.74) * mm, "end": v(31.77, -16.47) * mm});
            skLineSegment(sketch, "E8.6.0.5", {"start": v(31.77, -16.47) * mm, "end": v(28.77, -14.74) * mm});
            skLineSegment(sketch, "E8.6.1.0", {"start": v(28.77, -0.74) * mm, "end": v(28.77, 2.72) * mm});
            skLineSegment(sketch, "E8.6.1.1", {"start": v(28.77, 2.72) * mm, "end": v(31.77, 4.46) * mm});
            skLineSegment(sketch, "E8.6.1.2", {"start": v(31.77, 4.46) * mm, "end": v(34.77, 2.72) * mm});
            skLineSegment(sketch, "E8.6.1.3", {"start": v(34.77, 2.72) * mm, "end": v(34.77, -0.74) * mm});
            skLineSegment(sketch, "E8.6.1.4", {"start": v(34.77, -0.74) * mm, "end": v(31.77, -2.47) * mm});
            skLineSegment(sketch, "E8.6.1.5", {"start": v(31.77, -2.47) * mm, "end": v(28.77, -0.74) * mm});
            skLineSegment(sketch, "E8.6.2.0", {"start": v(28.77, 13.26) * mm, "end": v(28.77, 16.72) * mm});
            skLineSegment(sketch, "E8.6.2.1", {"start": v(28.77, 16.72) * mm, "end": v(31.77, 18.46) * mm});
            skLineSegment(sketch, "E8.6.2.2", {"start": v(31.77, 18.46) * mm, "end": v(34.77, 16.72) * mm});
            skLineSegment(sketch, "E8.6.2.3", {"start": v(34.77, 16.72) * mm, "end": v(34.77, 13.26) * mm});
            skLineSegment(sketch, "E8.6.2.4", {"start": v(34.77, 13.26) * mm, "end": v(31.77, 11.53) * mm});
            skLineSegment(sketch, "E8.6.2.5", {"start": v(31.77, 11.53) * mm, "end": v(28.77, 13.26) * mm});
            skLineSegment(sketch, "E8.6.3.0", {"start": v(28.77, 27.26) * mm, "end": v(28.77, 30.72) * mm});
            skLineSegment(sketch, "E8.6.3.1", {"start": v(28.77, 30.72) * mm, "end": v(31.77, 32.46) * mm});
            skLineSegment(sketch, "E8.6.3.2", {"start": v(31.77, 32.46) * mm, "end": v(34.77, 30.72) * mm});
            skLineSegment(sketch, "E8.6.3.3", {"start": v(34.77, 30.72) * mm, "end": v(34.77, 27.26) * mm});
            skLineSegment(sketch, "E8.6.3.4", {"start": v(34.77, 27.26) * mm, "end": v(31.77, 25.53) * mm});
            skLineSegment(sketch, "E8.6.3.5", {"start": v(31.77, 25.53) * mm, "end": v(28.77, 27.26) * mm});
            skLineSegment(sketch, "E8.6.4.0", {"start": v(28.77, 41.26) * mm, "end": v(28.77, 44.72) * mm});
            skLineSegment(sketch, "E8.6.4.1", {"start": v(28.77, 44.72) * mm, "end": v(31.77, 46.46) * mm});
            skLineSegment(sketch, "E8.6.4.2", {"start": v(31.77, 46.46) * mm, "end": v(34.77, 44.72) * mm});
            skLineSegment(sketch, "E8.6.4.3", {"start": v(34.77, 44.72) * mm, "end": v(34.77, 41.26) * mm});
            skLineSegment(sketch, "E8.6.4.4", {"start": v(34.77, 41.26) * mm, "end": v(31.77, 39.53) * mm});
            skLineSegment(sketch, "E8.6.4.5", {"start": v(31.77, 39.53) * mm, "end": v(28.77, 41.26) * mm});
            skLineSegment(sketch, "E8.6.5.0", {"start": v(28.77, 55.26) * mm, "end": v(28.77, 58.72) * mm});
            skLineSegment(sketch, "E8.6.5.1", {"start": v(28.77, 58.72) * mm, "end": v(31.77, 60.46) * mm});
            skLineSegment(sketch, "E8.6.5.2", {"start": v(31.77, 60.46) * mm, "end": v(34.77, 58.72) * mm});
            skLineSegment(sketch, "E8.6.5.3", {"start": v(34.77, 58.72) * mm, "end": v(34.77, 55.26) * mm});
            skLineSegment(sketch, "E8.6.5.4", {"start": v(34.77, 55.26) * mm, "end": v(31.77, 53.53) * mm});
            skLineSegment(sketch, "E8.6.5.5", {"start": v(31.77, 53.53) * mm, "end": v(28.77, 55.26) * mm});
            skLineSegment(sketch, "E8.7.0.0", {"start": v(36.77, -14.74) * mm, "end": v(36.77, -11.28) * mm});
            skLineSegment(sketch, "E8.7.0.1", {"start": v(36.77, -11.28) * mm, "end": v(39.77, -9.54) * mm});
            skLineSegment(sketch, "E8.7.0.2", {"start": v(39.77, -9.54) * mm, "end": v(42.77, -11.28) * mm});
            skLineSegment(sketch, "E8.7.0.3", {"start": v(42.77, -11.28) * mm, "end": v(42.77, -14.74) * mm});
            skLineSegment(sketch, "E8.7.0.4", {"start": v(42.77, -14.74) * mm, "end": v(39.77, -16.47) * mm});
            skLineSegment(sketch, "E8.7.0.5", {"start": v(39.77, -16.47) * mm, "end": v(36.77, -14.74) * mm});
            skLineSegment(sketch, "E8.7.1.0", {"start": v(36.77, -0.74) * mm, "end": v(36.77, 2.72) * mm});
            skLineSegment(sketch, "E8.7.1.1", {"start": v(36.77, 2.72) * mm, "end": v(39.77, 4.46) * mm});
            skLineSegment(sketch, "E8.7.1.2", {"start": v(39.77, 4.46) * mm, "end": v(42.77, 2.72) * mm});
            skLineSegment(sketch, "E8.7.1.3", {"start": v(42.77, 2.72) * mm, "end": v(42.77, -0.74) * mm});
            skLineSegment(sketch, "E8.7.1.4", {"start": v(42.77, -0.74) * mm, "end": v(39.77, -2.47) * mm});
            skLineSegment(sketch, "E8.7.1.5", {"start": v(39.77, -2.47) * mm, "end": v(36.77, -0.74) * mm});
            skLineSegment(sketch, "E8.7.2.0", {"start": v(36.77, 13.26) * mm, "end": v(36.77, 16.72) * mm});
            skLineSegment(sketch, "E8.7.2.1", {"start": v(36.77, 16.72) * mm, "end": v(39.77, 18.46) * mm});
            skLineSegment(sketch, "E8.7.2.2", {"start": v(39.77, 18.46) * mm, "end": v(42.77, 16.72) * mm});
            skLineSegment(sketch, "E8.7.2.3", {"start": v(42.77, 16.72) * mm, "end": v(42.77, 13.26) * mm});
            skLineSegment(sketch, "E8.7.2.4", {"start": v(42.77, 13.26) * mm, "end": v(39.77, 11.53) * mm});
            skLineSegment(sketch, "E8.7.2.5", {"start": v(39.77, 11.53) * mm, "end": v(36.77, 13.26) * mm});
            skLineSegment(sketch, "E8.7.3.0", {"start": v(36.77, 27.26) * mm, "end": v(36.77, 30.72) * mm});
            skLineSegment(sketch, "E8.7.3.1", {"start": v(36.77, 30.72) * mm, "end": v(39.77, 32.46) * mm});
            skLineSegment(sketch, "E8.7.3.2", {"start": v(39.77, 32.46) * mm, "end": v(42.77, 30.72) * mm});
            skLineSegment(sketch, "E8.7.3.3", {"start": v(42.77, 30.72) * mm, "end": v(42.77, 27.26) * mm});
            skLineSegment(sketch, "E8.7.3.4", {"start": v(42.77, 27.26) * mm, "end": v(39.77, 25.53) * mm});
            skLineSegment(sketch, "E8.7.3.5", {"start": v(39.77, 25.53) * mm, "end": v(36.77, 27.26) * mm});
            skLineSegment(sketch, "E8.7.4.0", {"start": v(36.77, 41.26) * mm, "end": v(36.77, 44.72) * mm});
            skLineSegment(sketch, "E8.7.4.1", {"start": v(36.77, 44.72) * mm, "end": v(39.77, 46.46) * mm});
            skLineSegment(sketch, "E8.7.4.2", {"start": v(39.77, 46.46) * mm, "end": v(42.77, 44.72) * mm});
            skLineSegment(sketch, "E8.7.4.3", {"start": v(42.77, 44.72) * mm, "end": v(42.77, 41.26) * mm});
            skLineSegment(sketch, "E8.7.4.4", {"start": v(42.77, 41.26) * mm, "end": v(39.77, 39.53) * mm});
            skLineSegment(sketch, "E8.7.4.5", {"start": v(39.77, 39.53) * mm, "end": v(36.77, 41.26) * mm});
            skLineSegment(sketch, "E8.7.5.0", {"start": v(36.77, 55.26) * mm, "end": v(36.77, 58.72) * mm});
            skLineSegment(sketch, "E8.7.5.1", {"start": v(36.77, 58.72) * mm, "end": v(39.77, 60.46) * mm});
            skLineSegment(sketch, "E8.7.5.2", {"start": v(39.77, 60.46) * mm, "end": v(42.77, 58.72) * mm});
            skLineSegment(sketch, "E8.7.5.3", {"start": v(42.77, 58.72) * mm, "end": v(42.77, 55.26) * mm});
            skLineSegment(sketch, "E8.7.5.4", {"start": v(42.77, 55.26) * mm, "end": v(39.77, 53.53) * mm});
            skLineSegment(sketch, "E8.7.5.5", {"start": v(39.77, 53.53) * mm, "end": v(36.77, 55.26) * mm});
            skLineSegment(sketch, "E8.8.0.0", {"start": v(44.77, -14.74) * mm, "end": v(44.77, -11.28) * mm});
            skLineSegment(sketch, "E8.8.0.1", {"start": v(44.77, -11.28) * mm, "end": v(47.77, -9.54) * mm});
            skLineSegment(sketch, "E8.8.0.2", {"start": v(47.77, -9.54) * mm, "end": v(50.77, -11.28) * mm});
            skLineSegment(sketch, "E8.8.0.3", {"start": v(50.77, -11.28) * mm, "end": v(50.77, -14.74) * mm});
            skLineSegment(sketch, "E8.8.0.4", {"start": v(50.77, -14.74) * mm, "end": v(47.77, -16.47) * mm});
            skLineSegment(sketch, "E8.8.0.5", {"start": v(47.77, -16.47) * mm, "end": v(44.77, -14.74) * mm});
            skLineSegment(sketch, "E8.8.1.0", {"start": v(44.77, -0.74) * mm, "end": v(44.77, 2.72) * mm});
            skLineSegment(sketch, "E8.8.1.1", {"start": v(44.77, 2.72) * mm, "end": v(47.77, 4.46) * mm});
            skLineSegment(sketch, "E8.8.1.2", {"start": v(47.77, 4.46) * mm, "end": v(50.77, 2.72) * mm});
            skLineSegment(sketch, "E8.8.1.3", {"start": v(50.77, 2.72) * mm, "end": v(50.77, -0.74) * mm});
            skLineSegment(sketch, "E8.8.1.4", {"start": v(50.77, -0.74) * mm, "end": v(47.77, -2.47) * mm});
            skLineSegment(sketch, "E8.8.1.5", {"start": v(47.77, -2.47) * mm, "end": v(44.77, -0.74) * mm});
            skLineSegment(sketch, "E8.8.2.0", {"start": v(44.77, 13.26) * mm, "end": v(44.77, 16.72) * mm});
            skLineSegment(sketch, "E8.8.2.1", {"start": v(44.77, 16.72) * mm, "end": v(47.77, 18.46) * mm});
            skLineSegment(sketch, "E8.8.2.2", {"start": v(47.77, 18.46) * mm, "end": v(50.77, 16.72) * mm});
            skLineSegment(sketch, "E8.8.2.3", {"start": v(50.77, 16.72) * mm, "end": v(50.77, 13.26) * mm});
            skLineSegment(sketch, "E8.8.2.4", {"start": v(50.77, 13.26) * mm, "end": v(47.77, 11.53) * mm});
            skLineSegment(sketch, "E8.8.2.5", {"start": v(47.77, 11.53) * mm, "end": v(44.77, 13.26) * mm});
            skLineSegment(sketch, "E8.8.3.0", {"start": v(44.77, 27.26) * mm, "end": v(44.77, 30.72) * mm});
            skLineSegment(sketch, "E8.8.3.1", {"start": v(44.77, 30.72) * mm, "end": v(47.77, 32.46) * mm});
            skLineSegment(sketch, "E8.8.3.2", {"start": v(47.77, 32.46) * mm, "end": v(50.77, 30.72) * mm});
            skLineSegment(sketch, "E8.8.3.3", {"start": v(50.77, 30.72) * mm, "end": v(50.77, 27.26) * mm});
            skLineSegment(sketch, "E8.8.3.4", {"start": v(50.77, 27.26) * mm, "end": v(47.77, 25.53) * mm});
            skLineSegment(sketch, "E8.8.3.5", {"start": v(47.77, 25.53) * mm, "end": v(44.77, 27.26) * mm});
            skLineSegment(sketch, "E8.8.4.0", {"start": v(44.77, 41.26) * mm, "end": v(44.77, 44.72) * mm});
            skLineSegment(sketch, "E8.8.4.1", {"start": v(44.77, 44.72) * mm, "end": v(47.77, 46.46) * mm});
            skLineSegment(sketch, "E8.8.4.2", {"start": v(47.77, 46.46) * mm, "end": v(50.77, 44.72) * mm});
            skLineSegment(sketch, "E8.8.4.3", {"start": v(50.77, 44.72) * mm, "end": v(50.77, 41.26) * mm});
            skLineSegment(sketch, "E8.8.4.4", {"start": v(50.77, 41.26) * mm, "end": v(47.77, 39.53) * mm});
            skLineSegment(sketch, "E8.8.4.5", {"start": v(47.77, 39.53) * mm, "end": v(44.77, 41.26) * mm});
            skLineSegment(sketch, "E8.8.5.0", {"start": v(44.77, 55.26) * mm, "end": v(44.77, 58.72) * mm});
            skLineSegment(sketch, "E8.8.5.1", {"start": v(44.77, 58.72) * mm, "end": v(47.77, 60.46) * mm});
            skLineSegment(sketch, "E8.8.5.2", {"start": v(47.77, 60.46) * mm, "end": v(50.77, 58.72) * mm});
            skLineSegment(sketch, "E8.8.5.3", {"start": v(50.77, 58.72) * mm, "end": v(50.77, 55.26) * mm});
            skLineSegment(sketch, "E8.8.5.4", {"start": v(50.77, 55.26) * mm, "end": v(47.77, 53.53) * mm});
            skLineSegment(sketch, "E8.8.5.5", {"start": v(47.77, 53.53) * mm, "end": v(44.77, 55.26) * mm});
            skLineSegment(sketch, "E8.9.0.0", {"start": v(52.77, -14.74) * mm, "end": v(52.77, -11.28) * mm});
            skLineSegment(sketch, "E8.9.0.1", {"start": v(52.77, -11.28) * mm, "end": v(55.77, -9.54) * mm});
            skLineSegment(sketch, "E8.9.0.2", {"start": v(55.77, -9.54) * mm, "end": v(58.77, -11.28) * mm});
            skLineSegment(sketch, "E8.9.0.3", {"start": v(58.77, -11.28) * mm, "end": v(58.77, -14.74) * mm});
            skLineSegment(sketch, "E8.9.0.4", {"start": v(58.77, -14.74) * mm, "end": v(55.77, -16.47) * mm});
            skLineSegment(sketch, "E8.9.0.5", {"start": v(55.77, -16.47) * mm, "end": v(52.77, -14.74) * mm});
            skLineSegment(sketch, "E8.9.1.0", {"start": v(52.77, -0.74) * mm, "end": v(52.77, 2.72) * mm});
            skLineSegment(sketch, "E8.9.1.1", {"start": v(52.77, 2.72) * mm, "end": v(55.77, 4.46) * mm});
            skLineSegment(sketch, "E8.9.1.2", {"start": v(55.77, 4.46) * mm, "end": v(58.77, 2.72) * mm});
            skLineSegment(sketch, "E8.9.1.3", {"start": v(58.77, 2.72) * mm, "end": v(58.77, -0.74) * mm});
            skLineSegment(sketch, "E8.9.1.4", {"start": v(58.77, -0.74) * mm, "end": v(55.77, -2.47) * mm});
            skLineSegment(sketch, "E8.9.1.5", {"start": v(55.77, -2.47) * mm, "end": v(52.77, -0.74) * mm});
            skLineSegment(sketch, "E8.9.2.0", {"start": v(52.77, 13.26) * mm, "end": v(52.77, 16.72) * mm});
            skLineSegment(sketch, "E8.9.2.1", {"start": v(52.77, 16.72) * mm, "end": v(55.77, 18.46) * mm});
            skLineSegment(sketch, "E8.9.2.2", {"start": v(55.77, 18.46) * mm, "end": v(58.77, 16.72) * mm});
            skLineSegment(sketch, "E8.9.2.3", {"start": v(58.77, 16.72) * mm, "end": v(58.77, 13.26) * mm});
            skLineSegment(sketch, "E8.9.2.4", {"start": v(58.77, 13.26) * mm, "end": v(55.77, 11.53) * mm});
            skLineSegment(sketch, "E8.9.2.5", {"start": v(55.77, 11.53) * mm, "end": v(52.77, 13.26) * mm});
            skLineSegment(sketch, "E8.9.3.0", {"start": v(52.77, 27.26) * mm, "end": v(52.77, 30.72) * mm});
            skLineSegment(sketch, "E8.9.3.1", {"start": v(52.77, 30.72) * mm, "end": v(55.77, 32.46) * mm});
            skLineSegment(sketch, "E8.9.3.2", {"start": v(55.77, 32.46) * mm, "end": v(58.77, 30.72) * mm});
            skLineSegment(sketch, "E8.9.3.3", {"start": v(58.77, 30.72) * mm, "end": v(58.77, 27.26) * mm});
            skLineSegment(sketch, "E8.9.3.4", {"start": v(58.77, 27.26) * mm, "end": v(55.77, 25.53) * mm});
            skLineSegment(sketch, "E8.9.3.5", {"start": v(55.77, 25.53) * mm, "end": v(52.77, 27.26) * mm});
            skLineSegment(sketch, "E8.9.4.0", {"start": v(52.77, 41.26) * mm, "end": v(52.77, 44.72) * mm});
            skLineSegment(sketch, "E8.9.4.1", {"start": v(52.77, 44.72) * mm, "end": v(55.77, 46.46) * mm});
            skLineSegment(sketch, "E8.9.4.2", {"start": v(55.77, 46.46) * mm, "end": v(58.77, 44.72) * mm});
            skLineSegment(sketch, "E8.9.4.3", {"start": v(58.77, 44.72) * mm, "end": v(58.77, 41.26) * mm});
            skLineSegment(sketch, "E8.9.4.4", {"start": v(58.77, 41.26) * mm, "end": v(55.77, 39.53) * mm});
            skLineSegment(sketch, "E8.9.4.5", {"start": v(55.77, 39.53) * mm, "end": v(52.77, 41.26) * mm});
            skLineSegment(sketch, "E8.9.5.0", {"start": v(52.77, 55.26) * mm, "end": v(52.77, 58.72) * mm});
            skLineSegment(sketch, "E8.9.5.1", {"start": v(52.77, 58.72) * mm, "end": v(55.77, 60.46) * mm});
            skLineSegment(sketch, "E8.9.5.2", {"start": v(55.77, 60.46) * mm, "end": v(58.77, 58.72) * mm});
            skLineSegment(sketch, "E8.9.5.3", {"start": v(58.77, 58.72) * mm, "end": v(58.77, 55.26) * mm});
            skLineSegment(sketch, "E8.9.5.4", {"start": v(58.77, 55.26) * mm, "end": v(55.77, 53.53) * mm});
            skLineSegment(sketch, "E8.9.5.5", {"start": v(55.77, 53.53) * mm, "end": v(52.77, 55.26) * mm});
            skLineSegment(sketch, "E8.direction1", {"start": v(-19.23, -14.74) * mm, "end": v(-11.23, -14.74) * mm, "construction": true});
            skLineSegment(sketch, "E8.direction2", {"start": v(-19.23, -14.74) * mm, "end": v(-19.23, -0.74) * mm, "construction": true});
            skEllipse(sketch, "E9", {"center": v(0, 0) * mm, "majorRadius": 15.5 * mm, "minorRadius": 14.5 * mm, "majorAxis": v(-1, 0)});
            skSolve(sketch);
        }
        {
            var Q0;
            {var subQ55=sQuery(id+"F2.wireOp",EDGE,"E3.1.1.0");Q0=makeQuery(id+"F2.imprint","IMPRINT",FACE,{"disambiguationData":[TD([[makeQuery(id+"F2.imprint","IMPRINT",EDGE,{"derivedFrom":subQ55}),1.0]])]});}
            var Q1;
            {var subQ0=sQuery(id+"F2.wireOp",EDGE,"E9");var subQ1=sQuery(id+"F2.wireOp",EDGE,"E3.4.2.5");var subQ2=makeQuery(id+"F2.imprint","INTERSECT",VERTEX,{"derivedFrom":[subQ1,subQ0]});Q1=makeQuery(id+"F2.imprint","IMPRINT",FACE,{"disambiguationData":[TD([[makeQuery(id+"F2.imprint","IMPRINT",EDGE,{"disambiguationData":[TD([[subQ2,-1.0]])],"derivedFrom":subQ1}),1.0]])]});}
            var Q2;
            {var subQ0=sQuery(id+"F2.wireOp",EDGE,"E9");var subQ1=sQuery(id+"F2.wireOp",EDGE,"E8.3.2.0");var subQ2=makeQuery(id+"F2.imprint","INTERSECT",VERTEX,{"derivedFrom":[subQ1,subQ0]});Q2=makeQuery(id+"F2.imprint","IMPRINT",FACE,{"disambiguationData":[TD([[makeQuery(id+"F2.imprint","IMPRINT",EDGE,{"disambiguationData":[TD([[subQ2,-1.0]])],"derivedFrom":subQ1}),-1.0]])]});}
            var Q3;
            {var subQ0=sQuery(id+"F2.wireOp",EDGE,"E9");var subQ1=sQuery(id+"F2.wireOp",EDGE,"E8.2.2.3");var subQ2=makeQuery(id+"F2.imprint","INTERSECT",VERTEX,{"derivedFrom":[subQ1,subQ0]});Q3=makeQuery(id+"F2.imprint","IMPRINT",FACE,{"disambiguationData":[TD([[makeQuery(id+"F2.imprint","IMPRINT",EDGE,{"disambiguationData":[TD([[subQ2,1.0]])],"derivedFrom":subQ1}),1.0]])]});}
            var Q4;
            {var subQ0=sQuery(id+"F2.wireOp",EDGE,"E9");var subQ1=sQuery(id+"F2.wireOp",EDGE,"E8.2.2.0");var subQ2=makeQuery(id+"F2.imprint","INTERSECT",VERTEX,{"derivedFrom":[subQ1,subQ0]});Q4=makeQuery(id+"F2.imprint","IMPRINT",FACE,{"disambiguationData":[TD([[makeQuery(id+"F2.imprint","IMPRINT",EDGE,{"disambiguationData":[TD([[subQ2,-1.0]])],"derivedFrom":subQ1}),-1.0]])]});}
            var Q5;
            {var subQ0=sQuery(id+"F2.wireOp",EDGE,"E9");var subQ1=sQuery(id+"F2.wireOp",EDGE,"E8.1.2.3");var subQ2=makeQuery(id+"F2.imprint","INTERSECT",VERTEX,{"derivedFrom":[subQ1,subQ0]});Q5=makeQuery(id+"F2.imprint","IMPRINT",FACE,{"disambiguationData":[TD([[makeQuery(id+"F2.imprint","IMPRINT",EDGE,{"disambiguationData":[TD([[subQ2,1.0]])],"derivedFrom":subQ1}),1.0]])]});}
            var Q6;
            {var subQ0=sQuery(id+"F2.wireOp",EDGE,"E9");var subQ1=sQuery(id+"F2.wireOp",EDGE,"E8.1.2.3");var subQ2=makeQuery(id+"F2.imprint","INTERSECT",VERTEX,{"derivedFrom":[subQ1,subQ0]});Q6=makeQuery(id+"F2.imprint","IMPRINT",FACE,{"disambiguationData":[TD([[makeQuery(id+"F2.imprint","IMPRINT",EDGE,{"disambiguationData":[TD([[subQ2,1.0]])],"derivedFrom":subQ1}),-1.0]])]});}
            var Q7;
            {var subQ0=sQuery(id+"F2.wireOp",EDGE,"E9");var subQ1=sQuery(id+"F2.wireOp",EDGE,"E3.1.2.0");var subQ2=makeQuery(id+"F2.imprint","INTERSECT",VERTEX,{"derivedFrom":[subQ1,subQ0]});Q7=makeQuery(id+"F2.imprint","IMPRINT",FACE,{"disambiguationData":[TD([[makeQuery(id+"F2.imprint","IMPRINT",EDGE,{"disambiguationData":[TD([[subQ2,1.0]])],"derivedFrom":subQ1}),1.0]])]});}
            var Q8;
            {var subQ0=sQuery(id+"F2.wireOp",EDGE,"E9");var subQ1=sQuery(id+"F2.wireOp",EDGE,"E3.1.2.0");var subQ2=makeQuery(id+"F2.imprint","INTERSECT",VERTEX,{"derivedFrom":[subQ1,subQ0]});Q8=makeQuery(id+"F2.imprint","IMPRINT",FACE,{"disambiguationData":[TD([[makeQuery(id+"F2.imprint","IMPRINT",EDGE,{"disambiguationData":[TD([[subQ2,1.0]])],"derivedFrom":subQ1}),-1.0]])]});}
            var Q9;
            {var subQ0=sQuery(id+"F2.wireOp",EDGE,"E9");var subQ1=sQuery(id+"F2.wireOp",EDGE,"E3.1.2.3");var subQ2=makeQuery(id+"F2.imprint","INTERSECT",VERTEX,{"derivedFrom":[subQ1,subQ0]});Q9=makeQuery(id+"F2.imprint","IMPRINT",FACE,{"disambiguationData":[TD([[makeQuery(id+"F2.imprint","IMPRINT",EDGE,{"disambiguationData":[TD([[subQ2,-1.0]])],"derivedFrom":subQ1}),1.0]])]});}
            var Q10;
            {var subQ0=sQuery(id+"F2.wireOp",EDGE,"E9");var subQ1=sQuery(id+"F2.wireOp",EDGE,"E8.0.1.2");var subQ2=makeQuery(id+"F2.imprint","INTERSECT",VERTEX,{"derivedFrom":[subQ1,subQ0]});Q10=makeQuery(id+"F2.imprint","IMPRINT",FACE,{"disambiguationData":[TD([[makeQuery(id+"F2.imprint","IMPRINT",EDGE,{"disambiguationData":[TD([[subQ2,1.0]])],"derivedFrom":subQ1}),-1.0]])]});}
            var Q11;
            {var subQ7=sQuery(id+"F2.wireOp",EDGE,"E3.1.1.5");var subQ8=sQuery(id+"F2.wireOp",EDGE,"E3.1.1.4");var subQ9=makeQuery(id+"F2.imprint","INTERSECT",VERTEX,{"derivedFrom":[subQ8,subQ7]});Q11=makeQuery(id+"F2.imprint","IMPRINT",FACE,{"disambiguationData":[TD([[makeQuery(id+"F2.imprint","IMPRINT",EDGE,{"disambiguationData":[TD([[subQ9,1.0]])],"derivedFrom":subQ8}),1.0]])]});}
            var Q12;
            {var subQ6=sQuery(id+"F2.wireOp",EDGE,"E3.1.1.2");var subQ9=sQuery(id+"F2.wireOp",EDGE,"E3.1.1.3");var subQ10=makeQuery(id+"F2.imprint","INTERSECT",VERTEX,{"derivedFrom":[subQ6,subQ9]});Q12=makeQuery(id+"F2.imprint","IMPRINT",FACE,{"disambiguationData":[TD([[makeQuery(id+"F2.imprint","IMPRINT",EDGE,{"disambiguationData":[TD([[subQ10,1.0]])],"derivedFrom":subQ6}),-1.0]])]});}
            var Q13;
            {var subQ5=sQuery(id+"F2.wireOp",EDGE,"E3.1.1.2");var subQ9=sQuery(id+"F2.wireOp",EDGE,"E3.1.1.3");var subQ10=makeQuery(id+"F2.imprint","INTERSECT",VERTEX,{"derivedFrom":[subQ5,subQ9]});Q13=makeQuery(id+"F2.imprint","IMPRINT",FACE,{"disambiguationData":[TD([[makeQuery(id+"F2.imprint","IMPRINT",EDGE,{"disambiguationData":[TD([[subQ10,1.0]])],"derivedFrom":subQ5}),1.0]])]});}
            var Q14;
            {var subQ1=sQuery(id+"F2.wireOp",EDGE,"E8.1.0.1");var subQ5=sQuery(id+"F2.wireOp",EDGE,"E8.1.0.0");var subQ6=makeQuery(id+"F2.imprint","INTERSECT",VERTEX,{"derivedFrom":[subQ5,subQ1]});Q14=makeQuery(id+"F2.imprint","IMPRINT",FACE,{"disambiguationData":[TD([[makeQuery(id+"F2.imprint","IMPRINT",EDGE,{"disambiguationData":[TD([[subQ6,1.0]])],"derivedFrom":subQ5}),-1.0]])]});}
            var Q15;
            {var subQ5=sQuery(id+"F2.wireOp",EDGE,"E9");var subQ7=sQuery(id+"F2.wireOp",EDGE,"E8.1.0.3");var subQ8=makeQuery(id+"F2.imprint","INTERSECT",VERTEX,{"derivedFrom":[subQ7,subQ5]});Q15=makeQuery(id+"F2.imprint","IMPRINT",FACE,{"disambiguationData":[TD([[makeQuery(id+"F2.imprint","IMPRINT",EDGE,{"disambiguationData":[TD([[subQ8,-1.0]])],"derivedFrom":subQ7}),1.0]])]});}
            var Q16;
            {var subQ1=sQuery(id+"F2.wireOp",EDGE,"E8.2.0.0");var subQ7=sQuery(id+"F2.wireOp",EDGE,"E8.2.0.5");var subQ9=makeQuery(id+"F2.imprint","INTERSECT",VERTEX,{"derivedFrom":[subQ1,subQ7]});Q16=makeQuery(id+"F2.imprint","IMPRINT",FACE,{"disambiguationData":[TD([[makeQuery(id+"F2.imprint","IMPRINT",EDGE,{"disambiguationData":[TD([[subQ9,-1.0]])],"derivedFrom":subQ1}),-1.0]])]});}
            var Q17;
            {var subQ3=sQuery(id+"F2.wireOp",EDGE,"E8.2.0.4");var subQ5=sQuery(id+"F2.wireOp",EDGE,"E8.2.0.3");var subQ6=makeQuery(id+"F2.imprint","INTERSECT",VERTEX,{"derivedFrom":[subQ5,subQ3]});Q17=makeQuery(id+"F2.imprint","IMPRINT",FACE,{"disambiguationData":[TD([[makeQuery(id+"F2.imprint","IMPRINT",EDGE,{"disambiguationData":[TD([[subQ6,1.0]])],"derivedFrom":subQ5}),-1.0]])]});}
            var Q18;
            {var subQ7=sQuery(id+"F2.wireOp",EDGE,"E8.2.0.4");var subQ8=sQuery(id+"F2.wireOp",EDGE,"E8.2.0.3");var subQ9=makeQuery(id+"F2.imprint","INTERSECT",VERTEX,{"derivedFrom":[subQ8,subQ7]});Q18=makeQuery(id+"F2.imprint","IMPRINT",FACE,{"disambiguationData":[TD([[makeQuery(id+"F2.imprint","IMPRINT",EDGE,{"disambiguationData":[TD([[subQ9,1.0]])],"derivedFrom":subQ8}),1.0]])]});}
            var Q19;
            {var subQ0=sQuery(id+"F2.wireOp",EDGE,"E8.3.0.5");var subQ1=sQuery(id+"F2.wireOp",EDGE,"E8.3.0.0");var subQ2=makeQuery(id+"F2.imprint","INTERSECT",VERTEX,{"derivedFrom":[subQ1,subQ0]});Q19=makeQuery(id+"F2.imprint","IMPRINT",FACE,{"disambiguationData":[TD([[makeQuery(id+"F2.imprint","IMPRINT",EDGE,{"disambiguationData":[TD([[subQ2,-1.0]])],"derivedFrom":subQ1}),-1.0]])]});}
            var Q20;
            {var subQ5=sQuery(id+"F2.wireOp",EDGE,"E3.4.1.3");var subQ6=sQuery(id+"F2.wireOp",EDGE,"E3.4.1.2");var subQ7=makeQuery(id+"F2.imprint","INTERSECT",VERTEX,{"derivedFrom":[subQ6,subQ5]});Q20=makeQuery(id+"F2.imprint","IMPRINT",FACE,{"disambiguationData":[TD([[makeQuery(id+"F2.imprint","IMPRINT",EDGE,{"disambiguationData":[TD([[subQ7,1.0]])],"derivedFrom":subQ6}),1.0]])]});}
            var Q21;
            {var subQ3=sQuery(id+"F2.wireOp",EDGE,"E9");var subQ5=sQuery(id+"F2.wireOp",EDGE,"E3.4.1.1");var subQ6=makeQuery(id+"F2.imprint","INTERSECT",VERTEX,{"derivedFrom":[subQ5,subQ3]});Q21=makeQuery(id+"F2.imprint","IMPRINT",FACE,{"disambiguationData":[TD([[makeQuery(id+"F2.imprint","IMPRINT",EDGE,{"disambiguationData":[TD([[subQ6,-1.0]])],"derivedFrom":subQ5}),-1.0]])]});}
            var Q22;
            {var subQ0=sQuery(id+"F2.wireOp",EDGE,"E9");var subQ1=sQuery(id+"F2.wireOp",EDGE,"E3.4.1.1");var subQ2=makeQuery(id+"F2.imprint","INTERSECT",VERTEX,{"derivedFrom":[subQ1,subQ0]});Q22=makeQuery(id+"F2.imprint","IMPRINT",FACE,{"disambiguationData":[TD([[makeQuery(id+"F2.imprint","IMPRINT",EDGE,{"disambiguationData":[TD([[subQ2,-1.0]])],"derivedFrom":subQ1}),1.0]])]});}
            var Q23;
            {var subQ5=sQuery(id+"F2.wireOp",EDGE,"E8.4.1.2");var subQ6=sQuery(id+"F2.wireOp",EDGE,"E8.4.1.1");var subQ7=makeQuery(id+"F2.imprint","INTERSECT",VERTEX,{"derivedFrom":[subQ6,subQ5]});Q23=makeQuery(id+"F2.imprint","IMPRINT",FACE,{"disambiguationData":[TD([[makeQuery(id+"F2.imprint","IMPRINT",EDGE,{"disambiguationData":[TD([[subQ7,1.0]])],"derivedFrom":subQ6}),-1.0]])]});}
            var Q24;
            {var subQ5=sQuery(id+"F2.wireOp",EDGE,"E3.4.2.2");var subQ6=sQuery(id+"F2.wireOp",EDGE,"E3.4.2.1");var subQ7=makeQuery(id+"F2.imprint","INTERSECT",VERTEX,{"derivedFrom":[subQ6,subQ5]});Q24=makeQuery(id+"F2.imprint","IMPRINT",FACE,{"disambiguationData":[TD([[makeQuery(id+"F2.imprint","IMPRINT",EDGE,{"disambiguationData":[TD([[subQ7,1.0]])],"derivedFrom":subQ6}),1.0]])]});}
            var Q25;
            {var subQ1=sQuery(id+"F2.wireOp",EDGE,"E3.4.2.2");var subQ7=sQuery(id+"F2.wireOp",EDGE,"E3.4.2.1");var subQ8=makeQuery(id+"F2.imprint","INTERSECT",VERTEX,{"derivedFrom":[subQ7,subQ1]});Q25=makeQuery(id+"F2.imprint","IMPRINT",FACE,{"disambiguationData":[TD([[makeQuery(id+"F2.imprint","IMPRINT",EDGE,{"disambiguationData":[TD([[subQ8,1.0]])],"derivedFrom":subQ7}),-1.0]])]});}
            var Q26;
            {var subQ0=sQuery(id+"F2.wireOp",EDGE,"E8.1.2.4");Q26=makeQuery(id+"F2.imprint","IMPRINT",FACE,{"disambiguationData":[TD([[makeQuery(id+"F2.imprint","IMPRINT",EDGE,{"derivedFrom":subQ0}),-1.0]])]});}
            var Q27;
            {var subQ0=sQuery(id+"F2.wireOp",EDGE,"E8.3.2.5");Q27=makeQuery(id+"F2.imprint","IMPRINT",FACE,{"disambiguationData":[TD([[makeQuery(id+"F2.imprint","IMPRINT",EDGE,{"derivedFrom":subQ0}),-1.0]])]});}
            extrude(context, id + "F3", {"entities" : qUnion([Q0, Q1, Q2, Q3, Q4, Q5, Q6, Q7, Q8, Q9, Q10, Q11, Q12, Q13, Q14, Q15, Q16, Q17, Q18, Q19, Q20, Q21, Q22, Q23, Q24, Q25, Q26, Q27]), "operationType" : NewBodyOperationType.ADD, "depth" : 1.5 * mm, "offsetDistance" : 25 * mm});
        }
        {
            var Q0;
            Q0=makeQuery(id+"F3.boolean.opBoolean","SPLIT",FACE,{"disambiguationData":[TD([makeQuery(id+"F3.opExtrude","SWEPT_FACE",FACE,{"disambiguationData":[OSD([sQuery(id+"F2.wireOp",EDGE,"E3.1.2.0")])]})])],"derivedFrom":makeQuery(id+"F1.opExtrude","CAP_FACE",FACE,{"disambiguationData":[OSD([sQuery(id+"F0.wireOp",EDGE,"E0"),sQuery(id+"F0.wireOp",EDGE,"E1")])],"isStart":false})});
            var Q1;
            Q1=makeQuery(id+"F3.boolean.opBoolean","SPLIT",FACE,{"disambiguationData":[TD([makeQuery(id+"F3.opExtrude","SWEPT_FACE",FACE,{"disambiguationData":[OSD([sQuery(id+"F2.wireOp",EDGE,"E8.1.2.0")])]})])],"derivedFrom":makeQuery(id+"F1.opExtrude","CAP_FACE",FACE,{"disambiguationData":[OSD([sQuery(id+"F0.wireOp",EDGE,"E0"),sQuery(id+"F0.wireOp",EDGE,"E1")])],"isStart":false})});
            var Q2;
            {var subQ1=sQuery(id+"F2.wireOp",EDGE,"E3.1.3.0");Q2=makeQuery(id+"F3.boolean.opBoolean","SPLIT",FACE,{"disambiguationData":[TD([makeQuery(id+"F3.opExtrude","SWEPT_FACE",FACE,{"disambiguationData":[OSD([subQ1])]})])],"derivedFrom":makeQuery(id+"F1.opExtrude","CAP_FACE",FACE,{"disambiguationData":[OSD([sQuery(id+"F0.wireOp",EDGE,"E0"),sQuery(id+"F0.wireOp",EDGE,"E1")])],"isStart":false})});}
            var Q3;
            {var subQ1=sQuery(id+"F2.wireOp",EDGE,"E8.1.3.2");Q3=makeQuery(id+"F3.boolean.opBoolean","SPLIT",FACE,{"disambiguationData":[TD([makeQuery(id+"F3.opExtrude","SWEPT_FACE",FACE,{"disambiguationData":[OSD([subQ1])]})])],"derivedFrom":makeQuery(id+"F1.opExtrude","CAP_FACE",FACE,{"disambiguationData":[OSD([sQuery(id+"F0.wireOp",EDGE,"E0"),sQuery(id+"F0.wireOp",EDGE,"E1")])],"isStart":false})});}
            var Q4;
            Q4=makeQuery(id+"F3.boolean.opBoolean","SPLIT",FACE,{"disambiguationData":[TD([makeQuery(id+"F3.opExtrude","SWEPT_FACE",FACE,{"disambiguationData":[OSD([sQuery(id+"F2.wireOp",EDGE,"E3.2.3.0")])]})])],"derivedFrom":makeQuery(id+"F1.opExtrude","CAP_FACE",FACE,{"disambiguationData":[OSD([sQuery(id+"F0.wireOp",EDGE,"E0"),sQuery(id+"F0.wireOp",EDGE,"E1")])],"isStart":false})});
            var Q5;
            Q5=makeQuery(id+"F3.boolean.opBoolean","SPLIT",FACE,{"disambiguationData":[TD([makeQuery(id+"F3.opExtrude","SWEPT_FACE",FACE,{"disambiguationData":[OSD([sQuery(id+"F2.wireOp",EDGE,"E8.2.3.0")])]})])],"derivedFrom":makeQuery(id+"F1.opExtrude","CAP_FACE",FACE,{"disambiguationData":[OSD([sQuery(id+"F0.wireOp",EDGE,"E0"),sQuery(id+"F0.wireOp",EDGE,"E1")])],"isStart":false})});
            var Q6;
            {var subQ2=sQuery(id+"F2.wireOp",EDGE,"E3.2.4.0");Q6=makeQuery(id+"F3.boolean.opBoolean","SPLIT",FACE,{"disambiguationData":[TD([makeQuery(id+"F3.opExtrude","SWEPT_FACE",FACE,{"disambiguationData":[OSD([subQ2])]})])],"derivedFrom":makeQuery(id+"F1.opExtrude","CAP_FACE",FACE,{"disambiguationData":[OSD([sQuery(id+"F0.wireOp",EDGE,"E0"),sQuery(id+"F0.wireOp",EDGE,"E1")])],"isStart":false})});}
            var Q7;
            Q7=makeQuery(id+"F3.boolean.opBoolean","SPLIT",FACE,{"disambiguationData":[TD([makeQuery(id+"F3.opExtrude","SWEPT_FACE",FACE,{"disambiguationData":[OSD([sQuery(id+"F2.wireOp",EDGE,"E3.3.4.0")])]})])],"derivedFrom":makeQuery(id+"F1.opExtrude","CAP_FACE",FACE,{"disambiguationData":[OSD([sQuery(id+"F0.wireOp",EDGE,"E0"),sQuery(id+"F0.wireOp",EDGE,"E1")])],"isStart":false})});
            var Q8;
            {var subQ1=sQuery(id+"F2.wireOp",EDGE,"E8.3.4.0");Q8=makeQuery(id+"F3.boolean.opBoolean","SPLIT",FACE,{"disambiguationData":[TD([makeQuery(id+"F3.opExtrude","SWEPT_FACE",FACE,{"disambiguationData":[OSD([subQ1])]})])],"derivedFrom":makeQuery(id+"F1.opExtrude","CAP_FACE",FACE,{"disambiguationData":[OSD([sQuery(id+"F0.wireOp",EDGE,"E0"),sQuery(id+"F0.wireOp",EDGE,"E1")])],"isStart":false})});}
            var Q9;
            Q9=makeQuery(id+"F3.boolean.opBoolean","SPLIT",FACE,{"disambiguationData":[TD([makeQuery(id+"F3.opExtrude","SWEPT_FACE",FACE,{"disambiguationData":[OSD([sQuery(id+"F2.wireOp",EDGE,"E8.4.4.0")])]})])],"derivedFrom":makeQuery(id+"F1.opExtrude","CAP_FACE",FACE,{"disambiguationData":[OSD([sQuery(id+"F0.wireOp",EDGE,"E0"),sQuery(id+"F0.wireOp",EDGE,"E1")])],"isStart":false})});
            var Q10;
            Q10=makeQuery(id+"F3.boolean.opBoolean","SPLIT",FACE,{"disambiguationData":[TD([makeQuery(id+"F3.opExtrude","SWEPT_FACE",FACE,{"disambiguationData":[OSD([sQuery(id+"F2.wireOp",EDGE,"E8.5.4.0")])]})])],"derivedFrom":makeQuery(id+"F1.opExtrude","CAP_FACE",FACE,{"disambiguationData":[OSD([sQuery(id+"F0.wireOp",EDGE,"E0"),sQuery(id+"F0.wireOp",EDGE,"E1")])],"isStart":false})});
            var Q11;
            {var subQ0=sQuery(id+"F2.wireOp",EDGE,"E8.6.4.0");Q11=makeQuery(id+"F3.boolean.opBoolean","SPLIT",FACE,{"disambiguationData":[TD([makeQuery(id+"F3.opExtrude","SWEPT_FACE",FACE,{"disambiguationData":[OSD([subQ0])]})])],"derivedFrom":makeQuery(id+"F1.opExtrude","CAP_FACE",FACE,{"disambiguationData":[OSD([sQuery(id+"F0.wireOp",EDGE,"E0"),sQuery(id+"F0.wireOp",EDGE,"E1")])],"isStart":false})});}
            var Q12;
            Q12=makeQuery(id+"F3.boolean.opBoolean","SPLIT",FACE,{"disambiguationData":[TD([makeQuery(id+"F3.opExtrude","SWEPT_FACE",FACE,{"disambiguationData":[OSD([sQuery(id+"F2.wireOp",EDGE,"E3.7.4.0")])]})])],"derivedFrom":makeQuery(id+"F1.opExtrude","CAP_FACE",FACE,{"disambiguationData":[OSD([sQuery(id+"F0.wireOp",EDGE,"E0"),sQuery(id+"F0.wireOp",EDGE,"E1")])],"isStart":false})});
            var Q13;
            Q13=makeQuery(id+"F3.boolean.opBoolean","SPLIT",FACE,{"disambiguationData":[TD([makeQuery(id+"F3.opExtrude","SWEPT_FACE",FACE,{"disambiguationData":[OSD([sQuery(id+"F2.wireOp",EDGE,"E3.6.4.0")])]})])],"derivedFrom":makeQuery(id+"F1.opExtrude","CAP_FACE",FACE,{"disambiguationData":[OSD([sQuery(id+"F0.wireOp",EDGE,"E0"),sQuery(id+"F0.wireOp",EDGE,"E1")])],"isStart":false})});
            var Q14;
            Q14=makeQuery(id+"F3.boolean.opBoolean","SPLIT",FACE,{"disambiguationData":[TD([makeQuery(id+"F3.opExtrude","SWEPT_FACE",FACE,{"disambiguationData":[OSD([sQuery(id+"F2.wireOp",EDGE,"E8.6.3.0")])]})])],"derivedFrom":makeQuery(id+"F1.opExtrude","CAP_FACE",FACE,{"disambiguationData":[OSD([sQuery(id+"F0.wireOp",EDGE,"E0"),sQuery(id+"F0.wireOp",EDGE,"E1")])],"isStart":false})});
            var Q15;
            Q15=makeQuery(id+"F3.boolean.opBoolean","SPLIT",FACE,{"disambiguationData":[TD([makeQuery(id+"F3.opExtrude","SWEPT_FACE",FACE,{"disambiguationData":[OSD([sQuery(id+"F2.wireOp",EDGE,"E8.7.3.0")])]})])],"derivedFrom":makeQuery(id+"F1.opExtrude","CAP_FACE",FACE,{"disambiguationData":[OSD([sQuery(id+"F0.wireOp",EDGE,"E0"),sQuery(id+"F0.wireOp",EDGE,"E1")])],"isStart":false})});
            var Q16;
            Q16=makeQuery(id+"F3.boolean.opBoolean","SPLIT",FACE,{"disambiguationData":[TD([makeQuery(id+"F3.opExtrude","SWEPT_FACE",FACE,{"disambiguationData":[OSD([sQuery(id+"F2.wireOp",EDGE,"E3.8.3.0")])]})])],"derivedFrom":makeQuery(id+"F1.opExtrude","CAP_FACE",FACE,{"disambiguationData":[OSD([sQuery(id+"F0.wireOp",EDGE,"E0"),sQuery(id+"F0.wireOp",EDGE,"E1")])],"isStart":false})});
            var Q17;
            Q17=makeQuery(id+"F3.boolean.opBoolean","SPLIT",FACE,{"disambiguationData":[TD([makeQuery(id+"F3.opExtrude","SWEPT_FACE",FACE,{"disambiguationData":[OSD([sQuery(id+"F2.wireOp",EDGE,"E8.8.2.0")])]})])],"derivedFrom":makeQuery(id+"F1.opExtrude","CAP_FACE",FACE,{"disambiguationData":[OSD([sQuery(id+"F0.wireOp",EDGE,"E0"),sQuery(id+"F0.wireOp",EDGE,"E1")])],"isStart":false})});
            var Q18;
            Q18=makeQuery(id+"F3.boolean.opBoolean","SPLIT",FACE,{"disambiguationData":[TD([makeQuery(id+"F3.opExtrude","SWEPT_FACE",FACE,{"disambiguationData":[OSD([sQuery(id+"F2.wireOp",EDGE,"E8.7.2.0")])]})])],"derivedFrom":makeQuery(id+"F1.opExtrude","CAP_FACE",FACE,{"disambiguationData":[OSD([sQuery(id+"F0.wireOp",EDGE,"E0"),sQuery(id+"F0.wireOp",EDGE,"E1")])],"isStart":false})});
            var Q19;
            {var subQ0=sQuery(id+"F2.wireOp",EDGE,"E8.8.3.0");Q19=makeQuery(id+"F3.boolean.opBoolean","SPLIT",FACE,{"disambiguationData":[TD([makeQuery(id+"F3.opExtrude","SWEPT_FACE",FACE,{"disambiguationData":[OSD([subQ0])]})])],"derivedFrom":makeQuery(id+"F1.opExtrude","CAP_FACE",FACE,{"disambiguationData":[OSD([sQuery(id+"F0.wireOp",EDGE,"E0"),sQuery(id+"F0.wireOp",EDGE,"E1")])],"isStart":false})});}
            var Q20;
            {var subQ0=sQuery(id+"F2.wireOp",EDGE,"E3.8.4.3");Q20=makeQuery(id+"F3.boolean.opBoolean","SPLIT",FACE,{"disambiguationData":[TD([makeQuery(id+"F3.opExtrude","SWEPT_FACE",FACE,{"disambiguationData":[OSD([subQ0])]})])],"derivedFrom":makeQuery(id+"F1.opExtrude","CAP_FACE",FACE,{"disambiguationData":[OSD([sQuery(id+"F0.wireOp",EDGE,"E0"),sQuery(id+"F0.wireOp",EDGE,"E1")])],"isStart":false})});}
            var Q21;
            Q21=makeQuery(id+"F3.boolean.opBoolean","SPLIT",FACE,{"disambiguationData":[TD([makeQuery(id+"F3.opExtrude","SWEPT_FACE",FACE,{"disambiguationData":[OSD([sQuery(id+"F2.wireOp",EDGE,"E3.7.3.0")])]})])],"derivedFrom":makeQuery(id+"F1.opExtrude","CAP_FACE",FACE,{"disambiguationData":[OSD([sQuery(id+"F0.wireOp",EDGE,"E0"),sQuery(id+"F0.wireOp",EDGE,"E1")])],"isStart":false})});
            var Q22;
            Q22=makeQuery(id+"F3.boolean.opBoolean","SPLIT",FACE,{"disambiguationData":[TD([makeQuery(id+"F3.opExtrude","SWEPT_FACE",FACE,{"disambiguationData":[OSD([sQuery(id+"F2.wireOp",EDGE,"E8.6.2.0")])]})])],"derivedFrom":makeQuery(id+"F1.opExtrude","CAP_FACE",FACE,{"disambiguationData":[OSD([sQuery(id+"F0.wireOp",EDGE,"E0"),sQuery(id+"F0.wireOp",EDGE,"E1")])],"isStart":false})});
            var Q23;
            Q23=makeQuery(id+"F3.boolean.opBoolean","SPLIT",FACE,{"disambiguationData":[TD([makeQuery(id+"F3.opExtrude","SWEPT_FACE",FACE,{"disambiguationData":[OSD([sQuery(id+"F2.wireOp",EDGE,"E3.8.2.0")])]})])],"derivedFrom":makeQuery(id+"F1.opExtrude","CAP_FACE",FACE,{"disambiguationData":[OSD([sQuery(id+"F0.wireOp",EDGE,"E0"),sQuery(id+"F0.wireOp",EDGE,"E1")])],"isStart":false})});
            var Q24;
            Q24=makeQuery(id+"F3.boolean.opBoolean","SPLIT",FACE,{"disambiguationData":[TD([makeQuery(id+"F3.opExtrude","SWEPT_FACE",FACE,{"disambiguationData":[OSD([sQuery(id+"F2.wireOp",EDGE,"E8.7.1.0")])]})])],"derivedFrom":makeQuery(id+"F1.opExtrude","CAP_FACE",FACE,{"disambiguationData":[OSD([sQuery(id+"F0.wireOp",EDGE,"E0"),sQuery(id+"F0.wireOp",EDGE,"E1")])],"isStart":false})});
            var Q25;
            Q25=makeQuery(id+"F3.boolean.opBoolean","SPLIT",FACE,{"disambiguationData":[TD([makeQuery(id+"F3.opExtrude","SWEPT_FACE",FACE,{"disambiguationData":[OSD([sQuery(id+"F2.wireOp",EDGE,"E3.7.2.0")])]})])],"derivedFrom":makeQuery(id+"F1.opExtrude","CAP_FACE",FACE,{"disambiguationData":[OSD([sQuery(id+"F0.wireOp",EDGE,"E0"),sQuery(id+"F0.wireOp",EDGE,"E1")])],"isStart":false})});
            var Q26;
            Q26=makeQuery(id+"F3.boolean.opBoolean","SPLIT",FACE,{"disambiguationData":[TD([makeQuery(id+"F3.opExtrude","SWEPT_FACE",FACE,{"disambiguationData":[OSD([sQuery(id+"F2.wireOp",EDGE,"E3.7.1.0")])]})])],"derivedFrom":makeQuery(id+"F1.opExtrude","CAP_FACE",FACE,{"disambiguationData":[OSD([sQuery(id+"F0.wireOp",EDGE,"E0"),sQuery(id+"F0.wireOp",EDGE,"E1")])],"isStart":false})});
            var Q27;
            Q27=makeQuery(id+"F3.boolean.opBoolean","SPLIT",FACE,{"disambiguationData":[TD([makeQuery(id+"F3.opExtrude","SWEPT_FACE",FACE,{"disambiguationData":[OSD([sQuery(id+"F2.wireOp",EDGE,"E3.6.1.0")])]})])],"derivedFrom":makeQuery(id+"F1.opExtrude","CAP_FACE",FACE,{"disambiguationData":[OSD([sQuery(id+"F0.wireOp",EDGE,"E0"),sQuery(id+"F0.wireOp",EDGE,"E1")])],"isStart":false})});
            var Q28;
            Q28=makeQuery(id+"F3.boolean.opBoolean","SPLIT",FACE,{"disambiguationData":[TD([makeQuery(id+"F3.opExtrude","SWEPT_FACE",FACE,{"disambiguationData":[OSD([sQuery(id+"F2.wireOp",EDGE,"E8.6.1.0")])]})])],"derivedFrom":makeQuery(id+"F1.opExtrude","CAP_FACE",FACE,{"disambiguationData":[OSD([sQuery(id+"F0.wireOp",EDGE,"E0"),sQuery(id+"F0.wireOp",EDGE,"E1")])],"isStart":false})});
            var Q29;
            Q29=makeQuery(id+"F3.boolean.opBoolean","SPLIT",FACE,{"disambiguationData":[TD([makeQuery(id+"F3.opExtrude","SWEPT_FACE",FACE,{"disambiguationData":[OSD([sQuery(id+"F2.wireOp",EDGE,"E3.6.2.0")])]})])],"derivedFrom":makeQuery(id+"F1.opExtrude","CAP_FACE",FACE,{"disambiguationData":[OSD([sQuery(id+"F0.wireOp",EDGE,"E0"),sQuery(id+"F0.wireOp",EDGE,"E1")])],"isStart":false})});
            var Q30;
            Q30=makeQuery(id+"F3.boolean.opBoolean","SPLIT",FACE,{"disambiguationData":[TD([makeQuery(id+"F3.opExtrude","SWEPT_FACE",FACE,{"disambiguationData":[OSD([sQuery(id+"F2.wireOp",EDGE,"E8.5.1.0")])]})])],"derivedFrom":makeQuery(id+"F1.opExtrude","CAP_FACE",FACE,{"disambiguationData":[OSD([sQuery(id+"F0.wireOp",EDGE,"E0"),sQuery(id+"F0.wireOp",EDGE,"E1")])],"isStart":false})});
            var Q31;
            Q31=makeQuery(id+"F3.boolean.opBoolean","SPLIT",FACE,{"disambiguationData":[TD([makeQuery(id+"F3.opExtrude","SWEPT_FACE",FACE,{"disambiguationData":[OSD([sQuery(id+"F2.wireOp",EDGE,"E3.5.1.0")])]})])],"derivedFrom":makeQuery(id+"F1.opExtrude","CAP_FACE",FACE,{"disambiguationData":[OSD([sQuery(id+"F0.wireOp",EDGE,"E0"),sQuery(id+"F0.wireOp",EDGE,"E1")])],"isStart":false})});
            var Q32;
            {var subQ1=sQuery(id+"F2.wireOp",EDGE,"E8.5.0.0");Q32=makeQuery(id+"F3.boolean.opBoolean","SPLIT",FACE,{"disambiguationData":[TD([makeQuery(id+"F3.opExtrude","SWEPT_FACE",FACE,{"disambiguationData":[OSD([subQ1])]})])],"derivedFrom":makeQuery(id+"F1.opExtrude","CAP_FACE",FACE,{"disambiguationData":[OSD([sQuery(id+"F0.wireOp",EDGE,"E0"),sQuery(id+"F0.wireOp",EDGE,"E1")])],"isStart":false})});}
            var Q33;
            {var subQ1=sQuery(id+"F2.wireOp",EDGE,"E8.4.0.0");Q33=makeQuery(id+"F3.boolean.opBoolean","SPLIT",FACE,{"disambiguationData":[TD([makeQuery(id+"F3.opExtrude","SWEPT_FACE",FACE,{"disambiguationData":[OSD([subQ1])]})])],"derivedFrom":makeQuery(id+"F1.opExtrude","CAP_FACE",FACE,{"disambiguationData":[OSD([sQuery(id+"F0.wireOp",EDGE,"E0"),sQuery(id+"F0.wireOp",EDGE,"E1")])],"isStart":false})});}
            var Q34;
            Q34=makeQuery(id+"F3.boolean.opBoolean","SPLIT",FACE,{"disambiguationData":[TD([makeQuery(id+"F3.opExtrude","SWEPT_FACE",FACE,{"disambiguationData":[OSD([sQuery(id+"F2.wireOp",EDGE,"E3.6.3.0")])]})])],"derivedFrom":makeQuery(id+"F1.opExtrude","CAP_FACE",FACE,{"disambiguationData":[OSD([sQuery(id+"F0.wireOp",EDGE,"E0"),sQuery(id+"F0.wireOp",EDGE,"E1")])],"isStart":false})});
            var Q35;
            Q35=makeQuery(id+"F3.boolean.opBoolean","SPLIT",FACE,{"disambiguationData":[TD([makeQuery(id+"F3.opExtrude","SWEPT_FACE",FACE,{"disambiguationData":[OSD([sQuery(id+"F2.wireOp",EDGE,"E8.5.2.0")])]})])],"derivedFrom":makeQuery(id+"F1.opExtrude","CAP_FACE",FACE,{"disambiguationData":[OSD([sQuery(id+"F0.wireOp",EDGE,"E0"),sQuery(id+"F0.wireOp",EDGE,"E1")])],"isStart":false})});
            var Q36;
            Q36=makeQuery(id+"F3.boolean.opBoolean","SPLIT",FACE,{"disambiguationData":[TD([makeQuery(id+"F3.opExtrude","SWEPT_FACE",FACE,{"disambiguationData":[OSD([sQuery(id+"F2.wireOp",EDGE,"E3.5.2.0")])]})])],"derivedFrom":makeQuery(id+"F1.opExtrude","CAP_FACE",FACE,{"disambiguationData":[OSD([sQuery(id+"F0.wireOp",EDGE,"E0"),sQuery(id+"F0.wireOp",EDGE,"E1")])],"isStart":false})});
            var Q37;
            Q37=makeQuery(id+"F3.boolean.opBoolean","SPLIT",FACE,{"disambiguationData":[TD([makeQuery(id+"F3.opExtrude","SWEPT_FACE",FACE,{"disambiguationData":[OSD([sQuery(id+"F2.wireOp",EDGE,"E8.4.1.0")])]})])],"derivedFrom":makeQuery(id+"F1.opExtrude","CAP_FACE",FACE,{"disambiguationData":[OSD([sQuery(id+"F0.wireOp",EDGE,"E0"),sQuery(id+"F0.wireOp",EDGE,"E1")])],"isStart":false})});
            var Q38;
            Q38=makeQuery(id+"F3.boolean.opBoolean","SPLIT",FACE,{"disambiguationData":[TD([makeQuery(id+"F3.opExtrude","SWEPT_FACE",FACE,{"disambiguationData":[OSD([sQuery(id+"F2.wireOp",EDGE,"E3.4.1.0")])]})])],"derivedFrom":makeQuery(id+"F1.opExtrude","CAP_FACE",FACE,{"disambiguationData":[OSD([sQuery(id+"F0.wireOp",EDGE,"E0"),sQuery(id+"F0.wireOp",EDGE,"E1")])],"isStart":false})});
            var Q39;
            {var subQ0=sQuery(id+"F2.wireOp",EDGE,"E8.3.0.1");Q39=makeQuery(id+"F3.boolean.opBoolean","SPLIT",FACE,{"disambiguationData":[TD([makeQuery(id+"F3.opExtrude","SWEPT_FACE",FACE,{"disambiguationData":[OSD([subQ0])]})])],"derivedFrom":makeQuery(id+"F1.opExtrude","CAP_FACE",FACE,{"disambiguationData":[OSD([sQuery(id+"F0.wireOp",EDGE,"E0"),sQuery(id+"F0.wireOp",EDGE,"E1")])],"isStart":false})});}
            var Q40;
            Q40=makeQuery(id+"F3.boolean.opBoolean","SPLIT",FACE,{"disambiguationData":[TD([makeQuery(id+"F3.opExtrude","SWEPT_FACE",FACE,{"disambiguationData":[OSD([sQuery(id+"F2.wireOp",EDGE,"E3.3.1.0")])]})])],"derivedFrom":makeQuery(id+"F1.opExtrude","CAP_FACE",FACE,{"disambiguationData":[OSD([sQuery(id+"F0.wireOp",EDGE,"E0"),sQuery(id+"F0.wireOp",EDGE,"E1")])],"isStart":false})});
            var Q41;
            Q41=makeQuery(id+"F3.boolean.opBoolean","SPLIT",FACE,{"disambiguationData":[TD([makeQuery(id+"F3.opExtrude","SWEPT_FACE",FACE,{"disambiguationData":[OSD([sQuery(id+"F2.wireOp",EDGE,"E8.3.1.0")])]})])],"derivedFrom":makeQuery(id+"F1.opExtrude","CAP_FACE",FACE,{"disambiguationData":[OSD([sQuery(id+"F0.wireOp",EDGE,"E0"),sQuery(id+"F0.wireOp",EDGE,"E1")])],"isStart":false})});
            var Q42;
            Q42=makeQuery(id+"F3.boolean.opBoolean","SPLIT",FACE,{"disambiguationData":[TD([makeQuery(id+"F3.opExtrude","SWEPT_FACE",FACE,{"disambiguationData":[OSD([sQuery(id+"F2.wireOp",EDGE,"E3.4.2.0")])]})])],"derivedFrom":makeQuery(id+"F1.opExtrude","CAP_FACE",FACE,{"disambiguationData":[OSD([sQuery(id+"F0.wireOp",EDGE,"E0"),sQuery(id+"F0.wireOp",EDGE,"E1")])],"isStart":false})});
            var Q43;
            Q43=makeQuery(id+"F3.boolean.opBoolean","SPLIT",FACE,{"disambiguationData":[TD([makeQuery(id+"F3.opExtrude","SWEPT_FACE",FACE,{"disambiguationData":[OSD([sQuery(id+"F2.wireOp",EDGE,"E8.4.2.0")])]})])],"derivedFrom":makeQuery(id+"F1.opExtrude","CAP_FACE",FACE,{"disambiguationData":[OSD([sQuery(id+"F0.wireOp",EDGE,"E0"),sQuery(id+"F0.wireOp",EDGE,"E1")])],"isStart":false})});
            var Q44;
            Q44=makeQuery(id+"F3.boolean.opBoolean","SPLIT",FACE,{"disambiguationData":[TD([makeQuery(id+"F3.opExtrude","SWEPT_FACE",FACE,{"disambiguationData":[OSD([sQuery(id+"F2.wireOp",EDGE,"E3.5.3.0")])]})])],"derivedFrom":makeQuery(id+"F1.opExtrude","CAP_FACE",FACE,{"disambiguationData":[OSD([sQuery(id+"F0.wireOp",EDGE,"E0"),sQuery(id+"F0.wireOp",EDGE,"E1")])],"isStart":false})});
            var Q45;
            Q45=makeQuery(id+"F3.boolean.opBoolean","SPLIT",FACE,{"disambiguationData":[TD([makeQuery(id+"F3.opExtrude","SWEPT_FACE",FACE,{"disambiguationData":[OSD([sQuery(id+"F2.wireOp",EDGE,"E8.5.3.0")])]})])],"derivedFrom":makeQuery(id+"F1.opExtrude","CAP_FACE",FACE,{"disambiguationData":[OSD([sQuery(id+"F0.wireOp",EDGE,"E0"),sQuery(id+"F0.wireOp",EDGE,"E1")])],"isStart":false})});
            var Q46;
            Q46=makeQuery(id+"F3.boolean.opBoolean","SPLIT",FACE,{"disambiguationData":[TD([makeQuery(id+"F3.opExtrude","SWEPT_FACE",FACE,{"disambiguationData":[OSD([sQuery(id+"F2.wireOp",EDGE,"E3.5.4.0")])]})])],"derivedFrom":makeQuery(id+"F1.opExtrude","CAP_FACE",FACE,{"disambiguationData":[OSD([sQuery(id+"F0.wireOp",EDGE,"E0"),sQuery(id+"F0.wireOp",EDGE,"E1")])],"isStart":false})});
            var Q47;
            Q47=makeQuery(id+"F3.boolean.opBoolean","SPLIT",FACE,{"disambiguationData":[TD([makeQuery(id+"F3.opExtrude","SWEPT_FACE",FACE,{"disambiguationData":[OSD([sQuery(id+"F2.wireOp",EDGE,"E3.4.4.0")])]})])],"derivedFrom":makeQuery(id+"F1.opExtrude","CAP_FACE",FACE,{"disambiguationData":[OSD([sQuery(id+"F0.wireOp",EDGE,"E0"),sQuery(id+"F0.wireOp",EDGE,"E1")])],"isStart":false})});
            var Q48;
            Q48=makeQuery(id+"F3.boolean.opBoolean","SPLIT",FACE,{"disambiguationData":[TD([makeQuery(id+"F3.opExtrude","SWEPT_FACE",FACE,{"disambiguationData":[OSD([sQuery(id+"F2.wireOp",EDGE,"E8.3.3.0")])]})])],"derivedFrom":makeQuery(id+"F1.opExtrude","CAP_FACE",FACE,{"disambiguationData":[OSD([sQuery(id+"F0.wireOp",EDGE,"E0"),sQuery(id+"F0.wireOp",EDGE,"E1")])],"isStart":false})});
            var Q49;
            Q49=makeQuery(id+"F3.boolean.opBoolean","SPLIT",FACE,{"disambiguationData":[TD([makeQuery(id+"F3.opExtrude","SWEPT_FACE",FACE,{"disambiguationData":[OSD([sQuery(id+"F2.wireOp",EDGE,"E8.4.3.0")])]})])],"derivedFrom":makeQuery(id+"F1.opExtrude","CAP_FACE",FACE,{"disambiguationData":[OSD([sQuery(id+"F0.wireOp",EDGE,"E0"),sQuery(id+"F0.wireOp",EDGE,"E1")])],"isStart":false})});
            var Q50;
            Q50=makeQuery(id+"F3.boolean.opBoolean","SPLIT",FACE,{"disambiguationData":[TD([makeQuery(id+"F3.opExtrude","SWEPT_FACE",FACE,{"disambiguationData":[OSD([sQuery(id+"F2.wireOp",EDGE,"E3.4.3.0")])]})])],"derivedFrom":makeQuery(id+"F1.opExtrude","CAP_FACE",FACE,{"disambiguationData":[OSD([sQuery(id+"F0.wireOp",EDGE,"E0"),sQuery(id+"F0.wireOp",EDGE,"E1")])],"isStart":false})});
            var Q51;
            Q51=makeQuery(id+"F3.boolean.opBoolean","SPLIT",FACE,{"disambiguationData":[TD([makeQuery(id+"F3.opExtrude","SWEPT_FACE",FACE,{"disambiguationData":[OSD([sQuery(id+"F2.wireOp",EDGE,"E3.3.3.0")])]})])],"derivedFrom":makeQuery(id+"F1.opExtrude","CAP_FACE",FACE,{"disambiguationData":[OSD([sQuery(id+"F0.wireOp",EDGE,"E0"),sQuery(id+"F0.wireOp",EDGE,"E1")])],"isStart":false})});
            var Q52;
            Q52=makeQuery(id+"F3.boolean.opBoolean","SPLIT",FACE,{"disambiguationData":[TD([makeQuery(id+"F3.opExtrude","SWEPT_FACE",FACE,{"disambiguationData":[OSD([sQuery(id+"F2.wireOp",EDGE,"E8.3.2.0")])]})])],"derivedFrom":makeQuery(id+"F1.opExtrude","CAP_FACE",FACE,{"disambiguationData":[OSD([sQuery(id+"F0.wireOp",EDGE,"E0"),sQuery(id+"F0.wireOp",EDGE,"E1")])],"isStart":false})});
            var Q53;
            Q53=makeQuery(id+"F3.boolean.opBoolean","SPLIT",FACE,{"disambiguationData":[TD([makeQuery(id+"F3.opExtrude","SWEPT_FACE",FACE,{"disambiguationData":[OSD([sQuery(id+"F2.wireOp",EDGE,"E8.2.2.0")])]})])],"derivedFrom":makeQuery(id+"F1.opExtrude","CAP_FACE",FACE,{"disambiguationData":[OSD([sQuery(id+"F0.wireOp",EDGE,"E0"),sQuery(id+"F0.wireOp",EDGE,"E1")])],"isStart":false})});
            var Q54;
            Q54=makeQuery(id+"F3.boolean.opBoolean","SPLIT",FACE,{"disambiguationData":[TD([makeQuery(id+"F3.opExtrude","SWEPT_FACE",FACE,{"disambiguationData":[OSD([sQuery(id+"F2.wireOp",EDGE,"E3.3.2.0")])]})])],"derivedFrom":makeQuery(id+"F1.opExtrude","CAP_FACE",FACE,{"disambiguationData":[OSD([sQuery(id+"F0.wireOp",EDGE,"E0"),sQuery(id+"F0.wireOp",EDGE,"E1")])],"isStart":false})});
            var Q55;
            Q55=makeQuery(id+"F3.boolean.opBoolean","SPLIT",FACE,{"disambiguationData":[TD([makeQuery(id+"F3.opExtrude","SWEPT_FACE",FACE,{"disambiguationData":[OSD([sQuery(id+"F2.wireOp",EDGE,"E3.2.2.0")])]})])],"derivedFrom":makeQuery(id+"F1.opExtrude","CAP_FACE",FACE,{"disambiguationData":[OSD([sQuery(id+"F0.wireOp",EDGE,"E0"),sQuery(id+"F0.wireOp",EDGE,"E1")])],"isStart":false})});
            var Q56;
            Q56=makeQuery(id+"F3.boolean.opBoolean","SPLIT",FACE,{"disambiguationData":[TD([makeQuery(id+"F3.opExtrude","SWEPT_FACE",FACE,{"disambiguationData":[OSD([sQuery(id+"F2.wireOp",EDGE,"E8.2.1.0")])]})])],"derivedFrom":makeQuery(id+"F1.opExtrude","CAP_FACE",FACE,{"disambiguationData":[OSD([sQuery(id+"F0.wireOp",EDGE,"E0"),sQuery(id+"F0.wireOp",EDGE,"E1")])],"isStart":false})});
            var Q57;
            {var subQ2=sQuery(id+"F2.wireOp",EDGE,"E8.1.1.1");Q57=makeQuery(id+"F3.boolean.opBoolean","SPLIT",FACE,{"disambiguationData":[TD([makeQuery(id+"F3.opExtrude","SWEPT_FACE",FACE,{"disambiguationData":[OSD([subQ2])]})])],"derivedFrom":makeQuery(id+"F1.opExtrude","CAP_FACE",FACE,{"disambiguationData":[OSD([sQuery(id+"F0.wireOp",EDGE,"E0"),sQuery(id+"F0.wireOp",EDGE,"E1")])],"isStart":false})});}
            var Q58;
            Q58=makeQuery(id+"F3.boolean.opBoolean","SPLIT",FACE,{"disambiguationData":[TD([makeQuery(id+"F3.opExtrude","SWEPT_FACE",FACE,{"disambiguationData":[OSD([sQuery(id+"F2.wireOp",EDGE,"E3.2.1.0")])]})])],"derivedFrom":makeQuery(id+"F1.opExtrude","CAP_FACE",FACE,{"disambiguationData":[OSD([sQuery(id+"F0.wireOp",EDGE,"E0"),sQuery(id+"F0.wireOp",EDGE,"E1")])],"isStart":false})});
            chamfer(context, id + "F4", {"entities" : qUnion([Q0, Q1, Q2, Q3, Q4, Q5, Q6, Q7, Q8, Q9, Q10, Q11, Q12, Q13, Q14, Q15, Q16, Q17, Q18, Q19, Q20, Q21, Q22, Q23, Q24, Q25, Q26, Q27, Q28, Q29, Q30, Q31, Q32, Q33, Q34, Q35, Q36, Q37, Q38, Q39, Q40, Q41, Q42, Q43, Q44, Q45, Q46, Q47, Q48, Q49, Q50, Q51, Q52, Q53, Q54, Q55, Q56, Q57, Q58]), "width" : 0.4 * mm, "tangentPropagation" : true});
        }
        {
            var Q0;
            Q0=makeQuery(id+"F3.opExtrude","CAP_FACE",FACE,{"disambiguationData":[OSD([sQuery(id+"F0.wireOp",EDGE,"E0"),sQuery(id+"F0.wireOp",EDGE,"E1"),sQuery(id+"F2.wireOp",EDGE,"E3.1.2.0"),sQuery(id+"F2.wireOp",EDGE,"E3.1.2.1"),sQuery(id+"F2.wireOp",EDGE,"E3.1.2.2"),sQuery(id+"F2.wireOp",EDGE,"E3.1.2.5"),sQuery(id+"F2.wireOp",EDGE,"E3.1.3.0"),sQuery(id+"F2.wireOp",EDGE,"E3.1.3.1"),sQuery(id+"F2.wireOp",EDGE,"E3.1.3.2"),sQuery(id+"F2.wireOp",EDGE,"E3.1.3.3"),sQuery(id+"F2.wireOp",EDGE,"E3.1.4.1"),sQuery(id+"F2.wireOp",EDGE,"E3.1.4.2"),sQuery(id+"F2.wireOp",EDGE,"E3.2.1.0"),sQuery(id+"F2.wireOp",EDGE,"E3.2.1.1"),sQuery(id+"F2.wireOp",EDGE,"E3.2.1.5"),sQuery(id+"F2.wireOp",EDGE,"E3.2.2.0"),sQuery(id+"F2.wireOp",EDGE,"E3.2.2.1"),sQuery(id+"F2.wireOp",EDGE,"E3.2.2.2"),sQuery(id+"F2.wireOp",EDGE,"E3.2.2.3"),sQuery(id+"F2.wireOp",EDGE,"E3.2.2.4"),sQuery(id+"F2.wireOp",EDGE,"E3.2.2.5"),sQuery(id+"F2.wireOp",EDGE,"E3.2.3.0"),sQuery(id+"F2.wireOp",EDGE,"E3.2.3.1"),sQuery(id+"F2.wireOp",EDGE,"E3.2.3.2"),sQuery(id+"F2.wireOp",EDGE,"E3.2.3.3"),sQuery(id+"F2.wireOp",EDGE,"E3.2.3.4"),sQuery(id+"F2.wireOp",EDGE,"E3.2.3.5"),sQuery(id+"F2.wireOp",EDGE,"E3.2.4.0"),sQuery(id+"F2.wireOp",EDGE,"E3.2.4.1"),sQuery(id+"F2.wireOp",EDGE,"E3.2.4.2"),sQuery(id+"F2.wireOp",EDGE,"E3.2.4.3"),sQuery(id+"F2.wireOp",EDGE,"E3.3.1.0"),sQuery(id+"F2.wireOp",EDGE,"E3.3.1.1"),sQuery(id+"F2.wireOp",EDGE,"E3.3.1.2"),sQuery(id+"F2.wireOp",EDGE,"E3.3.1.3"),sQuery(id+"F2.wireOp",EDGE,"E3.3.1.4"),sQuery(id+"F2.wireOp",EDGE,"E3.3.1.5"),sQuery(id+"F2.wireOp",EDGE,"E3.3.2.0"),sQuery(id+"F2.wireOp",EDGE,"E3.3.2.1"),sQuery(id+"F2.wireOp",EDGE,"E3.3.2.2"),sQuery(id+"F2.wireOp",EDGE,"E3.3.2.3"),sQuery(id+"F2.wireOp",EDGE,"E3.3.2.4"),sQuery(id+"F2.wireOp",EDGE,"E3.3.2.5"),sQuery(id+"F2.wireOp",EDGE,"E3.3.3.0"),sQuery(id+"F2.wireOp",EDGE,"E3.3.3.1"),sQuery(id+"F2.wireOp",EDGE,"E3.3.3.2"),sQuery(id+"F2.wireOp",EDGE,"E3.3.3.3"),sQuery(id+"F2.wireOp",EDGE,"E3.3.3.4"),sQuery(id+"F2.wireOp",EDGE,"E3.3.3.5"),sQuery(id+"F2.wireOp",EDGE,"E3.3.4.0"),sQuery(id+"F2.wireOp",EDGE,"E3.3.4.1"),sQuery(id+"F2.wireOp",EDGE,"E3.3.4.2"),sQuery(id+"F2.wireOp",EDGE,"E3.3.4.3"),sQuery(id+"F2.wireOp",EDGE,"E3.3.4.4"),sQuery(id+"F2.wireOp",EDGE,"E3.3.4.5"),sQuery(id+"F2.wireOp",EDGE,"E3.4.1.0"),sQuery(id+"F2.wireOp",EDGE,"E3.4.1.1"),sQuery(id+"F2.wireOp",EDGE,"E3.4.1.2"),sQuery(id+"F2.wireOp",EDGE,"E3.4.1.3"),sQuery(id+"F2.wireOp",EDGE,"E3.4.1.4"),sQuery(id+"F2.wireOp",EDGE,"E3.4.1.5"),sQuery(id+"F2.wireOp",EDGE,"E3.4.2.0"),sQuery(id+"F2.wireOp",EDGE,"E3.4.2.1"),sQuery(id+"F2.wireOp",EDGE,"E3.4.2.2"),sQuery(id+"F2.wireOp",EDGE,"E3.4.2.3"),sQuery(id+"F2.wireOp",EDGE,"E3.4.2.4"),sQuery(id+"F2.wireOp",EDGE,"E3.4.2.5"),sQuery(id+"F2.wireOp",EDGE,"E3.4.3.0"),sQuery(id+"F2.wireOp",EDGE,"E3.4.3.1"),sQuery(id+"F2.wireOp",EDGE,"E3.4.3.2"),sQuery(id+"F2.wireOp",EDGE,"E3.4.3.3"),sQuery(id+"F2.wireOp",EDGE,"E3.4.3.4"),sQuery(id+"F2.wireOp",EDGE,"E3.4.3.5"),sQuery(id+"F2.wireOp",EDGE,"E3.4.4.0"),sQuery(id+"F2.wireOp",EDGE,"E3.4.4.1"),sQuery(id+"F2.wireOp",EDGE,"E3.4.4.2"),sQuery(id+"F2.wireOp",EDGE,"E3.4.4.3"),sQuery(id+"F2.wireOp",EDGE,"E3.4.4.4"),sQuery(id+"F2.wireOp",EDGE,"E3.4.4.5"),sQuery(id+"F2.wireOp",EDGE,"E3.5.1.0"),sQuery(id+"F2.wireOp",EDGE,"E3.5.1.1"),sQuery(id+"F2.wireOp",EDGE,"E3.5.1.2"),sQuery(id+"F2.wireOp",EDGE,"E3.5.1.3"),sQuery(id+"F2.wireOp",EDGE,"E3.5.1.4"),sQuery(id+"F2.wireOp",EDGE,"E3.5.1.5"),sQuery(id+"F2.wireOp",EDGE,"E3.5.2.0"),sQuery(id+"F2.wireOp",EDGE,"E3.5.2.1"),sQuery(id+"F2.wireOp",EDGE,"E3.5.2.2"),sQuery(id+"F2.wireOp",EDGE,"E3.5.2.3"),sQuery(id+"F2.wireOp",EDGE,"E3.5.2.4"),sQuery(id+"F2.wireOp",EDGE,"E3.5.2.5"),sQuery(id+"F2.wireOp",EDGE,"E3.5.3.0"),sQuery(id+"F2.wireOp",EDGE,"E3.5.3.1"),sQuery(id+"F2.wireOp",EDGE,"E3.5.3.2"),sQuery(id+"F2.wireOp",EDGE,"E3.5.3.3"),sQuery(id+"F2.wireOp",EDGE,"E3.5.3.4"),sQuery(id+"F2.wireOp",EDGE,"E3.5.3.5"),sQuery(id+"F2.wireOp",EDGE,"E3.5.4.0"),sQuery(id+"F2.wireOp",EDGE,"E3.5.4.1"),sQuery(id+"F2.wireOp",EDGE,"E3.5.4.2"),sQuery(id+"F2.wireOp",EDGE,"E3.5.4.3"),sQuery(id+"F2.wireOp",EDGE,"E3.5.4.4"),sQuery(id+"F2.wireOp",EDGE,"E3.5.4.5"),sQuery(id+"F2.wireOp",EDGE,"E3.6.1.0"),sQuery(id+"F2.wireOp",EDGE,"E3.6.1.1"),sQuery(id+"F2.wireOp",EDGE,"E3.6.1.2"),sQuery(id+"F2.wireOp",EDGE,"E3.6.1.3"),sQuery(id+"F2.wireOp",EDGE,"E3.6.1.4"),sQuery(id+"F2.wireOp",EDGE,"E3.6.1.5"),sQuery(id+"F2.wireOp",EDGE,"E3.6.2.0"),sQuery(id+"F2.wireOp",EDGE,"E3.6.2.1"),sQuery(id+"F2.wireOp",EDGE,"E3.6.2.2"),sQuery(id+"F2.wireOp",EDGE,"E3.6.2.3"),sQuery(id+"F2.wireOp",EDGE,"E3.6.2.4"),sQuery(id+"F2.wireOp",EDGE,"E3.6.2.5"),sQuery(id+"F2.wireOp",EDGE,"E3.6.3.0"),sQuery(id+"F2.wireOp",EDGE,"E3.6.3.1"),sQuery(id+"F2.wireOp",EDGE,"E3.6.3.2"),sQuery(id+"F2.wireOp",EDGE,"E3.6.3.3"),sQuery(id+"F2.wireOp",EDGE,"E3.6.3.4"),sQuery(id+"F2.wireOp",EDGE,"E3.6.3.5"),sQuery(id+"F2.wireOp",EDGE,"E3.6.4.0"),sQuery(id+"F2.wireOp",EDGE,"E3.6.4.1"),sQuery(id+"F2.wireOp",EDGE,"E3.6.4.2"),sQuery(id+"F2.wireOp",EDGE,"E3.6.4.3"),sQuery(id+"F2.wireOp",EDGE,"E3.6.4.4"),sQuery(id+"F2.wireOp",EDGE,"E3.6.4.5"),sQuery(id+"F2.wireOp",EDGE,"E3.7.1.0"),sQuery(id+"F2.wireOp",EDGE,"E3.7.1.1"),sQuery(id+"F2.wireOp",EDGE,"E3.7.1.2"),sQuery(id+"F2.wireOp",EDGE,"E3.7.1.3"),sQuery(id+"F2.wireOp",EDGE,"E3.7.1.4"),sQuery(id+"F2.wireOp",EDGE,"E3.7.1.5"),sQuery(id+"F2.wireOp",EDGE,"E3.7.2.0"),sQuery(id+"F2.wireOp",EDGE,"E3.7.2.1"),sQuery(id+"F2.wireOp",EDGE,"E3.7.2.2"),sQuery(id+"F2.wireOp",EDGE,"E3.7.2.3"),sQuery(id+"F2.wireOp",EDGE,"E3.7.2.4"),sQuery(id+"F2.wireOp",EDGE,"E3.7.2.5"),sQuery(id+"F2.wireOp",EDGE,"E3.7.3.0"),sQuery(id+"F2.wireOp",EDGE,"E3.7.3.1"),sQuery(id+"F2.wireOp",EDGE,"E3.7.3.2"),sQuery(id+"F2.wireOp",EDGE,"E3.7.3.3"),sQuery(id+"F2.wireOp",EDGE,"E3.7.3.4"),sQuery(id+"F2.wireOp",EDGE,"E3.7.3.5"),sQuery(id+"F2.wireOp",EDGE,"E3.7.4.0"),sQuery(id+"F2.wireOp",EDGE,"E3.7.4.1"),sQuery(id+"F2.wireOp",EDGE,"E3.7.4.2"),sQuery(id+"F2.wireOp",EDGE,"E3.7.4.3"),sQuery(id+"F2.wireOp",EDGE,"E3.7.4.4"),sQuery(id+"F2.wireOp",EDGE,"E3.7.4.5"),sQuery(id+"F2.wireOp",EDGE,"E3.8.2.0"),sQuery(id+"F2.wireOp",EDGE,"E3.8.2.1"),sQuery(id+"F2.wireOp",EDGE,"E3.8.2.2"),sQuery(id+"F2.wireOp",EDGE,"E3.8.2.3"),sQuery(id+"F2.wireOp",EDGE,"E3.8.2.4"),sQuery(id+"F2.wireOp",EDGE,"E3.8.2.5"),sQuery(id+"F2.wireOp",EDGE,"E3.8.3.0"),sQuery(id+"F2.wireOp",EDGE,"E3.8.3.1"),sQuery(id+"F2.wireOp",EDGE,"E3.8.3.2"),sQuery(id+"F2.wireOp",EDGE,"E3.8.3.3"),sQuery(id+"F2.wireOp",EDGE,"E3.8.3.4"),sQuery(id+"F2.wireOp",EDGE,"E3.8.3.5"),sQuery(id+"F2.wireOp",EDGE,"E3.8.4.3"),sQuery(id+"F2.wireOp",EDGE,"E3.8.4.4"),sQuery(id+"F2.wireOp",EDGE,"E8.0.2.2"),sQuery(id+"F2.wireOp",EDGE,"E8.0.2.3"),sQuery(id+"F2.wireOp",EDGE,"E8.1.1.1"),sQuery(id+"F2.wireOp",EDGE,"E8.1.1.2"),sQuery(id+"F2.wireOp",EDGE,"E8.1.1.3"),sQuery(id+"F2.wireOp",EDGE,"E8.1.1.4"),sQuery(id+"F2.wireOp",EDGE,"E8.1.2.0"),sQuery(id+"F2.wireOp",EDGE,"E8.1.2.1"),sQuery(id+"F2.wireOp",EDGE,"E8.1.2.2"),sQuery(id+"F2.wireOp",EDGE,"E8.1.2.3"),sQuery(id+"F2.wireOp",EDGE,"E8.1.2.4"),sQuery(id+"F2.wireOp",EDGE,"E8.1.2.5"),sQuery(id+"F2.wireOp",EDGE,"E8.1.3.2"),sQuery(id+"F2.wireOp",EDGE,"E8.1.3.3"),sQuery(id+"F2.wireOp",EDGE,"E8.1.3.4"),sQuery(id+"F2.wireOp",EDGE,"E8.1.3.5"),sQuery(id+"F2.wireOp",EDGE,"E8.2.1.0"),sQuery(id+"F2.wireOp",EDGE,"E8.2.1.1"),sQuery(id+"F2.wireOp",EDGE,"E8.2.1.2"),sQuery(id+"F2.wireOp",EDGE,"E8.2.1.3"),sQuery(id+"F2.wireOp",EDGE,"E8.2.1.4"),sQuery(id+"F2.wireOp",EDGE,"E8.2.1.5"),sQuery(id+"F2.wireOp",EDGE,"E8.2.2.0"),sQuery(id+"F2.wireOp",EDGE,"E8.2.2.1"),sQuery(id+"F2.wireOp",EDGE,"E8.2.2.2"),sQuery(id+"F2.wireOp",EDGE,"E8.2.2.3"),sQuery(id+"F2.wireOp",EDGE,"E8.2.2.4"),sQuery(id+"F2.wireOp",EDGE,"E8.2.2.5"),sQuery(id+"F2.wireOp",EDGE,"E8.2.3.0"),sQuery(id+"F2.wireOp",EDGE,"E8.2.3.1"),sQuery(id+"F2.wireOp",EDGE,"E8.2.3.2"),sQuery(id+"F2.wireOp",EDGE,"E8.2.3.3"),sQuery(id+"F2.wireOp",EDGE,"E8.2.3.4"),sQuery(id+"F2.wireOp",EDGE,"E8.2.3.5"),sQuery(id+"F2.wireOp",EDGE,"E8.2.4.3"),sQuery(id+"F2.wireOp",EDGE,"E8.2.4.4"),sQuery(id+"F2.wireOp",EDGE,"E8.2.4.5"),sQuery(id+"F2.wireOp",EDGE,"E8.3.0.1"),sQuery(id+"F2.wireOp",EDGE,"E8.3.0.2"),sQuery(id+"F2.wireOp",EDGE,"E8.3.0.3"),sQuery(id+"F2.wireOp",EDGE,"E8.3.1.0"),sQuery(id+"F2.wireOp",EDGE,"E8.3.1.1"),sQuery(id+"F2.wireOp",EDGE,"E8.3.1.2"),sQuery(id+"F2.wireOp",EDGE,"E8.3.1.3"),sQuery(id+"F2.wireOp",EDGE,"E8.3.1.4"),sQuery(id+"F2.wireOp",EDGE,"E8.3.1.5"),sQuery(id+"F2.wireOp",EDGE,"E8.3.2.0"),sQuery(id+"F2.wireOp",EDGE,"E8.3.2.1"),sQuery(id+"F2.wireOp",EDGE,"E8.3.2.2"),sQuery(id+"F2.wireOp",EDGE,"E8.3.2.3"),sQuery(id+"F2.wireOp",EDGE,"E8.3.2.4"),sQuery(id+"F2.wireOp",EDGE,"E8.3.2.5"),sQuery(id+"F2.wireOp",EDGE,"E8.3.3.0"),sQuery(id+"F2.wireOp",EDGE,"E8.3.3.1"),sQuery(id+"F2.wireOp",EDGE,"E8.3.3.2"),sQuery(id+"F2.wireOp",EDGE,"E8.3.3.3"),sQuery(id+"F2.wireOp",EDGE,"E8.3.3.4"),sQuery(id+"F2.wireOp",EDGE,"E8.3.3.5"),sQuery(id+"F2.wireOp",EDGE,"E8.3.4.0"),sQuery(id+"F2.wireOp",EDGE,"E8.3.4.2"),sQuery(id+"F2.wireOp",EDGE,"E8.3.4.3"),sQuery(id+"F2.wireOp",EDGE,"E8.3.4.4"),sQuery(id+"F2.wireOp",EDGE,"E8.3.4.5"),sQuery(id+"F2.wireOp",EDGE,"E8.4.0.0"),sQuery(id+"F2.wireOp",EDGE,"E8.4.0.1"),sQuery(id+"F2.wireOp",EDGE,"E8.4.0.2"),sQuery(id+"F2.wireOp",EDGE,"E8.4.0.3"),sQuery(id+"F2.wireOp",EDGE,"E8.4.1.0"),sQuery(id+"F2.wireOp",EDGE,"E8.4.1.1"),sQuery(id+"F2.wireOp",EDGE,"E8.4.1.2"),sQuery(id+"F2.wireOp",EDGE,"E8.4.1.3"),sQuery(id+"F2.wireOp",EDGE,"E8.4.1.4"),sQuery(id+"F2.wireOp",EDGE,"E8.4.1.5"),sQuery(id+"F2.wireOp",EDGE,"E8.4.2.0"),sQuery(id+"F2.wireOp",EDGE,"E8.4.2.1"),sQuery(id+"F2.wireOp",EDGE,"E8.4.2.2"),sQuery(id+"F2.wireOp",EDGE,"E8.4.2.3"),sQuery(id+"F2.wireOp",EDGE,"E8.4.2.4"),sQuery(id+"F2.wireOp",EDGE,"E8.4.2.5"),sQuery(id+"F2.wireOp",EDGE,"E8.4.3.0"),sQuery(id+"F2.wireOp",EDGE,"E8.4.3.1"),sQuery(id+"F2.wireOp",EDGE,"E8.4.3.2"),sQuery(id+"F2.wireOp",EDGE,"E8.4.3.3"),sQuery(id+"F2.wireOp",EDGE,"E8.4.3.4"),sQuery(id+"F2.wireOp",EDGE,"E8.4.3.5"),sQuery(id+"F2.wireOp",EDGE,"E8.4.4.0"),sQuery(id+"F2.wireOp",EDGE,"E8.4.4.1"),sQuery(id+"F2.wireOp",EDGE,"E8.4.4.2"),sQuery(id+"F2.wireOp",EDGE,"E8.4.4.3"),sQuery(id+"F2.wireOp",EDGE,"E8.4.4.4"),sQuery(id+"F2.wireOp",EDGE,"E8.4.4.5"),sQuery(id+"F2.wireOp",EDGE,"E8.5.0.0"),sQuery(id+"F2.wireOp",EDGE,"E8.5.0.1"),sQuery(id+"F2.wireOp",EDGE,"E8.5.0.2"),sQuery(id+"F2.wireOp",EDGE,"E8.5.0.3"),sQuery(id+"F2.wireOp",EDGE,"E8.5.1.0"),sQuery(id+"F2.wireOp",EDGE,"E8.5.1.1"),sQuery(id+"F2.wireOp",EDGE,"E8.5.1.2"),sQuery(id+"F2.wireOp",EDGE,"E8.5.1.3"),sQuery(id+"F2.wireOp",EDGE,"E8.5.1.4"),sQuery(id+"F2.wireOp",EDGE,"E8.5.1.5"),sQuery(id+"F2.wireOp",EDGE,"E8.5.2.0"),sQuery(id+"F2.wireOp",EDGE,"E8.5.2.1"),sQuery(id+"F2.wireOp",EDGE,"E8.5.2.2"),sQuery(id+"F2.wireOp",EDGE,"E8.5.2.3"),sQuery(id+"F2.wireOp",EDGE,"E8.5.2.4"),sQuery(id+"F2.wireOp",EDGE,"E8.5.2.5"),sQuery(id+"F2.wireOp",EDGE,"E8.5.3.0"),sQuery(id+"F2.wireOp",EDGE,"E8.5.3.1"),sQuery(id+"F2.wireOp",EDGE,"E8.5.3.2"),sQuery(id+"F2.wireOp",EDGE,"E8.5.3.3"),sQuery(id+"F2.wireOp",EDGE,"E8.5.3.4"),sQuery(id+"F2.wireOp",EDGE,"E8.5.3.5"),sQuery(id+"F2.wireOp",EDGE,"E8.5.4.0"),sQuery(id+"F2.wireOp",EDGE,"E8.5.4.1"),sQuery(id+"F2.wireOp",EDGE,"E8.5.4.3"),sQuery(id+"F2.wireOp",EDGE,"E8.5.4.4"),sQuery(id+"F2.wireOp",EDGE,"E8.5.4.5"),sQuery(id+"F2.wireOp",EDGE,"E8.6.0.0"),sQuery(id+"F2.wireOp",EDGE,"E8.6.0.1"),sQuery(id+"F2.wireOp",EDGE,"E8.6.0.2"),sQuery(id+"F2.wireOp",EDGE,"E8.6.1.0"),sQuery(id+"F2.wireOp",EDGE,"E8.6.1.1"),sQuery(id+"F2.wireOp",EDGE,"E8.6.1.2"),sQuery(id+"F2.wireOp",EDGE,"E8.6.1.3"),sQuery(id+"F2.wireOp",EDGE,"E8.6.1.4"),sQuery(id+"F2.wireOp",EDGE,"E8.6.1.5"),sQuery(id+"F2.wireOp",EDGE,"E8.6.2.0"),sQuery(id+"F2.wireOp",EDGE,"E8.6.2.1"),sQuery(id+"F2.wireOp",EDGE,"E8.6.2.2"),sQuery(id+"F2.wireOp",EDGE,"E8.6.2.3"),sQuery(id+"F2.wireOp",EDGE,"E8.6.2.4"),sQuery(id+"F2.wireOp",EDGE,"E8.6.2.5"),sQuery(id+"F2.wireOp",EDGE,"E8.6.3.0"),sQuery(id+"F2.wireOp",EDGE,"E8.6.3.1"),sQuery(id+"F2.wireOp",EDGE,"E8.6.3.2"),sQuery(id+"F2.wireOp",EDGE,"E8.6.3.3"),sQuery(id+"F2.wireOp",EDGE,"E8.6.3.4"),sQuery(id+"F2.wireOp",EDGE,"E8.6.3.5"),sQuery(id+"F2.wireOp",EDGE,"E8.6.4.0"),sQuery(id+"F2.wireOp",EDGE,"E8.6.4.4"),sQuery(id+"F2.wireOp",EDGE,"E8.6.4.5"),sQuery(id+"F2.wireOp",EDGE,"E8.7.1.0"),sQuery(id+"F2.wireOp",EDGE,"E8.7.1.1"),sQuery(id+"F2.wireOp",EDGE,"E8.7.1.2"),sQuery(id+"F2.wireOp",EDGE,"E8.7.1.3"),sQuery(id+"F2.wireOp",EDGE,"E8.7.1.4"),sQuery(id+"F2.wireOp",EDGE,"E8.7.1.5"),sQuery(id+"F2.wireOp",EDGE,"E8.7.2.0"),sQuery(id+"F2.wireOp",EDGE,"E8.7.2.1"),sQuery(id+"F2.wireOp",EDGE,"E8.7.2.2"),sQuery(id+"F2.wireOp",EDGE,"E8.7.2.3"),sQuery(id+"F2.wireOp",EDGE,"E8.7.2.4"),sQuery(id+"F2.wireOp",EDGE,"E8.7.2.5"),sQuery(id+"F2.wireOp",EDGE,"E8.7.3.0"),sQuery(id+"F2.wireOp",EDGE,"E8.7.3.1"),sQuery(id+"F2.wireOp",EDGE,"E8.7.3.2"),sQuery(id+"F2.wireOp",EDGE,"E8.7.3.3"),sQuery(id+"F2.wireOp",EDGE,"E8.7.3.4"),sQuery(id+"F2.wireOp",EDGE,"E8.7.3.5"),sQuery(id+"F2.wireOp",EDGE,"E8.8.1.0"),sQuery(id+"F2.wireOp",EDGE,"E8.8.1.1"),sQuery(id+"F2.wireOp",EDGE,"E8.8.2.0"),sQuery(id+"F2.wireOp",EDGE,"E8.8.2.1"),sQuery(id+"F2.wireOp",EDGE,"E8.8.2.2"),sQuery(id+"F2.wireOp",EDGE,"E8.8.2.4"),sQuery(id+"F2.wireOp",EDGE,"E8.8.2.5"),sQuery(id+"F2.wireOp",EDGE,"E8.8.3.0"),sQuery(id+"F2.wireOp",EDGE,"E8.8.3.5"),sQuery(id+"F2.wireOp",EDGE,"E9")])],"isStart":false});
            var sketch = newSketch(context, id + "F5", { "sketchPlane" : qUnion([Q0])});
            skText(sketch, "E10", { "text": "J", "fontName": "RobotoSlab-Bold.ttf"});
            const initialGuessF5  = {"E10": [-0.008, -0.00914, 1, 0, 0.01828]};
            skSetInitialGuess(sketch, initialGuessF5);
            skSolve(sketch);
        }
        {
            var Q0;
            Q0 = qSketchRegion(id + "F5", true);
            extrude(context, id + "F6", {"entities" : qUnion([Q0]), "operationType" : NewBodyOperationType.REMOVE, "endBound" : BoundingType.THROUGH_ALL, "oppositeDirection" : true, "depth" : 25 * mm, "offsetDistance" : 25 * mm});
        }
        {
            var Q0;
            {var subQ0=sQuery(id+"F0.wireOp",EDGE,"E0");var subQ1=makeQuery(id+"F1.opExtrude","CAP_EDGE",EDGE,{"disambiguationData":[OSD([subQ0])],"isStart":false});var subQ2=makeQuery(id+"F2.imprint","INTERSECT",VERTEX,{"derivedFrom":[subQ1,sQuery(id+"F2.wireOp",EDGE,"E8.8.3.1")]});var subQ4=makeQuery(id+"F2.imprint","INTERSECT",VERTEX,{"derivedFrom":[subQ1,sQuery(id+"F2.wireOp",EDGE,"E8.8.2.2")]});var subQ6=makeQuery(id+"F2.imprint","INTERSECT",VERTEX,{"derivedFrom":[subQ1,sQuery(id+"F2.wireOp",EDGE,"E8.8.1.2")]});var subQ8=makeQuery(id+"F2.imprint","INTERSECT",VERTEX,{"derivedFrom":[subQ1,sQuery(id+"F2.wireOp",EDGE,"E8.7.4.0")]});var subQ10=makeQuery(id+"F2.imprint","INTERSECT",VERTEX,{"derivedFrom":[subQ1,sQuery(id+"F2.wireOp",EDGE,"E8.6.4.1")]});var subQ11=makeQuery(id+"F2.imprint","INTERSECT",VERTEX,{"derivedFrom":[subQ1,sQuery(id+"F2.wireOp",EDGE,"E8.6.4.3")]});var subQ12=makeQuery(id+"F2.imprint","INTERSECT",VERTEX,{"derivedFrom":[subQ1,sQuery(id+"F2.wireOp",EDGE,"E8.6.0.0")]});var subQ14=makeQuery(id+"F2.imprint","INTERSECT",VERTEX,{"derivedFrom":[subQ1,sQuery(id+"F2.wireOp",EDGE,"E8.5.0.3")]});var subQ16=makeQuery(id+"F2.imprint","INTERSECT",VERTEX,{"derivedFrom":[subQ1,sQuery(id+"F2.wireOp",EDGE,"E8.3.4.1")]});var subQ18=makeQuery(id+"F2.imprint","INTERSECT",VERTEX,{"derivedFrom":[subQ1,sQuery(id+"F2.wireOp",EDGE,"E8.2.4.3")]});var subQ20=makeQuery(id+"F2.imprint","INTERSECT",VERTEX,{"derivedFrom":[subQ1,sQuery(id+"F2.wireOp",EDGE,"E4.6.5.5")]});var subQ22=makeQuery(id+"F2.imprint","INTERSECT",VERTEX,{"derivedFrom":[subQ1,sQuery(id+"F2.wireOp",EDGE,"E4.6.4.5")]});var subQ23=makeQuery(id+"F2.imprint","INTERSECT",VERTEX,{"derivedFrom":[subQ1,sQuery(id+"F2.wireOp",EDGE,"E4.9.4.5")]});var subQ24=makeQuery(id+"F2.imprint","INTERSECT",VERTEX,{"derivedFrom":[subQ1,sQuery(id+"F2.wireOp",EDGE,"E3.9.3.3")]});var subQ25=makeQuery(id+"F2.imprint","INTERSECT",VERTEX,{"derivedFrom":[subQ1,sQuery(id+"F2.wireOp",EDGE,"E3.9.3.5")]});var subQ26=makeQuery(id+"F2.imprint","INTERSECT",VERTEX,{"derivedFrom":[subQ1,sQuery(id+"F2.wireOp",EDGE,"E3.9.2.3")]});var subQ27=makeQuery(id+"F2.imprint","INTERSECT",VERTEX,{"derivedFrom":[subQ1,sQuery(id+"F2.wireOp",EDGE,"E3.9.2.5")]});var subQ28=makeQuery(id+"F2.imprint","INTERSECT",VERTEX,{"derivedFrom":[subQ1,sQuery(id+"F2.wireOp",EDGE,"E3.8.4.2")]});var subQ29=makeQuery(id+"F2.imprint","INTERSECT",VERTEX,{"derivedFrom":[subQ1,sQuery(id+"F2.wireOp",EDGE,"E3.8.4.5")]});var subQ30=makeQuery(id+"F2.imprint","INTERSECT",VERTEX,{"derivedFrom":[subQ1,sQuery(id+"F2.wireOp",EDGE,"E3.8.1.0")]});var subQ31=makeQuery(id+"F2.imprint","INTERSECT",VERTEX,{"derivedFrom":[subQ1,sQuery(id+"F2.wireOp",EDGE,"E3.8.1.4")]});var subQ32=makeQuery(id+"F2.imprint","INTERSECT",VERTEX,{"derivedFrom":[subQ1,sQuery(id+"F2.wireOp",EDGE,"E3.2.4.4")]});var subQ33=makeQuery(id+"F2.imprint","INTERSECT",VERTEX,{"derivedFrom":[subQ1,sQuery(id+"F2.wireOp",EDGE,"E3.2.4.5")]});Q0=makeQuery(id+"F3.opExtrude","CAP_EDGE",EDGE,{"disambiguationData":[OSD([subQ0]),TDD([makeQuery(id+"F2.imprint","IMPRINT",EDGE,{"disambiguationData":[TD([[makeQuery(id+"F2.imprint","INTERSECT",VERTEX,{"disambiguationData":[OD(0.0)],"derivedFrom":[subQ1,makeQuery(id+"F1.opExtrude","CAP_EDGE",EDGE,{"disambiguationData":[OSD([sQuery(id+"F0.wireOp",EDGE,"E1")])],"isStart":false})]}),-1.0]])],"derivedFrom":subQ1}),makeQuery(id+"F2.imprint","IMPRINT",EDGE,{"disambiguationData":[TD([[makeQuery(id+"F2.imprint","INTERSECT",VERTEX,{"derivedFrom":[subQ1,sQuery(id+"F2.wireOp",EDGE,"E3.1.4.1")]}),1.0]])],"derivedFrom":subQ1}),makeQuery(id+"F2.imprint","IMPRINT",EDGE,{"disambiguationData":[TD([[subQ33,1.0]])],"derivedFrom":subQ1}),makeQuery(id+"F2.imprint","IMPRINT",EDGE,{"disambiguationData":[TD([[subQ30,-1.0]])],"derivedFrom":subQ1}),makeQuery(id+"F2.imprint","IMPRINT",EDGE,{"disambiguationData":[TD([[subQ31,1.0]])],"derivedFrom":subQ1}),makeQuery(id+"F2.imprint","IMPRINT",EDGE,{"disambiguationData":[TD([[subQ28,1.0]])],"derivedFrom":subQ1}),makeQuery(id+"F2.imprint","IMPRINT",EDGE,{"disambiguationData":[TD([[subQ29,-1.0]])],"derivedFrom":subQ1}),makeQuery(id+"F2.imprint","IMPRINT",EDGE,{"disambiguationData":[TD([[subQ26,1.0]])],"derivedFrom":subQ1}),makeQuery(id+"F2.imprint","IMPRINT",EDGE,{"disambiguationData":[TD([[subQ27,-1.0]])],"derivedFrom":subQ1}),makeQuery(id+"F2.imprint","IMPRINT",EDGE,{"disambiguationData":[TD([[subQ24,1.0]])],"derivedFrom":subQ1}),makeQuery(id+"F2.imprint","IMPRINT",EDGE,{"disambiguationData":[TD([[subQ25,-1.0]])],"derivedFrom":subQ1}),makeQuery(id+"F2.imprint","IMPRINT",EDGE,{"disambiguationData":[TD([[subQ22,1.0]])],"derivedFrom":subQ1}),makeQuery(id+"F2.imprint","IMPRINT",EDGE,{"disambiguationData":[TD([[subQ23,-1.0]])],"derivedFrom":subQ1}),makeQuery(id+"F2.imprint","IMPRINT",EDGE,{"disambiguationData":[TD([[subQ20,1.0]])],"derivedFrom":subQ1}),makeQuery(id+"F2.imprint","IMPRINT",EDGE,{"disambiguationData":[TD([[subQ18,1.0]])],"derivedFrom":subQ1}),makeQuery(id+"F2.imprint","IMPRINT",EDGE,{"disambiguationData":[TD([[subQ14,-1.0]])],"derivedFrom":subQ1}),makeQuery(id+"F2.imprint","IMPRINT",EDGE,{"disambiguationData":[TD([[subQ11,1.0]])],"derivedFrom":subQ1}),makeQuery(id+"F2.imprint","IMPRINT",EDGE,{"disambiguationData":[TD([[subQ32,1.0]])],"derivedFrom":subQ1}),makeQuery(id+"F2.imprint","IMPRINT",EDGE,{"disambiguationData":[TD([[subQ30,1.0]])],"derivedFrom":subQ1}),makeQuery(id+"F2.imprint","IMPRINT",EDGE,{"disambiguationData":[TD([[subQ28,-1.0]])],"derivedFrom":subQ1}),makeQuery(id+"F2.imprint","IMPRINT",EDGE,{"disambiguationData":[TD([[subQ26,-1.0]])],"derivedFrom":subQ1}),makeQuery(id+"F2.imprint","IMPRINT",EDGE,{"disambiguationData":[TD([[subQ24,-1.0]])],"derivedFrom":subQ1}),makeQuery(id+"F2.imprint","IMPRINT",EDGE,{"disambiguationData":[TD([[subQ22,-1.0]])],"derivedFrom":subQ1}),makeQuery(id+"F2.imprint","IMPRINT",EDGE,{"disambiguationData":[TD([[subQ20,-1.0]])],"derivedFrom":subQ1}),makeQuery(id+"F2.imprint","IMPRINT",EDGE,{"disambiguationData":[TD([[subQ18,-1.0]])],"derivedFrom":subQ1}),makeQuery(id+"F2.imprint","IMPRINT",EDGE,{"disambiguationData":[TD([[subQ16,1.0]])],"derivedFrom":subQ1}),makeQuery(id+"F2.imprint","IMPRINT",EDGE,{"disambiguationData":[TD([[subQ14,1.0]])],"derivedFrom":subQ1}),makeQuery(id+"F2.imprint","IMPRINT",EDGE,{"disambiguationData":[TD([[subQ12,-1.0]])],"derivedFrom":subQ1}),makeQuery(id+"F2.imprint","IMPRINT",EDGE,{"disambiguationData":[TD([[subQ10,1.0]])],"derivedFrom":subQ1}),makeQuery(id+"F2.imprint","IMPRINT",EDGE,{"disambiguationData":[TD([[subQ8,1.0]])],"derivedFrom":subQ1}),makeQuery(id+"F2.imprint","IMPRINT",EDGE,{"disambiguationData":[TD([[subQ6,1.0]])],"derivedFrom":subQ1}),makeQuery(id+"F2.imprint","IMPRINT",EDGE,{"disambiguationData":[TD([[subQ4,1.0]])],"derivedFrom":subQ1}),makeQuery(id+"F2.imprint","IMPRINT",EDGE,{"disambiguationData":[TD([[subQ2,1.0]])],"derivedFrom":subQ1})])],"isStart":false});}
            var Q1;
            {var subQ0=sQuery(id+"F0.wireOp",EDGE,"E0");var subQ1=makeQuery(id+"F1.opExtrude","CAP_EDGE",EDGE,{"disambiguationData":[OSD([subQ0])],"isStart":false});var subQ2=makeQuery(id+"F2.imprint","INTERSECT",VERTEX,{"derivedFrom":[subQ1,sQuery(id+"F2.wireOp",EDGE,"E8.3.0.0")]});var subQ3=makeQuery(id+"F2.imprint","INTERSECT",VERTEX,{"derivedFrom":[subQ1,sQuery(id+"F2.wireOp",EDGE,"E8.3.0.3")]});var subQ4=makeQuery(id+"F2.imprint","INTERSECT",VERTEX,{"derivedFrom":[subQ1,sQuery(id+"F2.wireOp",EDGE,"E8.2.0.1")]});var subQ5=makeQuery(id+"F2.imprint","INTERSECT",VERTEX,{"derivedFrom":[subQ1,sQuery(id+"F2.wireOp",EDGE,"E8.2.0.3")]});var subQ6=makeQuery(id+"F2.imprint","INTERSECT",VERTEX,{"derivedFrom":[subQ1,sQuery(id+"F2.wireOp",EDGE,"E8.1.1.0")]});var subQ8=makeQuery(id+"F2.imprint","INTERSECT",VERTEX,{"derivedFrom":[subQ1,sQuery(id+"F2.wireOp",EDGE,"E8.0.2.2")]});var subQ10=makeQuery(id+"F2.imprint","INTERSECT",VERTEX,{"derivedFrom":[subQ1,sQuery(id+"F2.wireOp",EDGE,"E3.2.1.2")]});var subQ11=makeQuery(id+"F2.imprint","INTERSECT",VERTEX,{"derivedFrom":[subQ1,sQuery(id+"F2.wireOp",EDGE,"E3.2.1.4")]});var subQ12=makeQuery(id+"F2.imprint","INTERSECT",VERTEX,{"derivedFrom":[subQ1,sQuery(id+"F2.wireOp",EDGE,"E3.1.3.3")]});var subQ13=makeQuery(id+"F2.imprint","INTERSECT",VERTEX,{"derivedFrom":[subQ1,sQuery(id+"F2.wireOp",EDGE,"E3.1.3.5")]});var subQ14=makeQuery(id+"F2.imprint","INTERSECT",VERTEX,{"derivedFrom":[subQ1,sQuery(id+"F2.wireOp",EDGE,"E3.1.2.3")]});var subQ15=makeQuery(id+"F2.imprint","INTERSECT",VERTEX,{"derivedFrom":[subQ1,sQuery(id+"F2.wireOp",EDGE,"E3.1.2.5")]});Q1=makeQuery(id+"F3.opExtrude","CAP_EDGE",EDGE,{"disambiguationData":[OSD([subQ0]),TDD([makeQuery(id+"F2.imprint","IMPRINT",EDGE,{"disambiguationData":[TD([[makeQuery(id+"F2.imprint","INTERSECT",VERTEX,{"disambiguationData":[OD(1.0)],"derivedFrom":[subQ1,makeQuery(id+"F1.opExtrude","CAP_EDGE",EDGE,{"disambiguationData":[OSD([sQuery(id+"F0.wireOp",EDGE,"E1")])],"isStart":false})]}),1.0]])],"derivedFrom":subQ1}),makeQuery(id+"F2.imprint","IMPRINT",EDGE,{"disambiguationData":[TD([[subQ14,-1.0]])],"derivedFrom":subQ1}),makeQuery(id+"F2.imprint","IMPRINT",EDGE,{"disambiguationData":[TD([[subQ15,1.0]])],"derivedFrom":subQ1}),makeQuery(id+"F2.imprint","IMPRINT",EDGE,{"disambiguationData":[TD([[subQ12,-1.0]])],"derivedFrom":subQ1}),makeQuery(id+"F2.imprint","IMPRINT",EDGE,{"disambiguationData":[TD([[subQ13,1.0]])],"derivedFrom":subQ1}),makeQuery(id+"F2.imprint","IMPRINT",EDGE,{"disambiguationData":[TD([[subQ10,-1.0]])],"derivedFrom":subQ1}),makeQuery(id+"F2.imprint","IMPRINT",EDGE,{"disambiguationData":[TD([[subQ11,1.0]])],"derivedFrom":subQ1}),makeQuery(id+"F2.imprint","IMPRINT",EDGE,{"disambiguationData":[TD([[subQ5,-1.0]])],"derivedFrom":subQ1}),makeQuery(id+"F2.imprint","IMPRINT",EDGE,{"disambiguationData":[TD([[subQ3,-1.0]])],"derivedFrom":subQ1}),makeQuery(id+"F2.imprint","IMPRINT",EDGE,{"disambiguationData":[TD([[subQ14,1.0]])],"derivedFrom":subQ1}),makeQuery(id+"F2.imprint","IMPRINT",EDGE,{"disambiguationData":[TD([[subQ12,1.0]])],"derivedFrom":subQ1}),makeQuery(id+"F2.imprint","IMPRINT",EDGE,{"disambiguationData":[TD([[subQ10,1.0]])],"derivedFrom":subQ1}),makeQuery(id+"F2.imprint","IMPRINT",EDGE,{"disambiguationData":[TD([[subQ8,-1.0]])],"derivedFrom":subQ1}),makeQuery(id+"F2.imprint","IMPRINT",EDGE,{"disambiguationData":[TD([[subQ6,-1.0]])],"derivedFrom":subQ1}),makeQuery(id+"F2.imprint","IMPRINT",EDGE,{"disambiguationData":[TD([[subQ4,-1.0]])],"derivedFrom":subQ1}),makeQuery(id+"F2.imprint","IMPRINT",EDGE,{"disambiguationData":[TD([[subQ2,-1.0]])],"derivedFrom":subQ1})])],"isStart":false});}
            var Q2;
            Q2=makeQuery(id+"F3.opExtrude","CAP_EDGE",EDGE,{"disambiguationData":[OSD([sQuery(id+"F0.wireOp",EDGE,"E1")])],"isStart":false});
            fillet(context, id + "F7", {"entities" : qUnion([Q0, Q1, Q2]), "radius" : 0.4 * mm, "tangentPropagation" : true, "allowEdgeOverflow" : false});
        }
        {
            var Q0;
            Q0=makeQuery(id+"F1.opExtrude","CAP_FACE",FACE,{"disambiguationData":[OSD([sQuery(id+"F0.wireOp",EDGE,"E0"),sQuery(id+"F0.wireOp",EDGE,"E1")])],"isStart":true});
            chamfer(context, id + "F8", {"entities" : qUnion([Q0]), "width" : 0.5 * mm, "tangentPropagation" : true});
        }
    });
